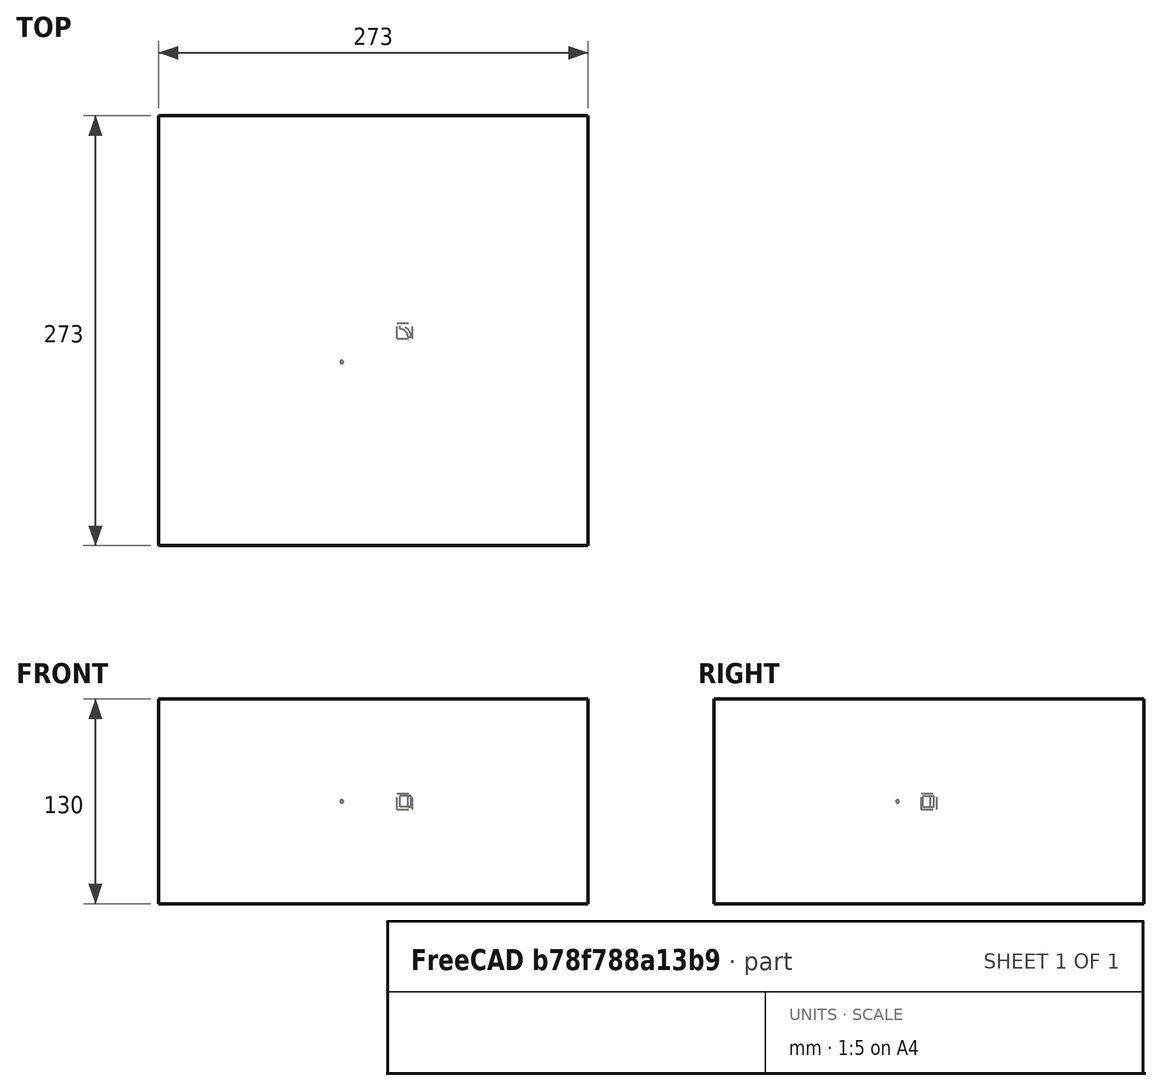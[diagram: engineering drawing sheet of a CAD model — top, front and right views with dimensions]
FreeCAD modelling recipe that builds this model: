
FCSTD DOCUMENT  (FreeCAD 1.0R39109 (Git))
Label: polarArray-of-Part-array-xformed
License: All rights reserved
LicenseURL: http://en.wikipedia.org/wiki/All_rights_reserved
objects: App::DocumentObjectGroupPython×1251, App::Part×5, Part::FeaturePython×4, Part::Sphere×1
note: 4 computed .brp shape members not serialized (recipe doc carries the construction recipe); baked Part::Feature solids carry a one-line shape summary decoded from their .brp

FEATURE [App::DocumentObjectGroupPython] HALFPI  # scripted group (container) (typed FeaturePython)
  name = HALFPI
  value = pi/2.
FEATURE [App::DocumentObjectGroupPython] PI  # scripted group (container) (typed FeaturePython)
  name = PI
  value = 1.*pi
FEATURE [App::DocumentObjectGroupPython] TWOPI  # scripted group (container) (typed FeaturePython)
  name = TWOPI
  value = 2.*pi
FEATURE [App::DocumentObjectGroupPython] Constants  # scripted group (container) (typed FeaturePython)
  Group = -> [HALFPI,PI,TWOPI]
FEATURE [App::DocumentObjectGroupPython] Variables  # scripted group (container) (typed FeaturePython)
FEATURE [App::DocumentObjectGroupPython] Quantities  # scripted group (container) (typed FeaturePython)
FEATURE [App::DocumentObjectGroupPython] Isotopes  # scripted group (container) (typed FeaturePython)
FEATURE [App::DocumentObjectGroupPython] Elements  # scripted group (container) (typed FeaturePython)
FEATURE [App::DocumentObjectGroupPython] Matrix  # scripted group (container) (typed FeaturePython)
FEATURE [App::DocumentObjectGroupPython] Surfaces  # scripted group (container) (typed FeaturePython)
FEATURE [App::DocumentObjectGroupPython] Opticals  # scripted group (container) (typed FeaturePython)
  Group = -> [Matrix,Surfaces]
FEATURE [App::DocumentObjectGroupPython] G4Isotopes  # scripted group (container) (typed FeaturePython)
FEATURE [App::DocumentObjectGroupPython] H_element  # scripted group (container) (typed FeaturePython)
  Z = 1
  atom_value = 1.008
  formula = H
  name = H_element
FEATURE [App::DocumentObjectGroupPython] He_element  # scripted group (container) (typed FeaturePython)
  Z = 2
  atom_value = 4.0026
  formula = He
  name = He_element
FEATURE [App::DocumentObjectGroupPython] Li_element  # scripted group (container) (typed FeaturePython)
  Z = 3
  atom_value = 6.94
  formula = Li
  name = Li_element
FEATURE [App::DocumentObjectGroupPython] Be_element  # scripted group (container) (typed FeaturePython)
  Z = 4
  atom_value = 9.01218
  formula = Be
  name = Be_element
FEATURE [App::DocumentObjectGroupPython] B_element  # scripted group (container) (typed FeaturePython)
  Z = 5
  atom_value = 10.81
  formula = B
  name = B_element
FEATURE [App::DocumentObjectGroupPython] C_element  # scripted group (container) (typed FeaturePython)
  Z = 6
  atom_value = 12.011
  formula = C
  name = C_element
FEATURE [App::DocumentObjectGroupPython] N_element  # scripted group (container) (typed FeaturePython)
  Z = 7
  atom_value = 14.007
  formula = N
  name = N_element
FEATURE [App::DocumentObjectGroupPython] O_element  # scripted group (container) (typed FeaturePython)
  Z = 8
  atom_value = 15.999
  formula = O
  name = O_element
FEATURE [App::DocumentObjectGroupPython] F_element  # scripted group (container) (typed FeaturePython)
  Z = 9
  atom_value = 18.9984
  formula = F
  name = F_element
FEATURE [App::DocumentObjectGroupPython] Ne_element  # scripted group (container) (typed FeaturePython)
  Z = 10
  atom_value = 20.1797
  formula = Ne
  name = Ne_element
FEATURE [App::DocumentObjectGroupPython] Na_element  # scripted group (container) (typed FeaturePython)
  Z = 11
  atom_value = 22.9898
  formula = Na
  name = Na_element
FEATURE [App::DocumentObjectGroupPython] Mg_element  # scripted group (container) (typed FeaturePython)
  Z = 12
  atom_value = 24.305
  formula = Mg
  name = Mg_element
FEATURE [App::DocumentObjectGroupPython] Al_element  # scripted group (container) (typed FeaturePython)
  Z = 13
  atom_value = 26.9815
  formula = Al
  name = Al_element
FEATURE [App::DocumentObjectGroupPython] Si_element  # scripted group (container) (typed FeaturePython)
  Z = 14
  atom_value = 28.085
  formula = Si
  name = Si_element
FEATURE [App::DocumentObjectGroupPython] P_element  # scripted group (container) (typed FeaturePython)
  Z = 15
  atom_value = 30.9738
  formula = P
  name = P_element
FEATURE [App::DocumentObjectGroupPython] S_element  # scripted group (container) (typed FeaturePython)
  Z = 16
  atom_value = 32.06
  formula = S
  name = S_element
FEATURE [App::DocumentObjectGroupPython] Cl_element  # scripted group (container) (typed FeaturePython)
  Z = 17
  atom_value = 35.45
  formula = Cl
  name = Cl_element
FEATURE [App::DocumentObjectGroupPython] Ar_element  # scripted group (container) (typed FeaturePython)
  Z = 18
  atom_value = 39.95
  formula = Ar
  name = Ar_element
FEATURE [App::DocumentObjectGroupPython] K_element  # scripted group (container) (typed FeaturePython)
  Z = 19
  atom_value = 39.0983
  formula = K
  name = K_element
FEATURE [App::DocumentObjectGroupPython] Ca_element  # scripted group (container) (typed FeaturePython)
  Z = 20
  atom_value = 40.078
  formula = Ca
  name = Ca_element
FEATURE [App::DocumentObjectGroupPython] Sc_element  # scripted group (container) (typed FeaturePython)
  Z = 21
  atom_value = 44.9559
  formula = Sc
  name = Sc_element
FEATURE [App::DocumentObjectGroupPython] Ti_element  # scripted group (container) (typed FeaturePython)
  Z = 22
  atom_value = 47.867
  formula = Ti
  name = Ti_element
FEATURE [App::DocumentObjectGroupPython] V_element  # scripted group (container) (typed FeaturePython)
  Z = 23
  atom_value = 50.9415
  formula = V
  name = V_element
FEATURE [App::DocumentObjectGroupPython] Cr_element  # scripted group (container) (typed FeaturePython)
  Z = 24
  atom_value = 51.9961
  formula = Cr
  name = Cr_element
FEATURE [App::DocumentObjectGroupPython] Mn_element  # scripted group (container) (typed FeaturePython)
  Z = 25
  atom_value = 54.938
  formula = Mn
  name = Mn_element
FEATURE [App::DocumentObjectGroupPython] Fe_element  # scripted group (container) (typed FeaturePython)
  Z = 26
  atom_value = 55.845
  formula = Fe
  name = Fe_element
FEATURE [App::DocumentObjectGroupPython] Co_element  # scripted group (container) (typed FeaturePython)
  Z = 27
  atom_value = 58.9332
  formula = Co
  name = Co_element
FEATURE [App::DocumentObjectGroupPython] Ni_element  # scripted group (container) (typed FeaturePython)
  Z = 28
  atom_value = 58.6934
  formula = Ni
  name = Ni_element
FEATURE [App::DocumentObjectGroupPython] Cu_element  # scripted group (container) (typed FeaturePython)
  Z = 29
  atom_value = 63.546
  formula = Cu
  name = Cu_element
FEATURE [App::DocumentObjectGroupPython] Zn_element  # scripted group (container) (typed FeaturePython)
  Z = 30
  atom_value = 65.38
  formula = Zn
  name = Zn_element
FEATURE [App::DocumentObjectGroupPython] Ga_element  # scripted group (container) (typed FeaturePython)
  Z = 31
  atom_value = 69.723
  formula = Ga
  name = Ga_element
FEATURE [App::DocumentObjectGroupPython] Ge_element  # scripted group (container) (typed FeaturePython)
  Z = 32
  atom_value = 72.63
  formula = Ge
  name = Ge_element
FEATURE [App::DocumentObjectGroupPython] As_element  # scripted group (container) (typed FeaturePython)
  Z = 33
  atom_value = 74.9216
  formula = As
  name = As_element
FEATURE [App::DocumentObjectGroupPython] Se_element  # scripted group (container) (typed FeaturePython)
  Z = 34
  atom_value = 78.971
  formula = Se
  name = Se_element
FEATURE [App::DocumentObjectGroupPython] Br_element  # scripted group (container) (typed FeaturePython)
  Z = 35
  atom_value = 79.904
  formula = Br
  name = Br_element
FEATURE [App::DocumentObjectGroupPython] Kr_element  # scripted group (container) (typed FeaturePython)
  Z = 36
  atom_value = 83.798
  formula = Kr
  name = Kr_element
FEATURE [App::DocumentObjectGroupPython] Rb_element  # scripted group (container) (typed FeaturePython)
  Z = 37
  atom_value = 85.4678
  formula = Rb
  name = Rb_element
FEATURE [App::DocumentObjectGroupPython] Sr_element  # scripted group (container) (typed FeaturePython)
  Z = 38
  atom_value = 87.62
  formula = Sr
  name = Sr_element
FEATURE [App::DocumentObjectGroupPython] Y_element  # scripted group (container) (typed FeaturePython)
  Z = 39
  atom_value = 88.9058
  formula = Y
  name = Y_element
FEATURE [App::DocumentObjectGroupPython] Zr_element  # scripted group (container) (typed FeaturePython)
  Z = 40
  atom_value = 91.224
  formula = Zr
  name = Zr_element
FEATURE [App::DocumentObjectGroupPython] Nb_element  # scripted group (container) (typed FeaturePython)
  Z = 41
  atom_value = 92.9064
  formula = Nb
  name = Nb_element
FEATURE [App::DocumentObjectGroupPython] Mo_element  # scripted group (container) (typed FeaturePython)
  Z = 42
  atom_value = 95.95
  formula = Mo
  name = Mo_element
FEATURE [App::DocumentObjectGroupPython] Tc_element  # scripted group (container) (typed FeaturePython)
  Z = 43
  atom_value = 97
  formula = Tc
  name = Tc_element
FEATURE [App::DocumentObjectGroupPython] Ru_element  # scripted group (container) (typed FeaturePython)
  Z = 44
  atom_value = 101.07
  formula = Ru
  name = Ru_element
FEATURE [App::DocumentObjectGroupPython] Rh_element  # scripted group (container) (typed FeaturePython)
  Z = 45
  atom_value = 102.905
  formula = Rh
  name = Rh_element
FEATURE [App::DocumentObjectGroupPython] Pd_element  # scripted group (container) (typed FeaturePython)
  Z = 46
  atom_value = 106.42
  formula = Pd
  name = Pd_element
FEATURE [App::DocumentObjectGroupPython] Ag_element  # scripted group (container) (typed FeaturePython)
  Z = 47
  atom_value = 107.868
  formula = Ag
  name = Ag_element
FEATURE [App::DocumentObjectGroupPython] Cd_element  # scripted group (container) (typed FeaturePython)
  Z = 48
  atom_value = 112.414
  formula = Cd
  name = Cd_element
FEATURE [App::DocumentObjectGroupPython] In_element  # scripted group (container) (typed FeaturePython)
  Z = 49
  atom_value = 114.818
  formula = In
  name = In_element
FEATURE [App::DocumentObjectGroupPython] Sn_element  # scripted group (container) (typed FeaturePython)
  Z = 50
  atom_value = 118.71
  formula = Sn
  name = Sn_element
FEATURE [App::DocumentObjectGroupPython] Sb_element  # scripted group (container) (typed FeaturePython)
  Z = 51
  atom_value = 121.76
  formula = Sb
  name = Sb_element
FEATURE [App::DocumentObjectGroupPython] Te_element  # scripted group (container) (typed FeaturePython)
  Z = 52
  atom_value = 127.6
  formula = Te
  name = Te_element
FEATURE [App::DocumentObjectGroupPython] I_element  # scripted group (container) (typed FeaturePython)
  Z = 53
  atom_value = 126.904
  formula = I
  name = I_element
FEATURE [App::DocumentObjectGroupPython] Xe_element  # scripted group (container) (typed FeaturePython)
  Z = 54
  atom_value = 131.293
  formula = Xe
  name = Xe_element
FEATURE [App::DocumentObjectGroupPython] Cs_element  # scripted group (container) (typed FeaturePython)
  Z = 55
  atom_value = 132.905
  formula = Cs
  name = Cs_element
FEATURE [App::DocumentObjectGroupPython] Ba_element  # scripted group (container) (typed FeaturePython)
  Z = 56
  atom_value = 137.327
  formula = Ba
  name = Ba_element
FEATURE [App::DocumentObjectGroupPython] La_element  # scripted group (container) (typed FeaturePython)
  Z = 57
  atom_value = 138.905
  formula = La
  name = La_element
FEATURE [App::DocumentObjectGroupPython] Ce_element  # scripted group (container) (typed FeaturePython)
  Z = 58
  atom_value = 140.116
  formula = Ce
  name = Ce_element
FEATURE [App::DocumentObjectGroupPython] Pr_element  # scripted group (container) (typed FeaturePython)
  Z = 59
  atom_value = 140.908
  formula = Pr
  name = Pr_element
FEATURE [App::DocumentObjectGroupPython] Nd_element  # scripted group (container) (typed FeaturePython)
  Z = 60
  atom_value = 144.242
  formula = Nd
  name = Nd_element
FEATURE [App::DocumentObjectGroupPython] Pm_element  # scripted group (container) (typed FeaturePython)
  Z = 61
  atom_value = 145
  formula = Pm
  name = Pm_element
FEATURE [App::DocumentObjectGroupPython] Sm_element  # scripted group (container) (typed FeaturePython)
  Z = 62
  atom_value = 150.36
  formula = Sm
  name = Sm_element
FEATURE [App::DocumentObjectGroupPython] Eu_element  # scripted group (container) (typed FeaturePython)
  Z = 63
  atom_value = 151.964
  formula = Eu
  name = Eu_element
FEATURE [App::DocumentObjectGroupPython] Gd_element  # scripted group (container) (typed FeaturePython)
  Z = 64
  atom_value = 157.25
  formula = Gd
  name = Gd_element
FEATURE [App::DocumentObjectGroupPython] Tb_element  # scripted group (container) (typed FeaturePython)
  Z = 65
  atom_value = 158.925
  formula = Tb
  name = Tb_element
FEATURE [App::DocumentObjectGroupPython] Dy_element  # scripted group (container) (typed FeaturePython)
  Z = 66
  atom_value = 162.5
  formula = Dy
  name = Dy_element
FEATURE [App::DocumentObjectGroupPython] Ho_element  # scripted group (container) (typed FeaturePython)
  Z = 67
  atom_value = 164.93
  formula = Ho
  name = Ho_element
FEATURE [App::DocumentObjectGroupPython] Er_element  # scripted group (container) (typed FeaturePython)
  Z = 68
  atom_value = 167.259
  formula = Er
  name = Er_element
FEATURE [App::DocumentObjectGroupPython] Tm_element  # scripted group (container) (typed FeaturePython)
  Z = 69
  atom_value = 168.934
  formula = Tm
  name = Tm_element
FEATURE [App::DocumentObjectGroupPython] Yb_element  # scripted group (container) (typed FeaturePython)
  Z = 70
  atom_value = 173.045
  formula = Yb
  name = Yb_element
FEATURE [App::DocumentObjectGroupPython] Lu_element  # scripted group (container) (typed FeaturePython)
  Z = 71
  atom_value = 174.967
  formula = Lu
  name = Lu_element
FEATURE [App::DocumentObjectGroupPython] Hf_element  # scripted group (container) (typed FeaturePython)
  Z = 72
  atom_value = 178.49
  formula = Hf
  name = Hf_element
FEATURE [App::DocumentObjectGroupPython] Ta_element  # scripted group (container) (typed FeaturePython)
  Z = 73
  atom_value = 180.948
  formula = Ta
  name = Ta_element
FEATURE [App::DocumentObjectGroupPython] W_element  # scripted group (container) (typed FeaturePython)
  Z = 74
  atom_value = 183.84
  formula = W
  name = W_element
FEATURE [App::DocumentObjectGroupPython] Re_element  # scripted group (container) (typed FeaturePython)
  Z = 75
  atom_value = 186.207
  formula = Re
  name = Re_element
FEATURE [App::DocumentObjectGroupPython] Os_element  # scripted group (container) (typed FeaturePython)
  Z = 76
  atom_value = 190.23
  formula = Os
  name = Os_element
FEATURE [App::DocumentObjectGroupPython] Ir_element  # scripted group (container) (typed FeaturePython)
  Z = 77
  atom_value = 192.217
  formula = Ir
  name = Ir_element
FEATURE [App::DocumentObjectGroupPython] Pt_element  # scripted group (container) (typed FeaturePython)
  Z = 78
  atom_value = 195.084
  formula = Pt
  name = Pt_element
FEATURE [App::DocumentObjectGroupPython] Au_element  # scripted group (container) (typed FeaturePython)
  Z = 79
  atom_value = 196.967
  formula = Au
  name = Au_element
FEATURE [App::DocumentObjectGroupPython] Hg_element  # scripted group (container) (typed FeaturePython)
  Z = 80
  atom_value = 200.592
  formula = Hg
  name = Hg_element
FEATURE [App::DocumentObjectGroupPython] Tl_element  # scripted group (container) (typed FeaturePython)
  Z = 81
  atom_value = 204.38
  formula = Tl
  name = Tl_element
FEATURE [App::DocumentObjectGroupPython] Pb_element  # scripted group (container) (typed FeaturePython)
  Z = 82
  atom_value = 207.2
  formula = Pb
  name = Pb_element
FEATURE [App::DocumentObjectGroupPython] Bi_element  # scripted group (container) (typed FeaturePython)
  Z = 83
  atom_value = 208.98
  formula = Bi
  name = Bi_element
FEATURE [App::DocumentObjectGroupPython] Po_element  # scripted group (container) (typed FeaturePython)
  Z = 84
  atom_value = 209
  formula = Po
  name = Po_element
FEATURE [App::DocumentObjectGroupPython] At_element  # scripted group (container) (typed FeaturePython)
  Z = 85
  atom_value = 210
  formula = At
  name = At_element
FEATURE [App::DocumentObjectGroupPython] Rn_element  # scripted group (container) (typed FeaturePython)
  Z = 86
  atom_value = 222
  formula = Rn
  name = Rn_element
FEATURE [App::DocumentObjectGroupPython] Fr_element  # scripted group (container) (typed FeaturePython)
  Z = 87
  atom_value = 223
  formula = Fr
  name = Fr_element
FEATURE [App::DocumentObjectGroupPython] Ra_element  # scripted group (container) (typed FeaturePython)
  Z = 88
  atom_value = 226
  formula = Ra
  name = Ra_element
FEATURE [App::DocumentObjectGroupPython] Ac_element  # scripted group (container) (typed FeaturePython)
  Z = 89
  atom_value = 227
  formula = Ac
  name = Ac_element
FEATURE [App::DocumentObjectGroupPython] Th_element  # scripted group (container) (typed FeaturePython)
  Z = 90
  atom_value = 232.038
  formula = Th
  name = Th_element
FEATURE [App::DocumentObjectGroupPython] Pa_element  # scripted group (container) (typed FeaturePython)
  Z = 91
  atom_value = 231.036
  formula = Pa
  name = Pa_element
FEATURE [App::DocumentObjectGroupPython] U_element  # scripted group (container) (typed FeaturePython)
  Z = 92
  atom_value = 238.029
  formula = U
  name = U_element
FEATURE [App::DocumentObjectGroupPython] Np_element  # scripted group (container) (typed FeaturePython)
  Z = 93
  atom_value = 237
  formula = Np
  name = Np_element
FEATURE [App::DocumentObjectGroupPython] Pu_element  # scripted group (container) (typed FeaturePython)
  Z = 94
  atom_value = 244
  formula = Pu
  name = Pu_element
FEATURE [App::DocumentObjectGroupPython] Am_element  # scripted group (container) (typed FeaturePython)
  Z = 95
  atom_value = 243
  formula = Am
  name = Am_element
FEATURE [App::DocumentObjectGroupPython] Cm_element  # scripted group (container) (typed FeaturePython)
  Z = 96
  atom_value = 247
  formula = Cm
  name = Cm_element
FEATURE [App::DocumentObjectGroupPython] Bk_element  # scripted group (container) (typed FeaturePython)
  Z = 97
  atom_value = 247
  formula = Bk
  name = Bk_element
FEATURE [App::DocumentObjectGroupPython] Cf_element  # scripted group (container) (typed FeaturePython)
  Z = 98
  atom_value = 251
  formula = Cf
  name = Cf_element
FEATURE [App::DocumentObjectGroupPython] G4Elements  # scripted group (container) (typed FeaturePython)
  Group = -> [H_element,He_element,Li_element,Be_element,B_element,C_element,N_element,O_element,F_element,Ne_element,Na_element,Mg_element,Al_element,Si_element,P_element,S_element,Cl_element,Ar_element,K_element,Ca_element,Sc_element,Ti_element,V_element,Cr_element,Mn_element,Fe_element,Co_element,Ni_element,Cu_element,Zn_element,Ga_element,Ge_element,As_element,Se_element,Br_element,Kr_element,Rb_element,+61 more]
FEATURE [App::DocumentObjectGroupPython] H_element001  label="H_element : 0.101"  # scripted group (container) (typed FeaturePython)
  n = 0.101327
FEATURE [App::DocumentObjectGroupPython] C_element001  label="C_element : 0.775"  # scripted group (container) (typed FeaturePython)
  n = 0.7755
FEATURE [App::DocumentObjectGroupPython] N_element001  label="N_element : 0.035"  # scripted group (container) (typed FeaturePython)
  n = 0.035057
FEATURE [App::DocumentObjectGroupPython] O_element001  label="O_element : 0.052"  # scripted group (container) (typed FeaturePython)
  n = 0.0523159
FEATURE [App::DocumentObjectGroupPython] F_element001  label="F_element : 0.017"  # scripted group (container) (typed FeaturePython)
  n = 0.017422
FEATURE [App::DocumentObjectGroupPython] Ca_element001  label="Ca_element : 0.018"  # scripted group (container) (typed FeaturePython)
  n = 0.018378
FEATURE [App::DocumentObjectGroupPython] G4_A_150_TISSUE  label="G4_A-150_TISSUE"  # scripted group (container) (typed FeaturePython)
  Dunit = g/cm3
  Dvalue = 1.127
  Group = -> [H_element001,C_element001,N_element001,O_element001,F_element001,Ca_element001]
  conduct = 2
  density = 1
  expand = 3
  formula = G4_A-150_TISSUE
  name = G4_A-150_TISSUE
  specific = 4
FEATURE [App::DocumentObjectGroupPython] C_element002  label="C_element : 3"  # scripted group (container) (typed FeaturePython)
  n = 3
  ref = C_element
FEATURE [App::DocumentObjectGroupPython] H_element002  label="H_element : 6"  # scripted group (container) (typed FeaturePython)
  n = 6
  ref = H_element
FEATURE [App::DocumentObjectGroupPython] O_element002  label="O_element : 1"  # scripted group (container) (typed FeaturePython)
  n = 1
  ref = O_element
FEATURE [App::DocumentObjectGroupPython] G4_ACETONE  # scripted group (container) (typed FeaturePython)
  Dunit = g/cm3
  Dvalue = 0.7899
  Group = -> [C_element002,H_element002,O_element002]
  conduct = 2
  density = 1
  expand = 3
  formula = G4_ACETONE
  name = G4_ACETONE
  specific = 4
FEATURE [App::DocumentObjectGroupPython] C_element003  label="C_element : 2"  # scripted group (container) (typed FeaturePython)
  n = 2
  ref = C_element
FEATURE [App::DocumentObjectGroupPython] H_element003  label="H_element : 2"  # scripted group (container) (typed FeaturePython)
  n = 2
  ref = H_element
FEATURE [App::DocumentObjectGroupPython] G4_ACETYLENE  # scripted group (container) (typed FeaturePython)
  Dunit = g/cm3
  Dvalue = 0.0010967
  Group = -> [C_element003,H_element003]
  conduct = 2
  density = 1
  expand = 3
  formula = G4_ACETYLENE
  name = G4_ACETYLENE
  specific = 4
FEATURE [App::DocumentObjectGroupPython] C_element004  label="C_element : 5"  # scripted group (container) (typed FeaturePython)
  n = 5
  ref = C_element
FEATURE [App::DocumentObjectGroupPython] H_element004  label="H_element : 5"  # scripted group (container) (typed FeaturePython)
  n = 5
  ref = H_element
FEATURE [App::DocumentObjectGroupPython] N_element002  label="N_element : 5"  # scripted group (container) (typed FeaturePython)
  n = 5
  ref = N_element
FEATURE [App::DocumentObjectGroupPython] G4_ADENINE  # scripted group (container) (typed FeaturePython)
  Dunit = g/cm3
  Dvalue = 1.6
  Group = -> [C_element004,H_element004,N_element002]
  conduct = 2
  density = 1
  expand = 3
  formula = G4_ADENINE
  name = G4_ADENINE
  specific = 4
FEATURE [App::DocumentObjectGroupPython] H_element005  label="H_element : 0.114"  # scripted group (container) (typed FeaturePython)
  n = 0.114
FEATURE [App::DocumentObjectGroupPython] C_element005  label="C_element : 0.598"  # scripted group (container) (typed FeaturePython)
  n = 0.598
FEATURE [App::DocumentObjectGroupPython] N_element003  label="N_element : 0.007"  # scripted group (container) (typed FeaturePython)
  n = 0.007
FEATURE [App::DocumentObjectGroupPython] O_element003  label="O_element : 0.278"  # scripted group (container) (typed FeaturePython)
  n = 0.278
FEATURE [App::DocumentObjectGroupPython] Na_element001  label="Na_element : 0.001"  # scripted group (container) (typed FeaturePython)
  n = 0.001
FEATURE [App::DocumentObjectGroupPython] S_element001  label="S_element : 0.001"  # scripted group (container) (typed FeaturePython)
  n = 0.001
FEATURE [App::DocumentObjectGroupPython] Cl_element001  label="Cl_element : 0.001"  # scripted group (container) (typed FeaturePython)
  n = 0.001
FEATURE [App::DocumentObjectGroupPython] G4_ADIPOSE_TISSUE_ICRP  # scripted group (container) (typed FeaturePython)
  Dunit = g/cm3
  Dvalue = 0.95
  Group = -> [H_element005,C_element005,N_element003,O_element003,Na_element001,S_element001,Cl_element001]
  conduct = 2
  density = 1
  expand = 3
  formula = G4_ADIPOSE_TISSUE_ICRP
  name = G4_ADIPOSE_TISSUE_ICRP
  specific = 4
FEATURE [App::DocumentObjectGroupPython] C_element006  label="C_element : 0.000"  # scripted group (container) (typed FeaturePython)
  n = 0.000124
FEATURE [App::DocumentObjectGroupPython] N_element004  label="N_element : 0.755"  # scripted group (container) (typed FeaturePython)
  n = 0.755268
FEATURE [App::DocumentObjectGroupPython] O_element004  label="O_element : 0.232"  # scripted group (container) (typed FeaturePython)
  n = 0.231781
FEATURE [App::DocumentObjectGroupPython] Ar_element001  label="Ar_element : 0.013"  # scripted group (container) (typed FeaturePython)
  n = 0.012827
FEATURE [App::DocumentObjectGroupPython] G4_AIR  # scripted group (container) (typed FeaturePython)
  Dunit = g/cm3
  Dvalue = 0.00120479
  Group = -> [C_element006,N_element004,O_element004,Ar_element001]
  conduct = 2
  density = 1
  expand = 3
  formula = G4_AIR
  name = G4_AIR
  specific = 4
FEATURE [App::DocumentObjectGroupPython] C_element007  label="C_element : 006"  # scripted group (container) (typed FeaturePython)
  n = 3
  ref = C_element
FEATURE [App::DocumentObjectGroupPython] H_element006  label="H_element : 7"  # scripted group (container) (typed FeaturePython)
  n = 7
  ref = H_element
FEATURE [App::DocumentObjectGroupPython] N_element005  label="N_element : 1"  # scripted group (container) (typed FeaturePython)
  n = 1
  ref = N_element
FEATURE [App::DocumentObjectGroupPython] O_element005  label="O_element : 2"  # scripted group (container) (typed FeaturePython)
  n = 2
  ref = O_element
FEATURE [App::DocumentObjectGroupPython] G4_ALANINE  # scripted group (container) (typed FeaturePython)
  Dunit = g/cm3
  Dvalue = 1.42
  Group = -> [C_element007,H_element006,N_element005,O_element005]
  conduct = 2
  density = 1
  expand = 3
  formula = G4_ALANINE
  name = G4_ALANINE
  specific = 4
FEATURE [App::DocumentObjectGroupPython] Al_element001  label="Al_element : 2"  # scripted group (container) (typed FeaturePython)
  n = 2
  ref = Al_element
FEATURE [App::DocumentObjectGroupPython] O_element006  label="O_element : 3"  # scripted group (container) (typed FeaturePython)
  n = 3
  ref = O_element
FEATURE [App::DocumentObjectGroupPython] G4_ALUMINUM_OXIDE  # scripted group (container) (typed FeaturePython)
  Dunit = g/cm3
  Dvalue = 3.97
  Group = -> [Al_element001,O_element006]
  conduct = 2
  density = 1
  expand = 3
  formula = G4_ALUMINUM_OXIDE
  name = G4_ALUMINUM_OXIDE
  specific = 4
FEATURE [App::DocumentObjectGroupPython] H_element007  label="H_element : 0.106"  # scripted group (container) (typed FeaturePython)
  n = 0.10593
FEATURE [App::DocumentObjectGroupPython] C_element008  label="C_element : 0.789"  # scripted group (container) (typed FeaturePython)
  n = 0.788974
FEATURE [App::DocumentObjectGroupPython] O_element007  label="O_element : 0.105"  # scripted group (container) (typed FeaturePython)
  n = 0.105096
FEATURE [App::DocumentObjectGroupPython] G4_AMBER  # scripted group (container) (typed FeaturePython)
  Dunit = g/cm3
  Dvalue = 1.1
  Group = -> [H_element007,C_element008,O_element007]
  conduct = 2
  density = 1
  expand = 3
  formula = G4_AMBER
  name = G4_AMBER
  specific = 4
FEATURE [App::DocumentObjectGroupPython] N_element006  label="N_element : 006"  # scripted group (container) (typed FeaturePython)
  n = 1
  ref = N_element
FEATURE [App::DocumentObjectGroupPython] H_element008  label="H_element : 3"  # scripted group (container) (typed FeaturePython)
  n = 3
  ref = H_element
FEATURE [App::DocumentObjectGroupPython] G4_AMMONIA  # scripted group (container) (typed FeaturePython)
  Dunit = g/cm3
  Dvalue = 0.000826019
  Group = -> [N_element006,H_element008]
  conduct = 2
  density = 1
  expand = 3
  formula = G4_AMMONIA
  name = G4_AMMONIA
  specific = 4
FEATURE [App::DocumentObjectGroupPython] C_element009  label="C_element : 6"  # scripted group (container) (typed FeaturePython)
  n = 6
  ref = C_element
FEATURE [App::DocumentObjectGroupPython] H_element009  label="H_element : 008"  # scripted group (container) (typed FeaturePython)
  n = 7
  ref = H_element
FEATURE [App::DocumentObjectGroupPython] N_element007  label="N_element : 007"  # scripted group (container) (typed FeaturePython)
  n = 1
  ref = N_element
FEATURE [App::DocumentObjectGroupPython] G4_ANILINE  # scripted group (container) (typed FeaturePython)
  Dunit = g/cm3
  Dvalue = 1.0235
  Group = -> [C_element009,H_element009,N_element007]
  conduct = 2
  density = 1
  expand = 3
  formula = G4_ANILINE
  name = G4_ANILINE
  specific = 4
FEATURE [App::DocumentObjectGroupPython] C_element010  label="C_element : 14"  # scripted group (container) (typed FeaturePython)
  n = 14
  ref = C_element
FEATURE [App::DocumentObjectGroupPython] H_element010  label="H_element : 10"  # scripted group (container) (typed FeaturePython)
  n = 10
  ref = H_element
FEATURE [App::DocumentObjectGroupPython] G4_ANTHRACENE  # scripted group (container) (typed FeaturePython)
  Dunit = g/cm3
  Dvalue = 1.283
  Group = -> [C_element010,H_element010]
  conduct = 2
  density = 1
  expand = 3
  formula = G4_ANTHRACENE
  name = G4_ANTHRACENE
  specific = 4
FEATURE [App::DocumentObjectGroupPython] H_element011  label="H_element : 0.065"  # scripted group (container) (typed FeaturePython)
  n = 0.0654709
FEATURE [App::DocumentObjectGroupPython] C_element011  label="C_element : 0.537"  # scripted group (container) (typed FeaturePython)
  n = 0.536944
FEATURE [App::DocumentObjectGroupPython] N_element008  label="N_element : 0.021"  # scripted group (container) (typed FeaturePython)
  n = 0.0215
FEATURE [App::DocumentObjectGroupPython] O_element008  label="O_element : 0.032"  # scripted group (container) (typed FeaturePython)
  n = 0.032085
FEATURE [App::DocumentObjectGroupPython] F_element002  label="F_element : 0.167"  # scripted group (container) (typed FeaturePython)
  n = 0.167411
FEATURE [App::DocumentObjectGroupPython] Ca_element002  label="Ca_element : 0.177"  # scripted group (container) (typed FeaturePython)
  n = 0.176589
FEATURE [App::DocumentObjectGroupPython] G4_B_100_BONE  label="G4_B-100_BONE"  # scripted group (container) (typed FeaturePython)
  Dunit = g/cm3
  Dvalue = 1.45
  Group = -> [H_element011,C_element011,N_element008,O_element008,F_element002,Ca_element002]
  conduct = 2
  density = 1
  expand = 3
  formula = G4_B-100_BONE
  name = G4_B-100_BONE
  specific = 4
FEATURE [App::DocumentObjectGroupPython] H_element012  label="H_element : 0.057"  # scripted group (container) (typed FeaturePython)
  n = 0.057441
FEATURE [App::DocumentObjectGroupPython] C_element012  label="C_element : 0.790"  # scripted group (container) (typed FeaturePython)
  n = 0.774591
FEATURE [App::DocumentObjectGroupPython] O_element009  label="O_element : 0.168"  # scripted group (container) (typed FeaturePython)
  n = 0.167968
FEATURE [App::DocumentObjectGroupPython] G4_BAKELITE  # scripted group (container) (typed FeaturePython)
  Dunit = g/cm3
  Dvalue = 1.25
  Group = -> [H_element012,C_element012,O_element009]
  conduct = 2
  density = 1
  expand = 3
  formula = G4_BAKELITE
  name = G4_BAKELITE
  specific = 4
FEATURE [App::DocumentObjectGroupPython] Ba_element001  label="Ba_element : 1"  # scripted group (container) (typed FeaturePython)
  n = 1
  ref = Ba_element
FEATURE [App::DocumentObjectGroupPython] F_element003  label="F_element : 2"  # scripted group (container) (typed FeaturePython)
  n = 2
  ref = F_element
FEATURE [App::DocumentObjectGroupPython] G4_BARIUM_FLUORIDE  # scripted group (container) (typed FeaturePython)
  Dunit = g/cm3
  Dvalue = 4.89
  Group = -> [Ba_element001,F_element003]
  conduct = 2
  density = 1
  expand = 3
  formula = G4_BARIUM_FLUORIDE
  name = G4_BARIUM_FLUORIDE
  specific = 4
FEATURE [App::DocumentObjectGroupPython] Ba_element002  label="Ba_element : 002"  # scripted group (container) (typed FeaturePython)
  n = 1
  ref = Ba_element
FEATURE [App::DocumentObjectGroupPython] S_element002  label="S_element : 1"  # scripted group (container) (typed FeaturePython)
  n = 1
  ref = S_element
FEATURE [App::DocumentObjectGroupPython] O_element010  label="O_element : 4"  # scripted group (container) (typed FeaturePython)
  n = 4
  ref = O_element
FEATURE [App::DocumentObjectGroupPython] G4_BARIUM_SULFATE  # scripted group (container) (typed FeaturePython)
  Dunit = g/cm3
  Dvalue = 4.5
  Group = -> [Ba_element002,S_element002,O_element010]
  conduct = 2
  density = 1
  expand = 3
  formula = G4_BARIUM_SULFATE
  name = G4_BARIUM_SULFATE
  specific = 4
FEATURE [App::DocumentObjectGroupPython] C_element013  label="C_element : 007"  # scripted group (container) (typed FeaturePython)
  n = 6
  ref = C_element
FEATURE [App::DocumentObjectGroupPython] H_element013  label="H_element : 009"  # scripted group (container) (typed FeaturePython)
  n = 6
  ref = H_element
FEATURE [App::DocumentObjectGroupPython] G4_BENZENE  # scripted group (container) (typed FeaturePython)
  Dunit = g/cm3
  Dvalue = 0.87865
  Group = -> [C_element013,H_element013]
  conduct = 2
  density = 1
  expand = 3
  formula = G4_BENZENE
  name = G4_BENZENE
  specific = 4
FEATURE [App::DocumentObjectGroupPython] Be_element001  label="Be_element : 1"  # scripted group (container) (typed FeaturePython)
  n = 1
  ref = Be_element
FEATURE [App::DocumentObjectGroupPython] O_element011  label="O_element : 005"  # scripted group (container) (typed FeaturePython)
  n = 1
  ref = O_element
FEATURE [App::DocumentObjectGroupPython] G4_BERYLLIUM_OXIDE  # scripted group (container) (typed FeaturePython)
  Dunit = g/cm3
  Dvalue = 3.01
  Group = -> [Be_element001,O_element011]
  conduct = 2
  density = 1
  expand = 3
  formula = G4_BERYLLIUM_OXIDE
  name = G4_BERYLLIUM_OXIDE
  specific = 4
FEATURE [App::DocumentObjectGroupPython] Bi_element001  label="Bi_element : 4"  # scripted group (container) (typed FeaturePython)
  n = 4
  ref = Bi_element
FEATURE [App::DocumentObjectGroupPython] Ge_element001  label="Ge_element : 3"  # scripted group (container) (typed FeaturePython)
  n = 3
  ref = Ge_element
FEATURE [App::DocumentObjectGroupPython] O_element012  label="O_element : 12"  # scripted group (container) (typed FeaturePython)
  n = 12
  ref = O_element
FEATURE [App::DocumentObjectGroupPython] G4_BGO  # scripted group (container) (typed FeaturePython)
  Dunit = g/cm3
  Dvalue = 7.13
  Group = -> [Bi_element001,Ge_element001,O_element012]
  conduct = 2
  density = 1
  expand = 3
  formula = G4_BGO
  name = G4_BGO
  specific = 4
FEATURE [App::DocumentObjectGroupPython] H_element014  label="H_element : 0.102"  # scripted group (container) (typed FeaturePython)
  n = 0.102
FEATURE [App::DocumentObjectGroupPython] C_element014  label="C_element : 0.110"  # scripted group (container) (typed FeaturePython)
  n = 0.11
FEATURE [App::DocumentObjectGroupPython] N_element009  label="N_element : 0.033"  # scripted group (container) (typed FeaturePython)
  n = 0.033
FEATURE [App::DocumentObjectGroupPython] O_element013  label="O_element : 0.745"  # scripted group (container) (typed FeaturePython)
  n = 0.745
FEATURE [App::DocumentObjectGroupPython] Na_element002  label="Na_element : 0.002"  # scripted group (container) (typed FeaturePython)
  n = 0.001
FEATURE [App::DocumentObjectGroupPython] P_element001  label="P_element : 0.001"  # scripted group (container) (typed FeaturePython)
  n = 0.001
FEATURE [App::DocumentObjectGroupPython] S_element003  label="S_element : 0.002"  # scripted group (container) (typed FeaturePython)
  n = 0.002
FEATURE [App::DocumentObjectGroupPython] Cl_element002  label="Cl_element : 0.003"  # scripted group (container) (typed FeaturePython)
  n = 0.003
FEATURE [App::DocumentObjectGroupPython] K_element001  label="K_element : 0.002"  # scripted group (container) (typed FeaturePython)
  n = 0.002
FEATURE [App::DocumentObjectGroupPython] Fe_element001  label="Fe_element : 0.001"  # scripted group (container) (typed FeaturePython)
  n = 0.001
FEATURE [App::DocumentObjectGroupPython] G4_BLOOD_ICRP  # scripted group (container) (typed FeaturePython)
  Dunit = g/cm3
  Dvalue = 1.06
  Group = -> [H_element014,C_element014,N_element009,O_element013,Na_element002,P_element001,S_element003,Cl_element002,K_element001,Fe_element001]
  conduct = 2
  density = 1
  expand = 3
  formula = G4_BLOOD_ICRP
  name = G4_BLOOD_ICRP
  specific = 4
FEATURE [App::DocumentObjectGroupPython] H_element015  label="H_element : 0.064"  # scripted group (container) (typed FeaturePython)
  n = 0.064
FEATURE [App::DocumentObjectGroupPython] C_element015  label="C_element : 0.278"  # scripted group (container) (typed FeaturePython)
  n = 0.278
FEATURE [App::DocumentObjectGroupPython] N_element010  label="N_element : 0.027"  # scripted group (container) (typed FeaturePython)
  n = 0.027
FEATURE [App::DocumentObjectGroupPython] O_element014  label="O_element : 0.410"  # scripted group (container) (typed FeaturePython)
  n = 0.41
FEATURE [App::DocumentObjectGroupPython] Mg_element001  label="Mg_element : 0.002"  # scripted group (container) (typed FeaturePython)
  n = 0.002
FEATURE [App::DocumentObjectGroupPython] P_element002  label="P_element : 0.070"  # scripted group (container) (typed FeaturePython)
  n = 0.07
FEATURE [App::DocumentObjectGroupPython] S_element004  label="S_element : 0.003"  # scripted group (container) (typed FeaturePython)
  n = 0.002
FEATURE [App::DocumentObjectGroupPython] Ca_element003  label="Ca_element : 0.147"  # scripted group (container) (typed FeaturePython)
  n = 0.147
FEATURE [App::DocumentObjectGroupPython] G4_BONE_COMPACT_ICRU  # scripted group (container) (typed FeaturePython)
  Dunit = g/cm3
  Dvalue = 1.85
  Group = -> [H_element015,C_element015,N_element010,O_element014,Mg_element001,P_element002,S_element004,Ca_element003]
  conduct = 2
  density = 1
  expand = 3
  formula = G4_BONE_COMPACT_ICRU
  name = G4_BONE_COMPACT_ICRU
  specific = 4
FEATURE [App::DocumentObjectGroupPython] H_element016  label="H_element : 0.034"  # scripted group (container) (typed FeaturePython)
  n = 0.034
FEATURE [App::DocumentObjectGroupPython] C_element016  label="C_element : 0.155"  # scripted group (container) (typed FeaturePython)
  n = 0.155
FEATURE [App::DocumentObjectGroupPython] N_element011  label="N_element : 0.042"  # scripted group (container) (typed FeaturePython)
  n = 0.042
FEATURE [App::DocumentObjectGroupPython] O_element015  label="O_element : 0.435"  # scripted group (container) (typed FeaturePython)
  n = 0.435
FEATURE [App::DocumentObjectGroupPython] Na_element003  label="Na_element : 0.003"  # scripted group (container) (typed FeaturePython)
  n = 0.001
FEATURE [App::DocumentObjectGroupPython] Mg_element002  label="Mg_element : 0.003"  # scripted group (container) (typed FeaturePython)
  n = 0.002
FEATURE [App::DocumentObjectGroupPython] P_element003  label="P_element : 0.103"  # scripted group (container) (typed FeaturePython)
  n = 0.103
FEATURE [App::DocumentObjectGroupPython] S_element005  label="S_element : 0.004"  # scripted group (container) (typed FeaturePython)
  n = 0.003
FEATURE [App::DocumentObjectGroupPython] Ca_element004  label="Ca_element : 0.225"  # scripted group (container) (typed FeaturePython)
  n = 0.225
FEATURE [App::DocumentObjectGroupPython] G4_BONE_CORTICAL_ICRP  # scripted group (container) (typed FeaturePython)
  Dunit = g/cm3
  Dvalue = 1.92
  Group = -> [H_element016,C_element016,N_element011,O_element015,Na_element003,Mg_element002,P_element003,S_element005,Ca_element004]
  conduct = 2
  density = 1
  expand = 3
  formula = G4_BONE_CORTICAL_ICRP
  name = G4_BONE_CORTICAL_ICRP
  specific = 4
FEATURE [App::DocumentObjectGroupPython] B_element001  label="B_element : 4"  # scripted group (container) (typed FeaturePython)
  n = 4
  ref = B_element
FEATURE [App::DocumentObjectGroupPython] C_element017  label="C_element : 1"  # scripted group (container) (typed FeaturePython)
  n = 1
  ref = C_element
FEATURE [App::DocumentObjectGroupPython] G4_BORON_CARBIDE  # scripted group (container) (typed FeaturePython)
  Dunit = g/cm3
  Dvalue = 2.52
  Group = -> [B_element001,C_element017]
  conduct = 2
  density = 1
  expand = 3
  formula = G4_BORON_CARBIDE
  name = G4_BORON_CARBIDE
  specific = 4
FEATURE [App::DocumentObjectGroupPython] B_element002  label="B_element : 2"  # scripted group (container) (typed FeaturePython)
  n = 2
  ref = B_element
FEATURE [App::DocumentObjectGroupPython] O_element016  label="O_element : 006"  # scripted group (container) (typed FeaturePython)
  n = 3
  ref = O_element
FEATURE [App::DocumentObjectGroupPython] G4_BORON_OXIDE  # scripted group (container) (typed FeaturePython)
  Dunit = g/cm3
  Dvalue = 1.812
  Group = -> [B_element002,O_element016]
  conduct = 2
  density = 1
  expand = 3
  formula = G4_BORON_OXIDE
  name = G4_BORON_OXIDE
  specific = 4
FEATURE [App::DocumentObjectGroupPython] H_element017  label="H_element : 0.107"  # scripted group (container) (typed FeaturePython)
  n = 0.107
FEATURE [App::DocumentObjectGroupPython] C_element018  label="C_element : 0.145"  # scripted group (container) (typed FeaturePython)
  n = 0.145
FEATURE [App::DocumentObjectGroupPython] N_element012  label="N_element : 0.022"  # scripted group (container) (typed FeaturePython)
  n = 0.022
FEATURE [App::DocumentObjectGroupPython] O_element017  label="O_element : 0.712"  # scripted group (container) (typed FeaturePython)
  n = 0.712
FEATURE [App::DocumentObjectGroupPython] Na_element004  label="Na_element : 0.004"  # scripted group (container) (typed FeaturePython)
  n = 0.002
FEATURE [App::DocumentObjectGroupPython] P_element004  label="P_element : 0.004"  # scripted group (container) (typed FeaturePython)
  n = 0.004
FEATURE [App::DocumentObjectGroupPython] S_element006  label="S_element : 0.005"  # scripted group (container) (typed FeaturePython)
  n = 0.002
FEATURE [App::DocumentObjectGroupPython] Cl_element003  label="Cl_element : 0.004"  # scripted group (container) (typed FeaturePython)
  n = 0.003
FEATURE [App::DocumentObjectGroupPython] K_element002  label="K_element : 0.003"  # scripted group (container) (typed FeaturePython)
  n = 0.003
FEATURE [App::DocumentObjectGroupPython] G4_BRAIN_ICRP  # scripted group (container) (typed FeaturePython)
  Dunit = g/cm3
  Dvalue = 1.04
  Group = -> [H_element017,C_element018,N_element012,O_element017,Na_element004,P_element004,S_element006,Cl_element003,K_element002]
  conduct = 2
  density = 1
  expand = 3
  formula = G4_BRAIN_ICRP
  name = G4_BRAIN_ICRP
  specific = 4
FEATURE [App::DocumentObjectGroupPython] C_element019  label="C_element : 4"  # scripted group (container) (typed FeaturePython)
  n = 4
  ref = C_element
FEATURE [App::DocumentObjectGroupPython] H_element018  label="H_element : 010"  # scripted group (container) (typed FeaturePython)
  n = 10
  ref = H_element
FEATURE [App::DocumentObjectGroupPython] G4_BUTANE  # scripted group (container) (typed FeaturePython)
  Dunit = g/cm3
  Dvalue = 0.00249343
  Group = -> [C_element019,H_element018]
  conduct = 2
  density = 1
  expand = 3
  formula = G4_BUTANE
  name = G4_BUTANE
  specific = 4
FEATURE [App::DocumentObjectGroupPython] C_element020  label="C_element : 008"  # scripted group (container) (typed FeaturePython)
  n = 4
  ref = C_element
FEATURE [App::DocumentObjectGroupPython] H_element019  label="H_element : 011"  # scripted group (container) (typed FeaturePython)
  n = 10
  ref = H_element
FEATURE [App::DocumentObjectGroupPython] O_element018  label="O_element : 007"  # scripted group (container) (typed FeaturePython)
  n = 1
  ref = O_element
FEATURE [App::DocumentObjectGroupPython] G4_N_BUTYL_ALCOHOL  label="G4_N-BUTYL_ALCOHOL"  # scripted group (container) (typed FeaturePython)
  Dunit = g/cm3
  Dvalue = 0.8098
  Group = -> [C_element020,H_element019,O_element018]
  conduct = 2
  density = 1
  expand = 3
  formula = G4_N-BUTYL_ALCOHOL
  name = G4_N-BUTYL_ALCOHOL
  specific = 4
FEATURE [App::DocumentObjectGroupPython] H_element020  label="H_element : 0.025"  # scripted group (container) (typed FeaturePython)
  n = 0.02468
FEATURE [App::DocumentObjectGroupPython] C_element021  label="C_element : 0.502"  # scripted group (container) (typed FeaturePython)
  n = 0.501611
FEATURE [App::DocumentObjectGroupPython] O_element019  label="O_element : 0.005"  # scripted group (container) (typed FeaturePython)
  n = 0.004527
FEATURE [App::DocumentObjectGroupPython] F_element004  label="F_element : 0.465"  # scripted group (container) (typed FeaturePython)
  n = 0.465209
FEATURE [App::DocumentObjectGroupPython] Si_element001  label="Si_element : 0.004"  # scripted group (container) (typed FeaturePython)
  n = 0.003973
FEATURE [App::DocumentObjectGroupPython] G4_C_552  label="G4_C-552"  # scripted group (container) (typed FeaturePython)
  Dunit = g/cm3
  Dvalue = 1.76
  Group = -> [H_element020,C_element021,O_element019,F_element004,Si_element001]
  conduct = 2
  density = 1
  expand = 3
  formula = G4_C-552
  name = G4_C-552
  specific = 4
FEATURE [App::DocumentObjectGroupPython] Cd_element001  label="Cd_element : 1"  # scripted group (container) (typed FeaturePython)
  n = 1
  ref = Cd_element
FEATURE [App::DocumentObjectGroupPython] Te_element001  label="Te_element : 1"  # scripted group (container) (typed FeaturePython)
  n = 1
  ref = Te_element
FEATURE [App::DocumentObjectGroupPython] G4_CADMIUM_TELLURIDE  # scripted group (container) (typed FeaturePython)
  Dunit = g/cm3
  Dvalue = 6.2
  Group = -> [Cd_element001,Te_element001]
  conduct = 2
  density = 1
  expand = 3
  formula = G4_CADMIUM_TELLURIDE
  name = G4_CADMIUM_TELLURIDE
  specific = 4
FEATURE [App::DocumentObjectGroupPython] Cd_element002  label="Cd_element : 002"  # scripted group (container) (typed FeaturePython)
  n = 1
  ref = Cd_element
FEATURE [App::DocumentObjectGroupPython] W_element001  label="W_element : 1"  # scripted group (container) (typed FeaturePython)
  n = 1
  ref = W_element
FEATURE [App::DocumentObjectGroupPython] O_element020  label="O_element : 008"  # scripted group (container) (typed FeaturePython)
  n = 4
  ref = O_element
FEATURE [App::DocumentObjectGroupPython] G4_CADMIUM_TUNGSTATE  # scripted group (container) (typed FeaturePython)
  Dunit = g/cm3
  Dvalue = 7.9
  Group = -> [Cd_element002,W_element001,O_element020]
  conduct = 2
  density = 1
  expand = 3
  formula = G4_CADMIUM_TUNGSTATE
  name = G4_CADMIUM_TUNGSTATE
  specific = 4
FEATURE [App::DocumentObjectGroupPython] Ca_element005  label="Ca_element : 1"  # scripted group (container) (typed FeaturePython)
  n = 1
  ref = Ca_element
FEATURE [App::DocumentObjectGroupPython] C_element022  label="C_element : 009"  # scripted group (container) (typed FeaturePython)
  n = 1
  ref = C_element
FEATURE [App::DocumentObjectGroupPython] O_element021  label="O_element : 009"  # scripted group (container) (typed FeaturePython)
  n = 3
  ref = O_element
FEATURE [App::DocumentObjectGroupPython] G4_CALCIUM_CARBONATE  # scripted group (container) (typed FeaturePython)
  Dunit = g/cm3
  Dvalue = 2.8
  Group = -> [Ca_element005,C_element022,O_element021]
  conduct = 2
  density = 1
  expand = 3
  formula = G4_CALCIUM_CARBONATE
  name = G4_CALCIUM_CARBONATE
  specific = 4
FEATURE [App::DocumentObjectGroupPython] Ca_element006  label="Ca_element : 002"  # scripted group (container) (typed FeaturePython)
  n = 1
  ref = Ca_element
FEATURE [App::DocumentObjectGroupPython] F_element005  label="F_element : 003"  # scripted group (container) (typed FeaturePython)
  n = 2
  ref = F_element
FEATURE [App::DocumentObjectGroupPython] G4_CALCIUM_FLUORIDE  # scripted group (container) (typed FeaturePython)
  Dunit = g/cm3
  Dvalue = 3.18
  Group = -> [Ca_element006,F_element005]
  conduct = 2
  density = 1
  expand = 3
  formula = G4_CALCIUM_FLUORIDE
  name = G4_CALCIUM_FLUORIDE
  specific = 4
FEATURE [App::DocumentObjectGroupPython] Ca_element007  label="Ca_element : 003"  # scripted group (container) (typed FeaturePython)
  n = 1
  ref = Ca_element
FEATURE [App::DocumentObjectGroupPython] O_element022  label="O_element : 010"  # scripted group (container) (typed FeaturePython)
  n = 1
  ref = O_element
FEATURE [App::DocumentObjectGroupPython] G4_CALCIUM_OXIDE  # scripted group (container) (typed FeaturePython)
  Dunit = g/cm3
  Dvalue = 3.3
  Group = -> [Ca_element007,O_element022]
  conduct = 2
  density = 1
  expand = 3
  formula = G4_CALCIUM_OXIDE
  name = G4_CALCIUM_OXIDE
  specific = 4
FEATURE [App::DocumentObjectGroupPython] Ca_element008  label="Ca_element : 004"  # scripted group (container) (typed FeaturePython)
  n = 1
  ref = Ca_element
FEATURE [App::DocumentObjectGroupPython] S_element007  label="S_element : 002"  # scripted group (container) (typed FeaturePython)
  n = 1
  ref = S_element
FEATURE [App::DocumentObjectGroupPython] O_element023  label="O_element : 011"  # scripted group (container) (typed FeaturePython)
  n = 4
  ref = O_element
FEATURE [App::DocumentObjectGroupPython] G4_CALCIUM_SULFATE  # scripted group (container) (typed FeaturePython)
  Dunit = g/cm3
  Dvalue = 2.96
  Group = -> [Ca_element008,S_element007,O_element023]
  conduct = 2
  density = 1
  expand = 3
  formula = G4_CALCIUM_SULFATE
  name = G4_CALCIUM_SULFATE
  specific = 4
FEATURE [App::DocumentObjectGroupPython] Ca_element009  label="Ca_element : 005"  # scripted group (container) (typed FeaturePython)
  n = 1
  ref = Ca_element
FEATURE [App::DocumentObjectGroupPython] W_element002  label="W_element : 002"  # scripted group (container) (typed FeaturePython)
  n = 1
  ref = W_element
FEATURE [App::DocumentObjectGroupPython] O_element024  label="O_element : 012"  # scripted group (container) (typed FeaturePython)
  n = 4
  ref = O_element
FEATURE [App::DocumentObjectGroupPython] G4_CALCIUM_TUNGSTATE  # scripted group (container) (typed FeaturePython)
  Dunit = g/cm3
  Dvalue = 6.062
  Group = -> [Ca_element009,W_element002,O_element024]
  conduct = 2
  density = 1
  expand = 3
  formula = G4_CALCIUM_TUNGSTATE
  name = G4_CALCIUM_TUNGSTATE
  specific = 4
FEATURE [App::DocumentObjectGroupPython] C_element023  label="C_element : 010"  # scripted group (container) (typed FeaturePython)
  n = 1
  ref = C_element
FEATURE [App::DocumentObjectGroupPython] O_element025  label="O_element : 013"  # scripted group (container) (typed FeaturePython)
  n = 2
  ref = O_element
FEATURE [App::DocumentObjectGroupPython] G4_CARBON_DIOXIDE  # scripted group (container) (typed FeaturePython)
  Dunit = g/cm3
  Dvalue = 0.00184212
  Group = -> [C_element023,O_element025]
  conduct = 2
  density = 1
  expand = 3
  formula = G4_CARBON_DIOXIDE
  name = G4_CARBON_DIOXIDE
  specific = 4
FEATURE [App::DocumentObjectGroupPython] C_element024  label="C_element : 011"  # scripted group (container) (typed FeaturePython)
  n = 1
  ref = C_element
FEATURE [App::DocumentObjectGroupPython] Cl_element004  label="Cl_element : 4"  # scripted group (container) (typed FeaturePython)
  n = 4
  ref = Cl_element
FEATURE [App::DocumentObjectGroupPython] G4_CARBON_TETRACHLORIDE  # scripted group (container) (typed FeaturePython)
  Dunit = g/cm3
  Dvalue = 1.594
  Group = -> [C_element024,Cl_element004]
  conduct = 2
  density = 1
  expand = 3
  formula = G4_CARBON_TETRACHLORIDE
  name = G4_CARBON_TETRACHLORIDE
  specific = 4
FEATURE [App::DocumentObjectGroupPython] C_element025  label="C_element : 012"  # scripted group (container) (typed FeaturePython)
  n = 6
  ref = C_element
FEATURE [App::DocumentObjectGroupPython] H_element021  label="H_element : 012"  # scripted group (container) (typed FeaturePython)
  n = 10
  ref = H_element
FEATURE [App::DocumentObjectGroupPython] O_element026  label="O_element : 5"  # scripted group (container) (typed FeaturePython)
  n = 5
  ref = O_element
FEATURE [App::DocumentObjectGroupPython] G4_CELLULOSE_CELLOPHANE  # scripted group (container) (typed FeaturePython)
  Dunit = g/cm3
  Dvalue = 1.42
  Group = -> [C_element025,H_element021,O_element026]
  conduct = 2
  density = 1
  expand = 3
  formula = G4_CELLULOSE_CELLOPHANE
  name = G4_CELLULOSE_CELLOPHANE
  specific = 4
FEATURE [App::DocumentObjectGroupPython] H_element022  label="H_element : 0.067"  # scripted group (container) (typed FeaturePython)
  n = 0.067125
FEATURE [App::DocumentObjectGroupPython] C_element026  label="C_element : 0.545"  # scripted group (container) (typed FeaturePython)
  n = 0.545403
FEATURE [App::DocumentObjectGroupPython] O_element027  label="O_element : 0.387"  # scripted group (container) (typed FeaturePython)
  n = 0.387472
FEATURE [App::DocumentObjectGroupPython] G4_CELLULOSE_BUTYRATE  # scripted group (container) (typed FeaturePython)
  Dunit = g/cm3
  Dvalue = 1.2
  Group = -> [H_element022,C_element026,O_element027]
  conduct = 2
  density = 1
  expand = 3
  formula = G4_CELLULOSE_BUTYRATE
  name = G4_CELLULOSE_BUTYRATE
  specific = 4
FEATURE [App::DocumentObjectGroupPython] H_element023  label="H_element : 0.029"  # scripted group (container) (typed FeaturePython)
  n = 0.029216
FEATURE [App::DocumentObjectGroupPython] C_element027  label="C_element : 0.271"  # scripted group (container) (typed FeaturePython)
  n = 0.271296
FEATURE [App::DocumentObjectGroupPython] N_element013  label="N_element : 0.121"  # scripted group (container) (typed FeaturePython)
  n = 0.121276
FEATURE [App::DocumentObjectGroupPython] O_element028  label="O_element : 0.578"  # scripted group (container) (typed FeaturePython)
  n = 0.578212
FEATURE [App::DocumentObjectGroupPython] G4_CELLULOSE_NITRATE  # scripted group (container) (typed FeaturePython)
  Dunit = g/cm3
  Dvalue = 1.49
  Group = -> [H_element023,C_element027,N_element013,O_element028]
  conduct = 2
  density = 1
  expand = 3
  formula = G4_CELLULOSE_NITRATE
  name = G4_CELLULOSE_NITRATE
  specific = 4
FEATURE [App::DocumentObjectGroupPython] H_element024  label="H_element : 0.108"  # scripted group (container) (typed FeaturePython)
  n = 0.107596
FEATURE [App::DocumentObjectGroupPython] N_element014  label="N_element : 0.001"  # scripted group (container) (typed FeaturePython)
  n = 0.0008
FEATURE [App::DocumentObjectGroupPython] O_element029  label="O_element : 0.875"  # scripted group (container) (typed FeaturePython)
  n = 0.874976
FEATURE [App::DocumentObjectGroupPython] S_element008  label="S_element : 0.015"  # scripted group (container) (typed FeaturePython)
  n = 0.014627
FEATURE [App::DocumentObjectGroupPython] Ce_element001  label="Ce_element : 0.002"  # scripted group (container) (typed FeaturePython)
  n = 0.002001
FEATURE [App::DocumentObjectGroupPython] G4_CERIC_SULFATE  # scripted group (container) (typed FeaturePython)
  Dunit = g/cm3
  Dvalue = 1.03
  Group = -> [H_element024,N_element014,O_element029,S_element008,Ce_element001]
  conduct = 2
  density = 1
  expand = 3
  formula = G4_CERIC_SULFATE
  name = G4_CERIC_SULFATE
  specific = 4
FEATURE [App::DocumentObjectGroupPython] Cs_element001  label="Cs_element : 1"  # scripted group (container) (typed FeaturePython)
  n = 1
  ref = Cs_element
FEATURE [App::DocumentObjectGroupPython] F_element006  label="F_element : 1"  # scripted group (container) (typed FeaturePython)
  n = 1
  ref = F_element
FEATURE [App::DocumentObjectGroupPython] G4_CESIUM_FLUORIDE  # scripted group (container) (typed FeaturePython)
  Dunit = g/cm3
  Dvalue = 4.115
  Group = -> [Cs_element001,F_element006]
  conduct = 2
  density = 1
  expand = 3
  formula = G4_CESIUM_FLUORIDE
  name = G4_CESIUM_FLUORIDE
  specific = 4
FEATURE [App::DocumentObjectGroupPython] Cs_element002  label="Cs_element : 002"  # scripted group (container) (typed FeaturePython)
  n = 1
  ref = Cs_element
FEATURE [App::DocumentObjectGroupPython] I_element001  label="I_element : 1"  # scripted group (container) (typed FeaturePython)
  n = 1
  ref = I_element
FEATURE [App::DocumentObjectGroupPython] G4_CESIUM_IODIDE  # scripted group (container) (typed FeaturePython)
  Dunit = g/cm3
  Dvalue = 4.51
  Group = -> [Cs_element002,I_element001]
  conduct = 2
  density = 1
  expand = 3
  formula = G4_CESIUM_IODIDE
  name = G4_CESIUM_IODIDE
  specific = 4
FEATURE [App::DocumentObjectGroupPython] C_element028  label="C_element : 013"  # scripted group (container) (typed FeaturePython)
  n = 6
  ref = C_element
FEATURE [App::DocumentObjectGroupPython] H_element025  label="H_element : 013"  # scripted group (container) (typed FeaturePython)
  n = 5
  ref = H_element
FEATURE [App::DocumentObjectGroupPython] Cl_element005  label="Cl_element : 1"  # scripted group (container) (typed FeaturePython)
  n = 1
  ref = Cl_element
FEATURE [App::DocumentObjectGroupPython] G4_CHLOROBENZENE  # scripted group (container) (typed FeaturePython)
  Dunit = g/cm3
  Dvalue = 1.1058
  Group = -> [C_element028,H_element025,Cl_element005]
  conduct = 2
  density = 1
  expand = 3
  formula = G4_CHLOROBENZENE
  name = G4_CHLOROBENZENE
  specific = 4
FEATURE [App::DocumentObjectGroupPython] C_element029  label="C_element : 014"  # scripted group (container) (typed FeaturePython)
  n = 1
  ref = C_element
FEATURE [App::DocumentObjectGroupPython] H_element026  label="H_element : 1"  # scripted group (container) (typed FeaturePython)
  n = 1
  ref = H_element
FEATURE [App::DocumentObjectGroupPython] Cl_element006  label="Cl_element : 3"  # scripted group (container) (typed FeaturePython)
  n = 3
  ref = Cl_element
FEATURE [App::DocumentObjectGroupPython] G4_CHLOROFORM  # scripted group (container) (typed FeaturePython)
  Dunit = g/cm3
  Dvalue = 1.4832
  Group = -> [C_element029,H_element026,Cl_element006]
  conduct = 2
  density = 1
  expand = 3
  formula = G4_CHLOROFORM
  name = G4_CHLOROFORM
  specific = 4
FEATURE [App::DocumentObjectGroupPython] H_element027  label="H_element : 0.010"  # scripted group (container) (typed FeaturePython)
  n = 0.01
FEATURE [App::DocumentObjectGroupPython] C_element030  label="C_element : 0.001"  # scripted group (container) (typed FeaturePython)
  n = 0.001
FEATURE [App::DocumentObjectGroupPython] O_element030  label="O_element : 0.529"  # scripted group (container) (typed FeaturePython)
  n = 0.529107
FEATURE [App::DocumentObjectGroupPython] Na_element005  label="Na_element : 0.016"  # scripted group (container) (typed FeaturePython)
  n = 0.016
FEATURE [App::DocumentObjectGroupPython] Mg_element003  label="Mg_element : 0.004"  # scripted group (container) (typed FeaturePython)
  n = 0.002
FEATURE [App::DocumentObjectGroupPython] Al_element002  label="Al_element : 0.034"  # scripted group (container) (typed FeaturePython)
  n = 0.033872
FEATURE [App::DocumentObjectGroupPython] Si_element002  label="Si_element : 0.337"  # scripted group (container) (typed FeaturePython)
  n = 0.337021
FEATURE [App::DocumentObjectGroupPython] K_element003  label="K_element : 0.013"  # scripted group (container) (typed FeaturePython)
  n = 0.013
FEATURE [App::DocumentObjectGroupPython] Ca_element010  label="Ca_element : 0.044"  # scripted group (container) (typed FeaturePython)
  n = 0.044
FEATURE [App::DocumentObjectGroupPython] Fe_element002  label="Fe_element : 0.014"  # scripted group (container) (typed FeaturePython)
  n = 0.014
FEATURE [App::DocumentObjectGroupPython] G4_CONCRETE  # scripted group (container) (typed FeaturePython)
  Dunit = g/cm3
  Dvalue = 2.3
  Group = -> [H_element027,C_element030,O_element030,Na_element005,Mg_element003,Al_element002,Si_element002,K_element003,Ca_element010,Fe_element002]
  conduct = 2
  density = 1
  expand = 3
  formula = G4_CONCRETE
  name = G4_CONCRETE
  specific = 4
FEATURE [App::DocumentObjectGroupPython] C_element031  label="C_element : 015"  # scripted group (container) (typed FeaturePython)
  n = 6
  ref = C_element
FEATURE [App::DocumentObjectGroupPython] H_element028  label="H_element : 12"  # scripted group (container) (typed FeaturePython)
  n = 12
  ref = H_element
FEATURE [App::DocumentObjectGroupPython] G4_CYCLOHEXANE  # scripted group (container) (typed FeaturePython)
  Dunit = g/cm3
  Dvalue = 0.779
  Group = -> [C_element031,H_element028]
  conduct = 2
  density = 1
  expand = 3
  formula = G4_CYCLOHEXANE
  name = G4_CYCLOHEXANE
  specific = 4
FEATURE [App::DocumentObjectGroupPython] C_element032  label="C_element : 016"  # scripted group (container) (typed FeaturePython)
  n = 6
  ref = C_element
FEATURE [App::DocumentObjectGroupPython] H_element029  label="H_element : 4"  # scripted group (container) (typed FeaturePython)
  n = 4
  ref = H_element
FEATURE [App::DocumentObjectGroupPython] Cl_element007  label="Cl_element : 2"  # scripted group (container) (typed FeaturePython)
  n = 2
  ref = Cl_element
FEATURE [App::DocumentObjectGroupPython] G4_1_2_DICHLOROBENZENE  label="G4_1.2-DICHLOROBENZENE"  # scripted group (container) (typed FeaturePython)
  Dunit = g/cm3
  Dvalue = 1.3048
  Group = -> [C_element032,H_element029,Cl_element007]
  conduct = 2
  density = 1
  expand = 3
  formula = G4_1.2-DICHLOROBENZENE
  name = G4_1.2-DICHLOROBENZENE
  specific = 4
FEATURE [App::DocumentObjectGroupPython] C_element033  label="C_element : 017"  # scripted group (container) (typed FeaturePython)
  n = 4
  ref = C_element
FEATURE [App::DocumentObjectGroupPython] H_element030  label="H_element : 8"  # scripted group (container) (typed FeaturePython)
  n = 8
  ref = H_element
FEATURE [App::DocumentObjectGroupPython] O_element031  label="O_element : 014"  # scripted group (container) (typed FeaturePython)
  n = 1
  ref = O_element
FEATURE [App::DocumentObjectGroupPython] Cl_element008  label="Cl_element : 005"  # scripted group (container) (typed FeaturePython)
  n = 2
  ref = Cl_element
FEATURE [App::DocumentObjectGroupPython] G4_DICHLORODIETHYL_ETHER  # scripted group (container) (typed FeaturePython)
  Dunit = g/cm3
  Dvalue = 1.2199
  Group = -> [C_element033,H_element030,O_element031,Cl_element008]
  conduct = 2
  density = 1
  expand = 3
  formula = G4_DICHLORODIETHYL_ETHER
  name = G4_DICHLORODIETHYL_ETHER
  specific = 4
FEATURE [App::DocumentObjectGroupPython] C_element034  label="C_element : 018"  # scripted group (container) (typed FeaturePython)
  n = 2
  ref = C_element
FEATURE [App::DocumentObjectGroupPython] H_element031  label="H_element : 014"  # scripted group (container) (typed FeaturePython)
  n = 4
  ref = H_element
FEATURE [App::DocumentObjectGroupPython] Cl_element009  label="Cl_element : 006"  # scripted group (container) (typed FeaturePython)
  n = 2
  ref = Cl_element
FEATURE [App::DocumentObjectGroupPython] G4_1_2_DICHLOROETHANE  label="G4_1.2-DICHLOROETHANE"  # scripted group (container) (typed FeaturePython)
  Dunit = g/cm3
  Dvalue = 1.2351
  Group = -> [C_element034,H_element031,Cl_element009]
  conduct = 2
  density = 1
  expand = 3
  formula = G4_1.2-DICHLOROETHANE
  name = G4_1.2-DICHLOROETHANE
  specific = 4
FEATURE [App::DocumentObjectGroupPython] C_element035  label="C_element : 019"  # scripted group (container) (typed FeaturePython)
  n = 4
  ref = C_element
FEATURE [App::DocumentObjectGroupPython] H_element032  label="H_element : 015"  # scripted group (container) (typed FeaturePython)
  n = 10
  ref = H_element
FEATURE [App::DocumentObjectGroupPython] O_element032  label="O_element : 015"  # scripted group (container) (typed FeaturePython)
  n = 1
  ref = O_element
FEATURE [App::DocumentObjectGroupPython] G4_DIETHYL_ETHER  # scripted group (container) (typed FeaturePython)
  Dunit = g/cm3
  Dvalue = 0.71378
  Group = -> [C_element035,H_element032,O_element032]
  conduct = 2
  density = 1
  expand = 3
  formula = G4_DIETHYL_ETHER
  name = G4_DIETHYL_ETHER
  specific = 4
FEATURE [App::DocumentObjectGroupPython] C_element036  label="C_element : 020"  # scripted group (container) (typed FeaturePython)
  n = 3
  ref = C_element
FEATURE [App::DocumentObjectGroupPython] H_element033  label="H_element : 016"  # scripted group (container) (typed FeaturePython)
  n = 7
  ref = H_element
FEATURE [App::DocumentObjectGroupPython] N_element015  label="N_element : 008"  # scripted group (container) (typed FeaturePython)
  n = 1
  ref = N_element
FEATURE [App::DocumentObjectGroupPython] O_element033  label="O_element : 016"  # scripted group (container) (typed FeaturePython)
  n = 1
  ref = O_element
FEATURE [App::DocumentObjectGroupPython] G4_N_N_DIMETHYL_FORMAMIDE  label="G4_N.N-DIMETHYL_FORMAMIDE"  # scripted group (container) (typed FeaturePython)
  Dunit = g/cm3
  Dvalue = 0.9487
  Group = -> [C_element036,H_element033,N_element015,O_element033]
  conduct = 2
  density = 1
  expand = 3
  formula = G4_N.N-DIMETHYL_FORMAMIDE
  name = G4_N.N-DIMETHYL_FORMAMIDE
  specific = 4
FEATURE [App::DocumentObjectGroupPython] C_element037  label="C_element : 021"  # scripted group (container) (typed FeaturePython)
  n = 2
  ref = C_element
FEATURE [App::DocumentObjectGroupPython] H_element034  label="H_element : 017"  # scripted group (container) (typed FeaturePython)
  n = 6
  ref = H_element
FEATURE [App::DocumentObjectGroupPython] O_element034  label="O_element : 017"  # scripted group (container) (typed FeaturePython)
  n = 1
  ref = O_element
FEATURE [App::DocumentObjectGroupPython] S_element009  label="S_element : 003"  # scripted group (container) (typed FeaturePython)
  n = 1
  ref = S_element
FEATURE [App::DocumentObjectGroupPython] G4_DIMETHYL_SULFOXIDE  # scripted group (container) (typed FeaturePython)
  Dunit = g/cm3
  Dvalue = 1.1014
  Group = -> [C_element037,H_element034,O_element034,S_element009]
  conduct = 2
  density = 1
  expand = 3
  formula = G4_DIMETHYL_SULFOXIDE
  name = G4_DIMETHYL_SULFOXIDE
  specific = 4
FEATURE [App::DocumentObjectGroupPython] C_element038  label="C_element : 022"  # scripted group (container) (typed FeaturePython)
  n = 2
  ref = C_element
FEATURE [App::DocumentObjectGroupPython] H_element035  label="H_element : 018"  # scripted group (container) (typed FeaturePython)
  n = 6
  ref = H_element
FEATURE [App::DocumentObjectGroupPython] G4_ETHANE  # scripted group (container) (typed FeaturePython)
  Dunit = g/cm3
  Dvalue = 0.00125324
  Group = -> [C_element038,H_element035]
  conduct = 2
  density = 1
  expand = 3
  formula = G4_ETHANE
  name = G4_ETHANE
  specific = 4
FEATURE [App::DocumentObjectGroupPython] C_element039  label="C_element : 023"  # scripted group (container) (typed FeaturePython)
  n = 2
  ref = C_element
FEATURE [App::DocumentObjectGroupPython] H_element036  label="H_element : 019"  # scripted group (container) (typed FeaturePython)
  n = 6
  ref = H_element
FEATURE [App::DocumentObjectGroupPython] O_element035  label="O_element : 018"  # scripted group (container) (typed FeaturePython)
  n = 1
  ref = O_element
FEATURE [App::DocumentObjectGroupPython] G4_ETHYL_ALCOHOL  # scripted group (container) (typed FeaturePython)
  Dunit = g/cm3
  Dvalue = 0.7893
  Group = -> [C_element039,H_element036,O_element035]
  conduct = 2
  density = 1
  expand = 3
  formula = G4_ETHYL_ALCOHOL
  name = G4_ETHYL_ALCOHOL
  specific = 4
FEATURE [App::DocumentObjectGroupPython] H_element037  label="H_element : 0.090"  # scripted group (container) (typed FeaturePython)
  n = 0.090027
FEATURE [App::DocumentObjectGroupPython] C_element040  label="C_element : 0.585"  # scripted group (container) (typed FeaturePython)
  n = 0.585182
FEATURE [App::DocumentObjectGroupPython] O_element036  label="O_element : 0.325"  # scripted group (container) (typed FeaturePython)
  n = 0.324791
FEATURE [App::DocumentObjectGroupPython] G4_ETHYL_CELLULOSE  # scripted group (container) (typed FeaturePython)
  Dunit = g/cm3
  Dvalue = 1.13
  Group = -> [H_element037,C_element040,O_element036]
  conduct = 2
  density = 1
  expand = 3
  formula = G4_ETHYL_CELLULOSE
  name = G4_ETHYL_CELLULOSE
  specific = 4
FEATURE [App::DocumentObjectGroupPython] C_element041  label="C_element : 024"  # scripted group (container) (typed FeaturePython)
  n = 2
  ref = C_element
FEATURE [App::DocumentObjectGroupPython] H_element038  label="H_element : 020"  # scripted group (container) (typed FeaturePython)
  n = 4
  ref = H_element
FEATURE [App::DocumentObjectGroupPython] G4_ETHYLENE  # scripted group (container) (typed FeaturePython)
  Dunit = g/cm3
  Dvalue = 0.00117497
  Group = -> [C_element041,H_element038]
  conduct = 2
  density = 1
  expand = 3
  formula = G4_ETHYLENE
  name = G4_ETHYLENE
  specific = 4
FEATURE [App::DocumentObjectGroupPython] H_element039  label="H_element : 0.096"  # scripted group (container) (typed FeaturePython)
  n = 0.096
FEATURE [App::DocumentObjectGroupPython] C_element042  label="C_element : 0.195"  # scripted group (container) (typed FeaturePython)
  n = 0.195
FEATURE [App::DocumentObjectGroupPython] N_element016  label="N_element : 0.057"  # scripted group (container) (typed FeaturePython)
  n = 0.057
FEATURE [App::DocumentObjectGroupPython] O_element037  label="O_element : 0.646"  # scripted group (container) (typed FeaturePython)
  n = 0.646
FEATURE [App::DocumentObjectGroupPython] Na_element006  label="Na_element : 0.017"  # scripted group (container) (typed FeaturePython)
  n = 0.001
FEATURE [App::DocumentObjectGroupPython] P_element005  label="P_element : 0.104"  # scripted group (container) (typed FeaturePython)
  n = 0.001
FEATURE [App::DocumentObjectGroupPython] S_element010  label="S_element : 0.016"  # scripted group (container) (typed FeaturePython)
  n = 0.003
FEATURE [App::DocumentObjectGroupPython] Cl_element010  label="Cl_element : 0.005"  # scripted group (container) (typed FeaturePython)
  n = 0.001
FEATURE [App::DocumentObjectGroupPython] G4_EYE_LENS_ICRP  # scripted group (container) (typed FeaturePython)
  Dunit = g/cm3
  Dvalue = 1.07
  Group = -> [H_element039,C_element042,N_element016,O_element037,Na_element006,P_element005,S_element010,Cl_element010]
  conduct = 2
  density = 1
  expand = 3
  formula = G4_EYE_LENS_ICRP
  name = G4_EYE_LENS_ICRP
  specific = 4
FEATURE [App::DocumentObjectGroupPython] Fe_element003  label="Fe_element : 2"  # scripted group (container) (typed FeaturePython)
  n = 2
  ref = Fe_element
FEATURE [App::DocumentObjectGroupPython] O_element038  label="O_element : 019"  # scripted group (container) (typed FeaturePython)
  n = 3
  ref = O_element
FEATURE [App::DocumentObjectGroupPython] G4_FERRIC_OXIDE  # scripted group (container) (typed FeaturePython)
  Dunit = g/cm3
  Dvalue = 5.2
  Group = -> [Fe_element003,O_element038]
  conduct = 2
  density = 1
  expand = 3
  formula = G4_FERRIC_OXIDE
  name = G4_FERRIC_OXIDE
  specific = 4
FEATURE [App::DocumentObjectGroupPython] Fe_element004  label="Fe_element : 1"  # scripted group (container) (typed FeaturePython)
  n = 1
  ref = Fe_element
FEATURE [App::DocumentObjectGroupPython] B_element003  label="B_element : 1"  # scripted group (container) (typed FeaturePython)
  n = 1
  ref = B_element
FEATURE [App::DocumentObjectGroupPython] G4_FERROBORIDE  # scripted group (container) (typed FeaturePython)
  Dunit = g/cm3
  Dvalue = 7.15
  Group = -> [Fe_element004,B_element003]
  conduct = 2
  density = 1
  expand = 3
  formula = G4_FERROBORIDE
  name = G4_FERROBORIDE
  specific = 4
FEATURE [App::DocumentObjectGroupPython] Fe_element005  label="Fe_element : 003"  # scripted group (container) (typed FeaturePython)
  n = 1
  ref = Fe_element
FEATURE [App::DocumentObjectGroupPython] O_element039  label="O_element : 020"  # scripted group (container) (typed FeaturePython)
  n = 1
  ref = O_element
FEATURE [App::DocumentObjectGroupPython] G4_FERROUS_OXIDE  # scripted group (container) (typed FeaturePython)
  Dunit = g/cm3
  Dvalue = 5.7
  Group = -> [Fe_element005,O_element039]
  conduct = 2
  density = 1
  expand = 3
  formula = G4_FERROUS_OXIDE
  name = G4_FERROUS_OXIDE
  specific = 4
FEATURE [App::DocumentObjectGroupPython] H_element040  label="H_element : 0.115"  # scripted group (container) (typed FeaturePython)
  n = 0.108259
FEATURE [App::DocumentObjectGroupPython] N_element017  label="N_element : 0.000"  # scripted group (container) (typed FeaturePython)
  n = 2.7e-05
FEATURE [App::DocumentObjectGroupPython] O_element040  label="O_element : 0.879"  # scripted group (container) (typed FeaturePython)
  n = 0.878636
FEATURE [App::DocumentObjectGroupPython] Na_element007  label="Na_element : 0.000"  # scripted group (container) (typed FeaturePython)
  n = 2.2e-05
FEATURE [App::DocumentObjectGroupPython] S_element011  label="S_element : 0.013"  # scripted group (container) (typed FeaturePython)
  n = 0.012968
FEATURE [App::DocumentObjectGroupPython] Cl_element011  label="Cl_element : 0.000"  # scripted group (container) (typed FeaturePython)
  n = 3.4e-05
FEATURE [App::DocumentObjectGroupPython] Fe_element006  label="Fe_element : 0.000"  # scripted group (container) (typed FeaturePython)
  n = 5.4e-05
FEATURE [App::DocumentObjectGroupPython] G4_FERROUS_SULFATE  # scripted group (container) (typed FeaturePython)
  Dunit = g/cm3
  Dvalue = 1.024
  Group = -> [H_element040,N_element017,O_element040,Na_element007,S_element011,Cl_element011,Fe_element006]
  conduct = 2
  density = 1
  expand = 3
  formula = G4_FERROUS_SULFATE
  name = G4_FERROUS_SULFATE
  specific = 4
FEATURE [App::DocumentObjectGroupPython] C_element043  label="C_element : 0.099"  # scripted group (container) (typed FeaturePython)
  n = 0.099335
FEATURE [App::DocumentObjectGroupPython] F_element007  label="F_element : 0.314"  # scripted group (container) (typed FeaturePython)
  n = 0.314247
FEATURE [App::DocumentObjectGroupPython] Cl_element012  label="Cl_element : 0.586"  # scripted group (container) (typed FeaturePython)
  n = 0.586418
FEATURE [App::DocumentObjectGroupPython] G4_FREON_12  label="G4_FREON-12"  # scripted group (container) (typed FeaturePython)
  Dunit = g/cm3
  Dvalue = 1.12
  Group = -> [C_element043,F_element007,Cl_element012]
  conduct = 2
  density = 1
  expand = 3
  formula = G4_FREON-12
  name = G4_FREON-12
  specific = 4
FEATURE [App::DocumentObjectGroupPython] C_element044  label="C_element : 0.057"  # scripted group (container) (typed FeaturePython)
  n = 0.057245
FEATURE [App::DocumentObjectGroupPython] F_element008  label="F_element : 0.181"  # scripted group (container) (typed FeaturePython)
  n = 0.181096
FEATURE [App::DocumentObjectGroupPython] Br_element001  label="Br_element : 0.762"  # scripted group (container) (typed FeaturePython)
  n = 0.761659
FEATURE [App::DocumentObjectGroupPython] G4_FREON_12B2  label="G4_FREON-12B2"  # scripted group (container) (typed FeaturePython)
  Dunit = g/cm3
  Dvalue = 1.8
  Group = -> [C_element044,F_element008,Br_element001]
  conduct = 2
  density = 1
  expand = 3
  formula = G4_FREON-12B2
  name = G4_FREON-12B2
  specific = 4
FEATURE [App::DocumentObjectGroupPython] C_element045  label="C_element : 0.115"  # scripted group (container) (typed FeaturePython)
  n = 0.114983
FEATURE [App::DocumentObjectGroupPython] F_element009  label="F_element : 0.546"  # scripted group (container) (typed FeaturePython)
  n = 0.545621
FEATURE [App::DocumentObjectGroupPython] Cl_element013  label="Cl_element : 0.339"  # scripted group (container) (typed FeaturePython)
  n = 0.339396
FEATURE [App::DocumentObjectGroupPython] G4_FREON_13  label="G4_FREON-13"  # scripted group (container) (typed FeaturePython)
  Dunit = g/cm3
  Dvalue = 0.95
  Group = -> [C_element045,F_element009,Cl_element013]
  conduct = 2
  density = 1
  expand = 3
  formula = G4_FREON-13
  name = G4_FREON-13
  specific = 4
FEATURE [App::DocumentObjectGroupPython] C_element046  label="C_element : 025"  # scripted group (container) (typed FeaturePython)
  n = 1
  ref = C_element
FEATURE [App::DocumentObjectGroupPython] F_element010  label="F_element : 3"  # scripted group (container) (typed FeaturePython)
  n = 3
  ref = F_element
FEATURE [App::DocumentObjectGroupPython] Br_element002  label="Br_element : 1"  # scripted group (container) (typed FeaturePython)
  n = 1
  ref = Br_element
FEATURE [App::DocumentObjectGroupPython] G4_FREON_13B1  label="G4_FREON-13B1"  # scripted group (container) (typed FeaturePython)
  Dunit = g/cm3
  Dvalue = 1.5
  Group = -> [C_element046,F_element010,Br_element002]
  conduct = 2
  density = 1
  expand = 3
  formula = G4_FREON-13B1
  name = G4_FREON-13B1
  specific = 4
FEATURE [App::DocumentObjectGroupPython] C_element047  label="C_element : 0.061"  # scripted group (container) (typed FeaturePython)
  n = 0.061309
FEATURE [App::DocumentObjectGroupPython] F_element011  label="F_element : 0.291"  # scripted group (container) (typed FeaturePython)
  n = 0.290924
FEATURE [App::DocumentObjectGroupPython] I_element002  label="I_element : 0.648"  # scripted group (container) (typed FeaturePython)
  n = 0.647767
FEATURE [App::DocumentObjectGroupPython] G4_FREON_13I1  label="G4_FREON-13I1"  # scripted group (container) (typed FeaturePython)
  Dunit = g/cm3
  Dvalue = 1.8
  Group = -> [C_element047,F_element011,I_element002]
  conduct = 2
  density = 1
  expand = 3
  formula = G4_FREON-13I1
  name = G4_FREON-13I1
  specific = 4
FEATURE [App::DocumentObjectGroupPython] Gd_element001  label="Gd_element : 2"  # scripted group (container) (typed FeaturePython)
  n = 2
  ref = Gd_element
FEATURE [App::DocumentObjectGroupPython] O_element041  label="O_element : 021"  # scripted group (container) (typed FeaturePython)
  n = 2
  ref = O_element
FEATURE [App::DocumentObjectGroupPython] S_element012  label="S_element : 004"  # scripted group (container) (typed FeaturePython)
  n = 1
  ref = S_element
FEATURE [App::DocumentObjectGroupPython] G4_GADOLINIUM_OXYSULFIDE  # scripted group (container) (typed FeaturePython)
  Dunit = g/cm3
  Dvalue = 7.44
  Group = -> [Gd_element001,O_element041,S_element012]
  conduct = 2
  density = 1
  expand = 3
  formula = G4_GADOLINIUM_OXYSULFIDE
  name = G4_GADOLINIUM_OXYSULFIDE
  specific = 4
FEATURE [App::DocumentObjectGroupPython] Ga_element001  label="Ga_element : 1"  # scripted group (container) (typed FeaturePython)
  n = 1
  ref = Ga_element
FEATURE [App::DocumentObjectGroupPython] As_element001  label="As_element : 1"  # scripted group (container) (typed FeaturePython)
  n = 1
  ref = As_element
FEATURE [App::DocumentObjectGroupPython] G4_GALLIUM_ARSENIDE  # scripted group (container) (typed FeaturePython)
  Dunit = g/cm3
  Dvalue = 5.31
  Group = -> [Ga_element001,As_element001]
  conduct = 2
  density = 1
  expand = 3
  formula = G4_GALLIUM_ARSENIDE
  name = G4_GALLIUM_ARSENIDE
  specific = 4
FEATURE [App::DocumentObjectGroupPython] H_element041  label="H_element : 0.081"  # scripted group (container) (typed FeaturePython)
  n = 0.08118
FEATURE [App::DocumentObjectGroupPython] C_element048  label="C_element : 0.416"  # scripted group (container) (typed FeaturePython)
  n = 0.41606
FEATURE [App::DocumentObjectGroupPython] N_element018  label="N_element : 0.111"  # scripted group (container) (typed FeaturePython)
  n = 0.11124
FEATURE [App::DocumentObjectGroupPython] O_element042  label="O_element : 0.381"  # scripted group (container) (typed FeaturePython)
  n = 0.38064
FEATURE [App::DocumentObjectGroupPython] S_element013  label="S_element : 0.011"  # scripted group (container) (typed FeaturePython)
  n = 0.01088
FEATURE [App::DocumentObjectGroupPython] G4_GEL_PHOTO_EMULSION  # scripted group (container) (typed FeaturePython)
  Dunit = g/cm3
  Dvalue = 1.2914
  Group = -> [H_element041,C_element048,N_element018,O_element042,S_element013]
  conduct = 2
  density = 1
  expand = 3
  formula = G4_GEL_PHOTO_EMULSION
  name = G4_GEL_PHOTO_EMULSION
  specific = 4
FEATURE [App::DocumentObjectGroupPython] B_element004  label="B_element : 0.040"  # scripted group (container) (typed FeaturePython)
  n = 0.0400639
FEATURE [App::DocumentObjectGroupPython] O_element043  label="O_element : 0.540"  # scripted group (container) (typed FeaturePython)
  n = 0.539561
FEATURE [App::DocumentObjectGroupPython] Na_element008  label="Na_element : 0.028"  # scripted group (container) (typed FeaturePython)
  n = 0.0281909
FEATURE [App::DocumentObjectGroupPython] Al_element003  label="Al_element : 0.012"  # scripted group (container) (typed FeaturePython)
  n = 0.011644
FEATURE [App::DocumentObjectGroupPython] Si_element003  label="Si_element : 0.377"  # scripted group (container) (typed FeaturePython)
  n = 0.377219
FEATURE [App::DocumentObjectGroupPython] K_element004  label="K_element : 0.014"  # scripted group (container) (typed FeaturePython)
  n = 0.00332099
FEATURE [App::DocumentObjectGroupPython] G4_Pyrex_Glass  # scripted group (container) (typed FeaturePython)
  Dunit = g/cm3
  Dvalue = 2.23
  Group = -> [B_element004,O_element043,Na_element008,Al_element003,Si_element003,K_element004]
  conduct = 2
  density = 1
  expand = 3
  formula = G4_Pyrex_Glass
  name = G4_Pyrex_Glass
  specific = 4
FEATURE [App::DocumentObjectGroupPython] O_element044  label="O_element : 0.156"  # scripted group (container) (typed FeaturePython)
  n = 0.156453
FEATURE [App::DocumentObjectGroupPython] Si_element004  label="Si_element : 0.081"  # scripted group (container) (typed FeaturePython)
  n = 0.080866
FEATURE [App::DocumentObjectGroupPython] Ti_element001  label="Ti_element : 0.008"  # scripted group (container) (typed FeaturePython)
  n = 0.008092
FEATURE [App::DocumentObjectGroupPython] As_element002  label="As_element : 0.003"  # scripted group (container) (typed FeaturePython)
  n = 0.002651
FEATURE [App::DocumentObjectGroupPython] Pb_element001  label="Pb_element : 0.752"  # scripted group (container) (typed FeaturePython)
  n = 0.751938
FEATURE [App::DocumentObjectGroupPython] G4_GLASS_LEAD  # scripted group (container) (typed FeaturePython)
  Dunit = g/cm3
  Dvalue = 6.22
  Group = -> [O_element044,Si_element004,Ti_element001,As_element002,Pb_element001]
  conduct = 2
  density = 1
  expand = 3
  formula = G4_GLASS_LEAD
  name = G4_GLASS_LEAD
  specific = 4
FEATURE [App::DocumentObjectGroupPython] O_element045  label="O_element : 0.460"  # scripted group (container) (typed FeaturePython)
  n = 0.4598
FEATURE [App::DocumentObjectGroupPython] Na_element009  label="Na_element : 0.096"  # scripted group (container) (typed FeaturePython)
  n = 0.0964411
FEATURE [App::DocumentObjectGroupPython] Si_element005  label="Si_element : 0.378"  # scripted group (container) (typed FeaturePython)
  n = 0.336553
FEATURE [App::DocumentObjectGroupPython] Ca_element011  label="Ca_element : 0.107"  # scripted group (container) (typed FeaturePython)
  n = 0.107205
FEATURE [App::DocumentObjectGroupPython] G4_GLASS_PLATE  # scripted group (container) (typed FeaturePython)
  Dunit = g/cm3
  Dvalue = 2.4
  Group = -> [O_element045,Na_element009,Si_element005,Ca_element011]
  conduct = 2
  density = 1
  expand = 3
  formula = G4_GLASS_PLATE
  name = G4_GLASS_PLATE
  specific = 4
FEATURE [App::DocumentObjectGroupPython] C_element049  label="C_element : 026"  # scripted group (container) (typed FeaturePython)
  n = 5
  ref = C_element
FEATURE [App::DocumentObjectGroupPython] H_element042  label="H_element : 021"  # scripted group (container) (typed FeaturePython)
  n = 10
  ref = H_element
FEATURE [App::DocumentObjectGroupPython] N_element019  label="N_element : 2"  # scripted group (container) (typed FeaturePython)
  n = 2
  ref = N_element
FEATURE [App::DocumentObjectGroupPython] O_element046  label="O_element : 022"  # scripted group (container) (typed FeaturePython)
  n = 3
  ref = O_element
FEATURE [App::DocumentObjectGroupPython] G4_GLUTAMINE  # scripted group (container) (typed FeaturePython)
  Dunit = g/cm3
  Dvalue = 1.46
  Group = -> [C_element049,H_element042,N_element019,O_element046]
  conduct = 2
  density = 1
  expand = 3
  formula = G4_GLUTAMINE
  name = G4_GLUTAMINE
  specific = 4
FEATURE [App::DocumentObjectGroupPython] C_element050  label="C_element : 027"  # scripted group (container) (typed FeaturePython)
  n = 3
  ref = C_element
FEATURE [App::DocumentObjectGroupPython] H_element043  label="H_element : 022"  # scripted group (container) (typed FeaturePython)
  n = 8
  ref = H_element
FEATURE [App::DocumentObjectGroupPython] O_element047  label="O_element : 023"  # scripted group (container) (typed FeaturePython)
  n = 3
  ref = O_element
FEATURE [App::DocumentObjectGroupPython] G4_GLYCEROL  # scripted group (container) (typed FeaturePython)
  Dunit = g/cm3
  Dvalue = 1.2613
  Group = -> [C_element050,H_element043,O_element047]
  conduct = 2
  density = 1
  expand = 3
  formula = G4_GLYCEROL
  name = G4_GLYCEROL
  specific = 4
FEATURE [App::DocumentObjectGroupPython] C_element051  label="C_element : 028"  # scripted group (container) (typed FeaturePython)
  n = 5
  ref = C_element
FEATURE [App::DocumentObjectGroupPython] H_element044  label="H_element : 023"  # scripted group (container) (typed FeaturePython)
  n = 5
  ref = H_element
FEATURE [App::DocumentObjectGroupPython] N_element020  label="N_element : 009"  # scripted group (container) (typed FeaturePython)
  n = 5
  ref = N_element
FEATURE [App::DocumentObjectGroupPython] O_element048  label="O_element : 024"  # scripted group (container) (typed FeaturePython)
  n = 1
  ref = O_element
FEATURE [App::DocumentObjectGroupPython] G4_GUANINE  # scripted group (container) (typed FeaturePython)
  Dunit = g/cm3
  Dvalue = 2.2
  Group = -> [C_element051,H_element044,N_element020,O_element048]
  conduct = 2
  density = 1
  expand = 3
  formula = G4_GUANINE
  name = G4_GUANINE
  specific = 4
FEATURE [App::DocumentObjectGroupPython] Ca_element012  label="Ca_element : 006"  # scripted group (container) (typed FeaturePython)
  n = 1
  ref = Ca_element
FEATURE [App::DocumentObjectGroupPython] S_element014  label="S_element : 005"  # scripted group (container) (typed FeaturePython)
  n = 1
  ref = S_element
FEATURE [App::DocumentObjectGroupPython] O_element049  label="O_element : 6"  # scripted group (container) (typed FeaturePython)
  n = 6
  ref = O_element
FEATURE [App::DocumentObjectGroupPython] H_element045  label="H_element : 024"  # scripted group (container) (typed FeaturePython)
  n = 4
  ref = H_element
FEATURE [App::DocumentObjectGroupPython] G4_GYPSUM  # scripted group (container) (typed FeaturePython)
  Dunit = g/cm3
  Dvalue = 2.32
  Group = -> [Ca_element012,S_element014,O_element049,H_element045]
  conduct = 2
  density = 1
  expand = 3
  formula = G4_GYPSUM
  name = G4_GYPSUM
  specific = 4
FEATURE [App::DocumentObjectGroupPython] C_element052  label="C_element : 7"  # scripted group (container) (typed FeaturePython)
  n = 7
  ref = C_element
FEATURE [App::DocumentObjectGroupPython] H_element046  label="H_element : 16"  # scripted group (container) (typed FeaturePython)
  n = 16
  ref = H_element
FEATURE [App::DocumentObjectGroupPython] G4_N_HEPTANE  label="G4_N-HEPTANE"  # scripted group (container) (typed FeaturePython)
  Dunit = g/cm3
  Dvalue = 0.68376
  Group = -> [C_element052,H_element046]
  conduct = 2
  density = 1
  expand = 3
  formula = G4_N-HEPTANE
  name = G4_N-HEPTANE
  specific = 4
FEATURE [App::DocumentObjectGroupPython] C_element053  label="C_element : 029"  # scripted group (container) (typed FeaturePython)
  n = 6
  ref = C_element
FEATURE [App::DocumentObjectGroupPython] H_element047  label="H_element : 14"  # scripted group (container) (typed FeaturePython)
  n = 14
  ref = H_element
FEATURE [App::DocumentObjectGroupPython] G4_N_HEXANE  label="G4_N-HEXANE"  # scripted group (container) (typed FeaturePython)
  Dunit = g/cm3
  Dvalue = 0.6603
  Group = -> [C_element053,H_element047]
  conduct = 2
  density = 1
  expand = 3
  formula = G4_N-HEXANE
  name = G4_N-HEXANE
  specific = 4
FEATURE [App::DocumentObjectGroupPython] C_element054  label="C_element : 22"  # scripted group (container) (typed FeaturePython)
  n = 22
  ref = C_element
FEATURE [App::DocumentObjectGroupPython] H_element048  label="H_element : 025"  # scripted group (container) (typed FeaturePython)
  n = 10
  ref = H_element
FEATURE [App::DocumentObjectGroupPython] N_element021  label="N_element : 010"  # scripted group (container) (typed FeaturePython)
  n = 2
  ref = N_element
FEATURE [App::DocumentObjectGroupPython] O_element050  label="O_element : 025"  # scripted group (container) (typed FeaturePython)
  n = 5
  ref = O_element
FEATURE [App::DocumentObjectGroupPython] G4_KAPTON  # scripted group (container) (typed FeaturePython)
  Dunit = g/cm3
  Dvalue = 1.42
  Group = -> [C_element054,H_element048,N_element021,O_element050]
  conduct = 2
  density = 1
  expand = 3
  formula = G4_KAPTON
  name = G4_KAPTON
  specific = 4
FEATURE [App::DocumentObjectGroupPython] La_element001  label="La_element : 1"  # scripted group (container) (typed FeaturePython)
  n = 1
  ref = La_element
FEATURE [App::DocumentObjectGroupPython] Br_element003  label="Br_element : 002"  # scripted group (container) (typed FeaturePython)
  n = 1
  ref = Br_element
FEATURE [App::DocumentObjectGroupPython] O_element051  label="O_element : 026"  # scripted group (container) (typed FeaturePython)
  n = 1
  ref = O_element
FEATURE [App::DocumentObjectGroupPython] G4_LANTHANUM_OXYBROMIDE  # scripted group (container) (typed FeaturePython)
  Dunit = g/cm3
  Dvalue = 6.28
  Group = -> [La_element001,Br_element003,O_element051]
  conduct = 2
  density = 1
  expand = 3
  formula = G4_LANTHANUM_OXYBROMIDE
  name = G4_LANTHANUM_OXYBROMIDE
  specific = 4
FEATURE [App::DocumentObjectGroupPython] La_element002  label="La_element : 2"  # scripted group (container) (typed FeaturePython)
  n = 2
  ref = La_element
FEATURE [App::DocumentObjectGroupPython] O_element052  label="O_element : 027"  # scripted group (container) (typed FeaturePython)
  n = 2
  ref = O_element
FEATURE [App::DocumentObjectGroupPython] S_element015  label="S_element : 006"  # scripted group (container) (typed FeaturePython)
  n = 1
  ref = S_element
FEATURE [App::DocumentObjectGroupPython] G4_LANTHANUM_OXYSULFIDE  # scripted group (container) (typed FeaturePython)
  Dunit = g/cm3
  Dvalue = 5.86
  Group = -> [La_element002,O_element052,S_element015]
  conduct = 2
  density = 1
  expand = 3
  formula = G4_LANTHANUM_OXYSULFIDE
  name = G4_LANTHANUM_OXYSULFIDE
  specific = 4
FEATURE [App::DocumentObjectGroupPython] O_element053  label="O_element : 0.072"  # scripted group (container) (typed FeaturePython)
  n = 0.071682
FEATURE [App::DocumentObjectGroupPython] Pb_element002  label="Pb_element : 0.928"  # scripted group (container) (typed FeaturePython)
  n = 0.928318
FEATURE [App::DocumentObjectGroupPython] G4_LEAD_OXIDE  # scripted group (container) (typed FeaturePython)
  Dunit = g/cm3
  Dvalue = 9.53
  Group = -> [O_element053,Pb_element002]
  conduct = 2
  density = 1
  expand = 3
  formula = G4_LEAD_OXIDE
  name = G4_LEAD_OXIDE
  specific = 4
FEATURE [App::DocumentObjectGroupPython] Li_element001  label="Li_element : 1"  # scripted group (container) (typed FeaturePython)
  n = 1
  ref = Li_element
FEATURE [App::DocumentObjectGroupPython] N_element022  label="N_element : 011"  # scripted group (container) (typed FeaturePython)
  n = 1
  ref = N_element
FEATURE [App::DocumentObjectGroupPython] H_element049  label="H_element : 026"  # scripted group (container) (typed FeaturePython)
  n = 2
  ref = H_element
FEATURE [App::DocumentObjectGroupPython] G4_LITHIUM_AMIDE  # scripted group (container) (typed FeaturePython)
  Dunit = g/cm3
  Dvalue = 1.178
  Group = -> [Li_element001,N_element022,H_element049]
  conduct = 2
  density = 1
  expand = 3
  formula = G4_LITHIUM_AMIDE
  name = G4_LITHIUM_AMIDE
  specific = 4
FEATURE [App::DocumentObjectGroupPython] Li_element002  label="Li_element : 2"  # scripted group (container) (typed FeaturePython)
  n = 2
  ref = Li_element
FEATURE [App::DocumentObjectGroupPython] C_element055  label="C_element : 030"  # scripted group (container) (typed FeaturePython)
  n = 1
  ref = C_element
FEATURE [App::DocumentObjectGroupPython] O_element054  label="O_element : 028"  # scripted group (container) (typed FeaturePython)
  n = 3
  ref = O_element
FEATURE [App::DocumentObjectGroupPython] G4_LITHIUM_CARBONATE  # scripted group (container) (typed FeaturePython)
  Dunit = g/cm3
  Dvalue = 2.11
  Group = -> [Li_element002,C_element055,O_element054]
  conduct = 2
  density = 1
  expand = 3
  formula = G4_LITHIUM_CARBONATE
  name = G4_LITHIUM_CARBONATE
  specific = 4
FEATURE [App::DocumentObjectGroupPython] Li_element003  label="Li_element : 003"  # scripted group (container) (typed FeaturePython)
  n = 1
  ref = Li_element
FEATURE [App::DocumentObjectGroupPython] F_element012  label="F_element : 004"  # scripted group (container) (typed FeaturePython)
  n = 1
  ref = F_element
FEATURE [App::DocumentObjectGroupPython] G4_LITHIUM_FLUORIDE  # scripted group (container) (typed FeaturePython)
  Dunit = g/cm3
  Dvalue = 2.635
  Group = -> [Li_element003,F_element012]
  conduct = 2
  density = 1
  expand = 3
  formula = G4_LITHIUM_FLUORIDE
  name = G4_LITHIUM_FLUORIDE
  specific = 4
FEATURE [App::DocumentObjectGroupPython] Li_element004  label="Li_element : 004"  # scripted group (container) (typed FeaturePython)
  n = 1
  ref = Li_element
FEATURE [App::DocumentObjectGroupPython] H_element050  label="H_element : 027"  # scripted group (container) (typed FeaturePython)
  n = 1
  ref = H_element
FEATURE [App::DocumentObjectGroupPython] G4_LITHIUM_HYDRIDE  # scripted group (container) (typed FeaturePython)
  Dunit = g/cm3
  Dvalue = 0.82
  Group = -> [Li_element004,H_element050]
  conduct = 2
  density = 1
  expand = 3
  formula = G4_LITHIUM_HYDRIDE
  name = G4_LITHIUM_HYDRIDE
  specific = 4
FEATURE [App::DocumentObjectGroupPython] Li_element005  label="Li_element : 005"  # scripted group (container) (typed FeaturePython)
  n = 1
  ref = Li_element
FEATURE [App::DocumentObjectGroupPython] I_element003  label="I_element : 002"  # scripted group (container) (typed FeaturePython)
  n = 1
  ref = I_element
FEATURE [App::DocumentObjectGroupPython] G4_LITHIUM_IODIDE  # scripted group (container) (typed FeaturePython)
  Dunit = g/cm3
  Dvalue = 3.494
  Group = -> [Li_element005,I_element003]
  conduct = 2
  density = 1
  expand = 3
  formula = G4_LITHIUM_IODIDE
  name = G4_LITHIUM_IODIDE
  specific = 4
FEATURE [App::DocumentObjectGroupPython] Li_element006  label="Li_element : 006"  # scripted group (container) (typed FeaturePython)
  n = 2
  ref = Li_element
FEATURE [App::DocumentObjectGroupPython] O_element055  label="O_element : 029"  # scripted group (container) (typed FeaturePython)
  n = 1
  ref = O_element
FEATURE [App::DocumentObjectGroupPython] G4_LITHIUM_OXIDE  # scripted group (container) (typed FeaturePython)
  Dunit = g/cm3
  Dvalue = 2.013
  Group = -> [Li_element006,O_element055]
  conduct = 2
  density = 1
  expand = 3
  formula = G4_LITHIUM_OXIDE
  name = G4_LITHIUM_OXIDE
  specific = 4
FEATURE [App::DocumentObjectGroupPython] Li_element007  label="Li_element : 007"  # scripted group (container) (typed FeaturePython)
  n = 2
  ref = Li_element
FEATURE [App::DocumentObjectGroupPython] B_element005  label="B_element : 005"  # scripted group (container) (typed FeaturePython)
  n = 4
  ref = B_element
FEATURE [App::DocumentObjectGroupPython] O_element056  label="O_element : 7"  # scripted group (container) (typed FeaturePython)
  n = 7
  ref = O_element
FEATURE [App::DocumentObjectGroupPython] G4_LITHIUM_TETRABORATE  # scripted group (container) (typed FeaturePython)
  Dunit = g/cm3
  Dvalue = 2.44
  Group = -> [Li_element007,B_element005,O_element056]
  conduct = 2
  density = 1
  expand = 3
  formula = G4_LITHIUM_TETRABORATE
  name = G4_LITHIUM_TETRABORATE
  specific = 4
FEATURE [App::DocumentObjectGroupPython] H_element051  label="H_element : 0.105"  # scripted group (container) (typed FeaturePython)
  n = 0.105
FEATURE [App::DocumentObjectGroupPython] C_element056  label="C_element : 0.083"  # scripted group (container) (typed FeaturePython)
  n = 0.083
FEATURE [App::DocumentObjectGroupPython] N_element023  label="N_element : 0.023"  # scripted group (container) (typed FeaturePython)
  n = 0.023
FEATURE [App::DocumentObjectGroupPython] O_element057  label="O_element : 0.779"  # scripted group (container) (typed FeaturePython)
  n = 0.779
FEATURE [App::DocumentObjectGroupPython] Na_element010  label="Na_element : 0.097"  # scripted group (container) (typed FeaturePython)
  n = 0.002
FEATURE [App::DocumentObjectGroupPython] P_element006  label="P_element : 0.105"  # scripted group (container) (typed FeaturePython)
  n = 0.001
FEATURE [App::DocumentObjectGroupPython] S_element016  label="S_element : 0.017"  # scripted group (container) (typed FeaturePython)
  n = 0.002
FEATURE [App::DocumentObjectGroupPython] Cl_element014  label="Cl_element : 0.587"  # scripted group (container) (typed FeaturePython)
  n = 0.003
FEATURE [App::DocumentObjectGroupPython] K_element005  label="K_element : 0.015"  # scripted group (container) (typed FeaturePython)
  n = 0.002
FEATURE [App::DocumentObjectGroupPython] G4_LUNG_ICRP  # scripted group (container) (typed FeaturePython)
  Dunit = g/cm3
  Dvalue = 1.04
  Group = -> [H_element051,C_element056,N_element023,O_element057,Na_element010,P_element006,S_element016,Cl_element014,K_element005]
  conduct = 2
  density = 1
  expand = 3
  formula = G4_LUNG_ICRP
  name = G4_LUNG_ICRP
  specific = 4
FEATURE [App::DocumentObjectGroupPython] H_element052  label="H_element : 0.116"  # scripted group (container) (typed FeaturePython)
  n = 0.114318
FEATURE [App::DocumentObjectGroupPython] C_element057  label="C_element : 0.656"  # scripted group (container) (typed FeaturePython)
  n = 0.655824
FEATURE [App::DocumentObjectGroupPython] O_element058  label="O_element : 0.092"  # scripted group (container) (typed FeaturePython)
  n = 0.0921831
FEATURE [App::DocumentObjectGroupPython] Mg_element004  label="Mg_element : 0.135"  # scripted group (container) (typed FeaturePython)
  n = 0.134792
FEATURE [App::DocumentObjectGroupPython] Ca_element013  label="Ca_element : 0.003"  # scripted group (container) (typed FeaturePython)
  n = 0.002883
FEATURE [App::DocumentObjectGroupPython] G4_M3_WAX  # scripted group (container) (typed FeaturePython)
  Dunit = g/cm3
  Dvalue = 1.05
  Group = -> [H_element052,C_element057,O_element058,Mg_element004,Ca_element013]
  conduct = 2
  density = 1
  expand = 3
  formula = G4_M3_WAX
  name = G4_M3_WAX
  specific = 4
FEATURE [App::DocumentObjectGroupPython] Mg_element005  label="Mg_element : 1"  # scripted group (container) (typed FeaturePython)
  n = 1
  ref = Mg_element
FEATURE [App::DocumentObjectGroupPython] C_element058  label="C_element : 031"  # scripted group (container) (typed FeaturePython)
  n = 1
  ref = C_element
FEATURE [App::DocumentObjectGroupPython] O_element059  label="O_element : 030"  # scripted group (container) (typed FeaturePython)
  n = 3
  ref = O_element
FEATURE [App::DocumentObjectGroupPython] G4_MAGNESIUM_CARBONATE  # scripted group (container) (typed FeaturePython)
  Dunit = g/cm3
  Dvalue = 2.958
  Group = -> [Mg_element005,C_element058,O_element059]
  conduct = 2
  density = 1
  expand = 3
  formula = G4_MAGNESIUM_CARBONATE
  name = G4_MAGNESIUM_CARBONATE
  specific = 4
FEATURE [App::DocumentObjectGroupPython] Mg_element006  label="Mg_element : 002"  # scripted group (container) (typed FeaturePython)
  n = 1
  ref = Mg_element
FEATURE [App::DocumentObjectGroupPython] F_element013  label="F_element : 005"  # scripted group (container) (typed FeaturePython)
  n = 2
  ref = F_element
FEATURE [App::DocumentObjectGroupPython] G4_MAGNESIUM_FLUORIDE  # scripted group (container) (typed FeaturePython)
  Dunit = g/cm3
  Dvalue = 3
  Group = -> [Mg_element006,F_element013]
  conduct = 2
  density = 1
  expand = 3
  formula = G4_MAGNESIUM_FLUORIDE
  name = G4_MAGNESIUM_FLUORIDE
  specific = 4
FEATURE [App::DocumentObjectGroupPython] Mg_element007  label="Mg_element : 003"  # scripted group (container) (typed FeaturePython)
  n = 1
  ref = Mg_element
FEATURE [App::DocumentObjectGroupPython] O_element060  label="O_element : 031"  # scripted group (container) (typed FeaturePython)
  n = 1
  ref = O_element
FEATURE [App::DocumentObjectGroupPython] G4_MAGNESIUM_OXIDE  # scripted group (container) (typed FeaturePython)
  Dunit = g/cm3
  Dvalue = 3.58
  Group = -> [Mg_element007,O_element060]
  conduct = 2
  density = 1
  expand = 3
  formula = G4_MAGNESIUM_OXIDE
  name = G4_MAGNESIUM_OXIDE
  specific = 4
FEATURE [App::DocumentObjectGroupPython] Mg_element008  label="Mg_element : 004"  # scripted group (container) (typed FeaturePython)
  n = 1
  ref = Mg_element
FEATURE [App::DocumentObjectGroupPython] B_element006  label="B_element : 006"  # scripted group (container) (typed FeaturePython)
  n = 4
  ref = B_element
FEATURE [App::DocumentObjectGroupPython] O_element061  label="O_element : 032"  # scripted group (container) (typed FeaturePython)
  n = 7
  ref = O_element
FEATURE [App::DocumentObjectGroupPython] G4_MAGNESIUM_TETRABORATE  # scripted group (container) (typed FeaturePython)
  Dunit = g/cm3
  Dvalue = 2.53
  Group = -> [Mg_element008,B_element006,O_element061]
  conduct = 2
  density = 1
  expand = 3
  formula = G4_MAGNESIUM_TETRABORATE
  name = G4_MAGNESIUM_TETRABORATE
  specific = 4
FEATURE [App::DocumentObjectGroupPython] Hg_element001  label="Hg_element : 1"  # scripted group (container) (typed FeaturePython)
  n = 1
  ref = Hg_element
FEATURE [App::DocumentObjectGroupPython] I_element004  label="I_element : 2"  # scripted group (container) (typed FeaturePython)
  n = 2
  ref = I_element
FEATURE [App::DocumentObjectGroupPython] G4_MERCURIC_IODIDE  # scripted group (container) (typed FeaturePython)
  Dunit = g/cm3
  Dvalue = 6.36
  Group = -> [Hg_element001,I_element004]
  conduct = 2
  density = 1
  expand = 3
  formula = G4_MERCURIC_IODIDE
  name = G4_MERCURIC_IODIDE
  specific = 4
FEATURE [App::DocumentObjectGroupPython] C_element059  label="C_element : 032"  # scripted group (container) (typed FeaturePython)
  n = 1
  ref = C_element
FEATURE [App::DocumentObjectGroupPython] H_element053  label="H_element : 028"  # scripted group (container) (typed FeaturePython)
  n = 4
  ref = H_element
FEATURE [App::DocumentObjectGroupPython] G4_METHANE  # scripted group (container) (typed FeaturePython)
  Dunit = g/cm3
  Dvalue = 0.000667151
  Group = -> [C_element059,H_element053]
  conduct = 2
  density = 1
  expand = 3
  formula = G4_METHANE
  name = G4_METHANE
  specific = 4
FEATURE [App::DocumentObjectGroupPython] C_element060  label="C_element : 033"  # scripted group (container) (typed FeaturePython)
  n = 1
  ref = C_element
FEATURE [App::DocumentObjectGroupPython] H_element054  label="H_element : 029"  # scripted group (container) (typed FeaturePython)
  n = 4
  ref = H_element
FEATURE [App::DocumentObjectGroupPython] O_element062  label="O_element : 033"  # scripted group (container) (typed FeaturePython)
  n = 1
  ref = O_element
FEATURE [App::DocumentObjectGroupPython] G4_METHANOL  # scripted group (container) (typed FeaturePython)
  Dunit = g/cm3
  Dvalue = 0.7914
  Group = -> [C_element060,H_element054,O_element062]
  conduct = 2
  density = 1
  expand = 3
  formula = G4_METHANOL
  name = G4_METHANOL
  specific = 4
FEATURE [App::DocumentObjectGroupPython] H_element055  label="H_element : 0.134"  # scripted group (container) (typed FeaturePython)
  n = 0.13404
FEATURE [App::DocumentObjectGroupPython] C_element061  label="C_element : 0.778"  # scripted group (container) (typed FeaturePython)
  n = 0.77796
FEATURE [App::DocumentObjectGroupPython] O_element063  label="O_element : 0.035"  # scripted group (container) (typed FeaturePython)
  n = 0.03502
FEATURE [App::DocumentObjectGroupPython] Mg_element009  label="Mg_element : 0.039"  # scripted group (container) (typed FeaturePython)
  n = 0.038594
FEATURE [App::DocumentObjectGroupPython] Ti_element002  label="Ti_element : 0.014"  # scripted group (container) (typed FeaturePython)
  n = 0.014386
FEATURE [App::DocumentObjectGroupPython] G4_MIX_D_WAX  # scripted group (container) (typed FeaturePython)
  Dunit = g/cm3
  Dvalue = 0.99
  Group = -> [H_element055,C_element061,O_element063,Mg_element009,Ti_element002]
  conduct = 2
  density = 1
  expand = 3
  formula = G4_MIX_D_WAX
  name = G4_MIX_D_WAX
  specific = 4
FEATURE [App::DocumentObjectGroupPython] H_element056  label="H_element : 0.135"  # scripted group (container) (typed FeaturePython)
  n = 0.081192
FEATURE [App::DocumentObjectGroupPython] C_element062  label="C_element : 0.583"  # scripted group (container) (typed FeaturePython)
  n = 0.583442
FEATURE [App::DocumentObjectGroupPython] N_element024  label="N_element : 0.018"  # scripted group (container) (typed FeaturePython)
  n = 0.017798
FEATURE [App::DocumentObjectGroupPython] O_element064  label="O_element : 0.186"  # scripted group (container) (typed FeaturePython)
  n = 0.186381
FEATURE [App::DocumentObjectGroupPython] Mg_element010  label="Mg_element : 0.130"  # scripted group (container) (typed FeaturePython)
  n = 0.130287
FEATURE [App::DocumentObjectGroupPython] Cl_element015  label="Cl_element : 0.588"  # scripted group (container) (typed FeaturePython)
  n = 0.0009
FEATURE [App::DocumentObjectGroupPython] G4_MS20_TISSUE  # scripted group (container) (typed FeaturePython)
  Dunit = g/cm3
  Dvalue = 1
  Group = -> [H_element056,C_element062,N_element024,O_element064,Mg_element010,Cl_element015]
  conduct = 2
  density = 1
  expand = 3
  formula = G4_MS20_TISSUE
  name = G4_MS20_TISSUE
  specific = 4
FEATURE [App::DocumentObjectGroupPython] H_element057  label="H_element : 0.136"  # scripted group (container) (typed FeaturePython)
  n = 0.102
FEATURE [App::DocumentObjectGroupPython] C_element063  label="C_element : 0.143"  # scripted group (container) (typed FeaturePython)
  n = 0.143
FEATURE [App::DocumentObjectGroupPython] N_element025  label="N_element : 0.034"  # scripted group (container) (typed FeaturePython)
  n = 0.034
FEATURE [App::DocumentObjectGroupPython] O_element065  label="O_element : 0.710"  # scripted group (container) (typed FeaturePython)
  n = 0.71
FEATURE [App::DocumentObjectGroupPython] Na_element011  label="Na_element : 0.098"  # scripted group (container) (typed FeaturePython)
  n = 0.001
FEATURE [App::DocumentObjectGroupPython] P_element007  label="P_element : 0.002"  # scripted group (container) (typed FeaturePython)
  n = 0.002
FEATURE [App::DocumentObjectGroupPython] S_element017  label="S_element : 0.018"  # scripted group (container) (typed FeaturePython)
  n = 0.003
FEATURE [App::DocumentObjectGroupPython] Cl_element016  label="Cl_element : 0.589"  # scripted group (container) (typed FeaturePython)
  n = 0.001
FEATURE [App::DocumentObjectGroupPython] K_element006  label="K_element : 0.004"  # scripted group (container) (typed FeaturePython)
  n = 0.004
FEATURE [App::DocumentObjectGroupPython] G4_MUSCLE_SKELETAL_ICRP  # scripted group (container) (typed FeaturePython)
  Dunit = g/cm3
  Dvalue = 1.05
  Group = -> [H_element057,C_element063,N_element025,O_element065,Na_element011,P_element007,S_element017,Cl_element016,K_element006]
  conduct = 2
  density = 1
  expand = 3
  formula = G4_MUSCLE_SKELETAL_ICRP
  name = G4_MUSCLE_SKELETAL_ICRP
  specific = 4
FEATURE [App::DocumentObjectGroupPython] H_element058  label="H_element : 0.137"  # scripted group (container) (typed FeaturePython)
  n = 0.102102
FEATURE [App::DocumentObjectGroupPython] C_element064  label="C_element : 0.123"  # scripted group (container) (typed FeaturePython)
  n = 0.123123
FEATURE [App::DocumentObjectGroupPython] N_element026  label="N_element : 0.756"  # scripted group (container) (typed FeaturePython)
  n = 0.035035
FEATURE [App::DocumentObjectGroupPython] O_element066  label="O_element : 0.730"  # scripted group (container) (typed FeaturePython)
  n = 0.72973
FEATURE [App::DocumentObjectGroupPython] Na_element012  label="Na_element : 0.099"  # scripted group (container) (typed FeaturePython)
  n = 0.001001
FEATURE [App::DocumentObjectGroupPython] P_element008  label="P_element : 0.106"  # scripted group (container) (typed FeaturePython)
  n = 0.002002
FEATURE [App::DocumentObjectGroupPython] S_element018  label="S_element : 0.019"  # scripted group (container) (typed FeaturePython)
  n = 0.004004
FEATURE [App::DocumentObjectGroupPython] K_element007  label="K_element : 0.016"  # scripted group (container) (typed FeaturePython)
  n = 0.003003
FEATURE [App::DocumentObjectGroupPython] G4_MUSCLE_STRIATED_ICRU  # scripted group (container) (typed FeaturePython)
  Dunit = g/cm3
  Dvalue = 1.04
  Group = -> [H_element058,C_element064,N_element026,O_element066,Na_element012,P_element008,S_element018,K_element007]
  conduct = 2
  density = 1
  expand = 3
  formula = G4_MUSCLE_STRIATED_ICRU
  name = G4_MUSCLE_STRIATED_ICRU
  specific = 4
FEATURE [App::DocumentObjectGroupPython] H_element059  label="H_element : 0.098"  # scripted group (container) (typed FeaturePython)
  n = 0.0982341
FEATURE [App::DocumentObjectGroupPython] C_element065  label="C_element : 0.156"  # scripted group (container) (typed FeaturePython)
  n = 0.156214
FEATURE [App::DocumentObjectGroupPython] N_element027  label="N_element : 0.757"  # scripted group (container) (typed FeaturePython)
  n = 0.035451
FEATURE [App::DocumentObjectGroupPython] O_element067  label="O_element : 0.880"  # scripted group (container) (typed FeaturePython)
  n = 0.710101
FEATURE [App::DocumentObjectGroupPython] G4_MUSCLE_WITH_SUCROSE  # scripted group (container) (typed FeaturePython)
  Dunit = g/cm3
  Dvalue = 1.11
  Group = -> [H_element059,C_element065,N_element027,O_element067]
  conduct = 2
  density = 1
  expand = 3
  formula = G4_MUSCLE_WITH_SUCROSE
  name = G4_MUSCLE_WITH_SUCROSE
  specific = 4
FEATURE [App::DocumentObjectGroupPython] H_element060  label="H_element : 0.138"  # scripted group (container) (typed FeaturePython)
  n = 0.101969
FEATURE [App::DocumentObjectGroupPython] C_element066  label="C_element : 0.120"  # scripted group (container) (typed FeaturePython)
  n = 0.120058
FEATURE [App::DocumentObjectGroupPython] N_element028  label="N_element : 0.758"  # scripted group (container) (typed FeaturePython)
  n = 0.035451
FEATURE [App::DocumentObjectGroupPython] O_element068  label="O_element : 0.743"  # scripted group (container) (typed FeaturePython)
  n = 0.742522
FEATURE [App::DocumentObjectGroupPython] G4_MUSCLE_WITHOUT_SUCROSE  # scripted group (container) (typed FeaturePython)
  Dunit = g/cm3
  Dvalue = 1.07
  Group = -> [H_element060,C_element066,N_element028,O_element068]
  conduct = 2
  density = 1
  expand = 3
  formula = G4_MUSCLE_WITHOUT_SUCROSE
  name = G4_MUSCLE_WITHOUT_SUCROSE
  specific = 4
FEATURE [App::DocumentObjectGroupPython] C_element067  label="C_element : 10"  # scripted group (container) (typed FeaturePython)
  n = 10
  ref = C_element
FEATURE [App::DocumentObjectGroupPython] H_element061  label="H_element : 030"  # scripted group (container) (typed FeaturePython)
  n = 8
  ref = H_element
FEATURE [App::DocumentObjectGroupPython] G4_NAPHTHALENE  # scripted group (container) (typed FeaturePython)
  Dunit = g/cm3
  Dvalue = 1.145
  Group = -> [C_element067,H_element061]
  conduct = 2
  density = 1
  expand = 3
  formula = G4_NAPHTHALENE
  name = G4_NAPHTHALENE
  specific = 4
FEATURE [App::DocumentObjectGroupPython] C_element068  label="C_element : 034"  # scripted group (container) (typed FeaturePython)
  n = 6
  ref = C_element
FEATURE [App::DocumentObjectGroupPython] H_element062  label="H_element : 031"  # scripted group (container) (typed FeaturePython)
  n = 5
  ref = H_element
FEATURE [App::DocumentObjectGroupPython] N_element029  label="N_element : 012"  # scripted group (container) (typed FeaturePython)
  n = 1
  ref = N_element
FEATURE [App::DocumentObjectGroupPython] O_element069  label="O_element : 034"  # scripted group (container) (typed FeaturePython)
  n = 2
  ref = O_element
FEATURE [App::DocumentObjectGroupPython] G4_NITROBENZENE  # scripted group (container) (typed FeaturePython)
  Dunit = g/cm3
  Dvalue = 1.19867
  Group = -> [C_element068,H_element062,N_element029,O_element069]
  conduct = 2
  density = 1
  expand = 3
  formula = G4_NITROBENZENE
  name = G4_NITROBENZENE
  specific = 4
FEATURE [App::DocumentObjectGroupPython] N_element030  label="N_element : 013"  # scripted group (container) (typed FeaturePython)
  n = 2
  ref = N_element
FEATURE [App::DocumentObjectGroupPython] O_element070  label="O_element : 035"  # scripted group (container) (typed FeaturePython)
  n = 1
  ref = O_element
FEATURE [App::DocumentObjectGroupPython] G4_NITROUS_OXIDE  # scripted group (container) (typed FeaturePython)
  Dunit = g/cm3
  Dvalue = 0.00183094
  Group = -> [N_element030,O_element070]
  conduct = 2
  density = 1
  expand = 3
  formula = G4_NITROUS_OXIDE
  name = G4_NITROUS_OXIDE
  specific = 4
FEATURE [App::DocumentObjectGroupPython] H_element063  label="H_element : 0.104"  # scripted group (container) (typed FeaturePython)
  n = 0.103509
FEATURE [App::DocumentObjectGroupPython] C_element069  label="C_element : 0.648"  # scripted group (container) (typed FeaturePython)
  n = 0.648416
FEATURE [App::DocumentObjectGroupPython] N_element031  label="N_element : 0.100"  # scripted group (container) (typed FeaturePython)
  n = 0.0995361
FEATURE [App::DocumentObjectGroupPython] O_element071  label="O_element : 0.149"  # scripted group (container) (typed FeaturePython)
  n = 0.148539
FEATURE [App::DocumentObjectGroupPython] G4_NYLON_8062  label="G4_NYLON-8062"  # scripted group (container) (typed FeaturePython)
  Dunit = g/cm3
  Dvalue = 1.08
  Group = -> [H_element063,C_element069,N_element031,O_element071]
  conduct = 2
  density = 1
  expand = 3
  formula = G4_NYLON-8062
  name = G4_NYLON-8062
  specific = 4
FEATURE [App::DocumentObjectGroupPython] C_element070  label="C_element : 035"  # scripted group (container) (typed FeaturePython)
  n = 6
  ref = C_element
FEATURE [App::DocumentObjectGroupPython] H_element064  label="H_element : 11"  # scripted group (container) (typed FeaturePython)
  n = 11
  ref = H_element
FEATURE [App::DocumentObjectGroupPython] N_element032  label="N_element : 014"  # scripted group (container) (typed FeaturePython)
  n = 1
  ref = N_element
FEATURE [App::DocumentObjectGroupPython] O_element072  label="O_element : 036"  # scripted group (container) (typed FeaturePython)
  n = 1
  ref = O_element
FEATURE [App::DocumentObjectGroupPython] G4_NYLON_6_6  label="G4_NYLON-6-6"  # scripted group (container) (typed FeaturePython)
  Dunit = g/cm3
  Dvalue = 1.14
  Group = -> [C_element070,H_element064,N_element032,O_element072]
  conduct = 2
  density = 1
  expand = 3
  formula = G4_NYLON-6-6
  name = G4_NYLON-6-6
  specific = 4
FEATURE [App::DocumentObjectGroupPython] H_element065  label="H_element : 0.139"  # scripted group (container) (typed FeaturePython)
  n = 0.107062
FEATURE [App::DocumentObjectGroupPython] C_element071  label="C_element : 0.680"  # scripted group (container) (typed FeaturePython)
  n = 0.680449
FEATURE [App::DocumentObjectGroupPython] N_element033  label="N_element : 0.099"  # scripted group (container) (typed FeaturePython)
  n = 0.099189
FEATURE [App::DocumentObjectGroupPython] O_element073  label="O_element : 0.113"  # scripted group (container) (typed FeaturePython)
  n = 0.1133
FEATURE [App::DocumentObjectGroupPython] G4_NYLON_6_10  label="G4_NYLON-6-10"  # scripted group (container) (typed FeaturePython)
  Dunit = g/cm3
  Dvalue = 1.14
  Group = -> [H_element065,C_element071,N_element033,O_element073]
  conduct = 2
  density = 1
  expand = 3
  formula = G4_NYLON-6-10
  name = G4_NYLON-6-10
  specific = 4
FEATURE [App::DocumentObjectGroupPython] H_element066  label="H_element : 0.140"  # scripted group (container) (typed FeaturePython)
  n = 0.115476
FEATURE [App::DocumentObjectGroupPython] C_element072  label="C_element : 0.721"  # scripted group (container) (typed FeaturePython)
  n = 0.720818
FEATURE [App::DocumentObjectGroupPython] N_element034  label="N_element : 0.076"  # scripted group (container) (typed FeaturePython)
  n = 0.0764169
FEATURE [App::DocumentObjectGroupPython] O_element074  label="O_element : 0.087"  # scripted group (container) (typed FeaturePython)
  n = 0.0872889
FEATURE [App::DocumentObjectGroupPython] G4_NYLON_11_RILSAN  label="G4_NYLON-11_RILSAN"  # scripted group (container) (typed FeaturePython)
  Dunit = g/cm3
  Dvalue = 1.425
  Group = -> [H_element066,C_element072,N_element034,O_element074]
  conduct = 2
  density = 1
  expand = 3
  formula = G4_NYLON-11_RILSAN
  name = G4_NYLON-11_RILSAN
  specific = 4
FEATURE [App::DocumentObjectGroupPython] C_element073  label="C_element : 8"  # scripted group (container) (typed FeaturePython)
  n = 8
  ref = C_element
FEATURE [App::DocumentObjectGroupPython] H_element067  label="H_element : 18"  # scripted group (container) (typed FeaturePython)
  n = 18
  ref = H_element
FEATURE [App::DocumentObjectGroupPython] G4_OCTANE  # scripted group (container) (typed FeaturePython)
  Dunit = g/cm3
  Dvalue = 0.7026
  Group = -> [C_element073,H_element067]
  conduct = 2
  density = 1
  expand = 3
  formula = G4_OCTANE
  name = G4_OCTANE
  specific = 4
FEATURE [App::DocumentObjectGroupPython] C_element074  label="C_element : 25"  # scripted group (container) (typed FeaturePython)
  n = 25
  ref = C_element
FEATURE [App::DocumentObjectGroupPython] H_element068  label="H_element : 52"  # scripted group (container) (typed FeaturePython)
  n = 52
  ref = H_element
FEATURE [App::DocumentObjectGroupPython] G4_PARAFFIN  # scripted group (container) (typed FeaturePython)
  Dunit = g/cm3
  Dvalue = 0.93
  Group = -> [C_element074,H_element068]
  conduct = 2
  density = 1
  expand = 3
  formula = G4_PARAFFIN
  name = G4_PARAFFIN
  specific = 4
FEATURE [App::DocumentObjectGroupPython] C_element075  label="C_element : 036"  # scripted group (container) (typed FeaturePython)
  n = 5
  ref = C_element
FEATURE [App::DocumentObjectGroupPython] H_element069  label="H_element : 032"  # scripted group (container) (typed FeaturePython)
  n = 12
  ref = H_element
FEATURE [App::DocumentObjectGroupPython] G4_N_PENTANE  label="G4_N-PENTANE"  # scripted group (container) (typed FeaturePython)
  Dunit = g/cm3
  Dvalue = 0.6262
  Group = -> [C_element075,H_element069]
  conduct = 2
  density = 1
  expand = 3
  formula = G4_N-PENTANE
  name = G4_N-PENTANE
  specific = 4
FEATURE [App::DocumentObjectGroupPython] H_element070  label="H_element : 0.014"  # scripted group (container) (typed FeaturePython)
  n = 0.0141
FEATURE [App::DocumentObjectGroupPython] C_element076  label="C_element : 0.072"  # scripted group (container) (typed FeaturePython)
  n = 0.072261
FEATURE [App::DocumentObjectGroupPython] N_element035  label="N_element : 0.019"  # scripted group (container) (typed FeaturePython)
  n = 0.01932
FEATURE [App::DocumentObjectGroupPython] O_element075  label="O_element : 0.066"  # scripted group (container) (typed FeaturePython)
  n = 0.066101
FEATURE [App::DocumentObjectGroupPython] S_element019  label="S_element : 0.020"  # scripted group (container) (typed FeaturePython)
  n = 0.00189
FEATURE [App::DocumentObjectGroupPython] Br_element004  label="Br_element : 0.349"  # scripted group (container) (typed FeaturePython)
  n = 0.349103
FEATURE [App::DocumentObjectGroupPython] Ag_element001  label="Ag_element : 0.474"  # scripted group (container) (typed FeaturePython)
  n = 0.474105
FEATURE [App::DocumentObjectGroupPython] I_element005  label="I_element : 0.003"  # scripted group (container) (typed FeaturePython)
  n = 0.00312
FEATURE [App::DocumentObjectGroupPython] G4_PHOTO_EMULSION  # scripted group (container) (typed FeaturePython)
  Dunit = g/cm3
  Dvalue = 3.815
  Group = -> [H_element070,C_element076,N_element035,O_element075,S_element019,Br_element004,Ag_element001,I_element005]
  conduct = 2
  density = 1
  expand = 3
  formula = G4_PHOTO_EMULSION
  name = G4_PHOTO_EMULSION
  specific = 4
FEATURE [App::DocumentObjectGroupPython] C_element077  label="C_element : 9"  # scripted group (container) (typed FeaturePython)
  n = 9
  ref = C_element
FEATURE [App::DocumentObjectGroupPython] H_element071  label="H_element : 033"  # scripted group (container) (typed FeaturePython)
  n = 10
  ref = H_element
FEATURE [App::DocumentObjectGroupPython] G4_PLASTIC_SC_VINYLTOLUENE  # scripted group (container) (typed FeaturePython)
  Dunit = g/cm3
  Dvalue = 1.032
  Group = -> [C_element077,H_element071]
  conduct = 2
  density = 1
  expand = 3
  formula = G4_PLASTIC_SC_VINYLTOLUENE
  name = G4_PLASTIC_SC_VINYLTOLUENE
  specific = 4
FEATURE [App::DocumentObjectGroupPython] Pu_element001  label="Pu_element : 1"  # scripted group (container) (typed FeaturePython)
  n = 1
  ref = Pu_element
FEATURE [App::DocumentObjectGroupPython] O_element076  label="O_element : 037"  # scripted group (container) (typed FeaturePython)
  n = 2
  ref = O_element
FEATURE [App::DocumentObjectGroupPython] G4_PLUTONIUM_DIOXIDE  # scripted group (container) (typed FeaturePython)
  Dunit = g/cm3
  Dvalue = 11.46
  Group = -> [Pu_element001,O_element076]
  conduct = 2
  density = 1
  expand = 3
  formula = G4_PLUTONIUM_DIOXIDE
  name = G4_PLUTONIUM_DIOXIDE
  specific = 4
FEATURE [App::DocumentObjectGroupPython] C_element078  label="C_element : 037"  # scripted group (container) (typed FeaturePython)
  n = 3
  ref = C_element
FEATURE [App::DocumentObjectGroupPython] H_element072  label="H_element : 034"  # scripted group (container) (typed FeaturePython)
  n = 3
  ref = H_element
FEATURE [App::DocumentObjectGroupPython] N_element036  label="N_element : 015"  # scripted group (container) (typed FeaturePython)
  n = 1
  ref = N_element
FEATURE [App::DocumentObjectGroupPython] G4_POLYACRYLONITRILE  # scripted group (container) (typed FeaturePython)
  Dunit = g/cm3
  Dvalue = 1.17
  Group = -> [C_element078,H_element072,N_element036]
  conduct = 2
  density = 1
  expand = 3
  formula = G4_POLYACRYLONITRILE
  name = G4_POLYACRYLONITRILE
  specific = 4
FEATURE [App::DocumentObjectGroupPython] C_element079  label="C_element : 16"  # scripted group (container) (typed FeaturePython)
  n = 16
  ref = C_element
FEATURE [App::DocumentObjectGroupPython] H_element073  label="H_element : 035"  # scripted group (container) (typed FeaturePython)
  n = 14
  ref = H_element
FEATURE [App::DocumentObjectGroupPython] O_element077  label="O_element : 038"  # scripted group (container) (typed FeaturePython)
  n = 3
  ref = O_element
FEATURE [App::DocumentObjectGroupPython] G4_POLYCARBONATE  # scripted group (container) (typed FeaturePython)
  Dunit = g/cm3
  Dvalue = 1.2
  Group = -> [C_element079,H_element073,O_element077]
  conduct = 2
  density = 1
  expand = 3
  formula = G4_POLYCARBONATE
  name = G4_POLYCARBONATE
  specific = 4
FEATURE [App::DocumentObjectGroupPython] C_element080  label="C_element : 038"  # scripted group (container) (typed FeaturePython)
  n = 8
  ref = C_element
FEATURE [App::DocumentObjectGroupPython] H_element074  label="H_element : 036"  # scripted group (container) (typed FeaturePython)
  n = 7
  ref = H_element
FEATURE [App::DocumentObjectGroupPython] Cl_element017  label="Cl_element : 007"  # scripted group (container) (typed FeaturePython)
  n = 1
  ref = Cl_element
FEATURE [App::DocumentObjectGroupPython] G4_POLYCHLOROSTYRENE  # scripted group (container) (typed FeaturePython)
  Dunit = g/cm3
  Dvalue = 1.3
  Group = -> [C_element080,H_element074,Cl_element017]
  conduct = 2
  density = 1
  expand = 3
  formula = G4_POLYCHLOROSTYRENE
  name = G4_POLYCHLOROSTYRENE
  specific = 4
FEATURE [App::DocumentObjectGroupPython] C_element081  label="C_element : 039"  # scripted group (container) (typed FeaturePython)
  n = 1
  ref = C_element
FEATURE [App::DocumentObjectGroupPython] H_element075  label="H_element : 037"  # scripted group (container) (typed FeaturePython)
  n = 2
  ref = H_element
FEATURE [App::DocumentObjectGroupPython] G4_POLYETHYLENE  # scripted group (container) (typed FeaturePython)
  Dunit = g/cm3
  Dvalue = 0.94
  Group = -> [C_element081,H_element075]
  conduct = 2
  density = 1
  expand = 3
  formula = G4_POLYETHYLENE
  name = G4_POLYETHYLENE
  specific = 4
FEATURE [App::DocumentObjectGroupPython] C_element082  label="C_element : 040"  # scripted group (container) (typed FeaturePython)
  n = 10
  ref = C_element
FEATURE [App::DocumentObjectGroupPython] H_element076  label="H_element : 038"  # scripted group (container) (typed FeaturePython)
  n = 8
  ref = H_element
FEATURE [App::DocumentObjectGroupPython] O_element078  label="O_element : 039"  # scripted group (container) (typed FeaturePython)
  n = 4
  ref = O_element
FEATURE [App::DocumentObjectGroupPython] G4_MYLAR  # scripted group (container) (typed FeaturePython)
  Dunit = g/cm3
  Dvalue = 1.4
  Group = -> [C_element082,H_element076,O_element078]
  conduct = 2
  density = 1
  expand = 3
  formula = G4_MYLAR
  name = G4_MYLAR
  specific = 4
FEATURE [App::DocumentObjectGroupPython] C_element083  label="C_element : 041"  # scripted group (container) (typed FeaturePython)
  n = 5
  ref = C_element
FEATURE [App::DocumentObjectGroupPython] H_element077  label="H_element : 039"  # scripted group (container) (typed FeaturePython)
  n = 8
  ref = H_element
FEATURE [App::DocumentObjectGroupPython] O_element079  label="O_element : 040"  # scripted group (container) (typed FeaturePython)
  n = 2
  ref = O_element
FEATURE [App::DocumentObjectGroupPython] G4_PLEXIGLASS  # scripted group (container) (typed FeaturePython)
  Dunit = g/cm3
  Dvalue = 1.19
  Group = -> [C_element083,H_element077,O_element079]
  conduct = 2
  density = 1
  expand = 3
  formula = G4_PLEXIGLASS
  name = G4_PLEXIGLASS
  specific = 4
FEATURE [App::DocumentObjectGroupPython] C_element084  label="C_element : 042"  # scripted group (container) (typed FeaturePython)
  n = 1
  ref = C_element
FEATURE [App::DocumentObjectGroupPython] H_element078  label="H_element : 040"  # scripted group (container) (typed FeaturePython)
  n = 2
  ref = H_element
FEATURE [App::DocumentObjectGroupPython] O_element080  label="O_element : 041"  # scripted group (container) (typed FeaturePython)
  n = 1
  ref = O_element
FEATURE [App::DocumentObjectGroupPython] G4_POLYOXYMETHYLENE  # scripted group (container) (typed FeaturePython)
  Dunit = g/cm3
  Dvalue = 1.425
  Group = -> [C_element084,H_element078,O_element080]
  conduct = 2
  density = 1
  expand = 3
  formula = G4_POLYOXYMETHYLENE
  name = G4_POLYOXYMETHYLENE
  specific = 4
FEATURE [App::DocumentObjectGroupPython] C_element085  label="C_element : 043"  # scripted group (container) (typed FeaturePython)
  n = 2
  ref = C_element
FEATURE [App::DocumentObjectGroupPython] H_element079  label="H_element : 041"  # scripted group (container) (typed FeaturePython)
  n = 4
  ref = H_element
FEATURE [App::DocumentObjectGroupPython] G4_POLYPROPYLENE  # scripted group (container) (typed FeaturePython)
  Dunit = g/cm3
  Dvalue = 0.9
  Group = -> [C_element085,H_element079]
  conduct = 2
  density = 1
  expand = 3
  formula = G4_POLYPROPYLENE
  name = G4_POLYPROPYLENE
  specific = 4
FEATURE [App::DocumentObjectGroupPython] C_element086  label="C_element : 044"  # scripted group (container) (typed FeaturePython)
  n = 8
  ref = C_element
FEATURE [App::DocumentObjectGroupPython] H_element080  label="H_element : 042"  # scripted group (container) (typed FeaturePython)
  n = 8
  ref = H_element
FEATURE [App::DocumentObjectGroupPython] G4_POLYSTYRENE  # scripted group (container) (typed FeaturePython)
  Dunit = g/cm3
  Dvalue = 1.06
  Group = -> [C_element086,H_element080]
  conduct = 2
  density = 1
  expand = 3
  formula = G4_POLYSTYRENE
  name = G4_POLYSTYRENE
  specific = 4
FEATURE [App::DocumentObjectGroupPython] C_element087  label="C_element : 045"  # scripted group (container) (typed FeaturePython)
  n = 2
  ref = C_element
FEATURE [App::DocumentObjectGroupPython] F_element014  label="F_element : 4"  # scripted group (container) (typed FeaturePython)
  n = 4
  ref = F_element
FEATURE [App::DocumentObjectGroupPython] G4_TEFLON  # scripted group (container) (typed FeaturePython)
  Dunit = g/cm3
  Dvalue = 2.2
  Group = -> [C_element087,F_element014]
  conduct = 2
  density = 1
  expand = 3
  formula = G4_TEFLON
  name = G4_TEFLON
  specific = 4
FEATURE [App::DocumentObjectGroupPython] C_element088  label="C_element : 046"  # scripted group (container) (typed FeaturePython)
  n = 2
  ref = C_element
FEATURE [App::DocumentObjectGroupPython] F_element015  label="F_element : 006"  # scripted group (container) (typed FeaturePython)
  n = 3
  ref = F_element
FEATURE [App::DocumentObjectGroupPython] Cl_element018  label="Cl_element : 008"  # scripted group (container) (typed FeaturePython)
  n = 1
  ref = Cl_element
FEATURE [App::DocumentObjectGroupPython] G4_POLYTRIFLUOROCHLOROETHYLENE  # scripted group (container) (typed FeaturePython)
  Dunit = g/cm3
  Dvalue = 2.1
  Group = -> [C_element088,F_element015,Cl_element018]
  conduct = 2
  density = 1
  expand = 3
  formula = G4_POLYTRIFLUOROCHLOROETHYLENE
  name = G4_POLYTRIFLUOROCHLOROETHYLENE
  specific = 4
FEATURE [App::DocumentObjectGroupPython] C_element089  label="C_element : 047"  # scripted group (container) (typed FeaturePython)
  n = 4
  ref = C_element
FEATURE [App::DocumentObjectGroupPython] H_element081  label="H_element : 043"  # scripted group (container) (typed FeaturePython)
  n = 6
  ref = H_element
FEATURE [App::DocumentObjectGroupPython] O_element081  label="O_element : 042"  # scripted group (container) (typed FeaturePython)
  n = 2
  ref = O_element
FEATURE [App::DocumentObjectGroupPython] G4_POLYVINYL_ACETATE  # scripted group (container) (typed FeaturePython)
  Dunit = g/cm3
  Dvalue = 1.19
  Group = -> [C_element089,H_element081,O_element081]
  conduct = 2
  density = 1
  expand = 3
  formula = G4_POLYVINYL_ACETATE
  name = G4_POLYVINYL_ACETATE
  specific = 4
FEATURE [App::DocumentObjectGroupPython] C_element090  label="C_element : 048"  # scripted group (container) (typed FeaturePython)
  n = 2
  ref = C_element
FEATURE [App::DocumentObjectGroupPython] H_element082  label="H_element : 044"  # scripted group (container) (typed FeaturePython)
  n = 4
  ref = H_element
FEATURE [App::DocumentObjectGroupPython] O_element082  label="O_element : 043"  # scripted group (container) (typed FeaturePython)
  n = 1
  ref = O_element
FEATURE [App::DocumentObjectGroupPython] G4_POLYVINYL_ALCOHOL  # scripted group (container) (typed FeaturePython)
  Dunit = g/cm3
  Dvalue = 1.3
  Group = -> [C_element090,H_element082,O_element082]
  conduct = 2
  density = 1
  expand = 3
  formula = G4_POLYVINYL_ALCOHOL
  name = G4_POLYVINYL_ALCOHOL
  specific = 4
FEATURE [App::DocumentObjectGroupPython] C_element091  label="C_element : 049"  # scripted group (container) (typed FeaturePython)
  n = 8
  ref = C_element
FEATURE [App::DocumentObjectGroupPython] H_element083  label="H_element : 045"  # scripted group (container) (typed FeaturePython)
  n = 14
  ref = H_element
FEATURE [App::DocumentObjectGroupPython] O_element083  label="O_element : 044"  # scripted group (container) (typed FeaturePython)
  n = 2
  ref = O_element
FEATURE [App::DocumentObjectGroupPython] G4_POLYVINYL_BUTYRAL  # scripted group (container) (typed FeaturePython)
  Dunit = g/cm3
  Dvalue = 1.12
  Group = -> [C_element091,H_element083,O_element083]
  conduct = 2
  density = 1
  expand = 3
  formula = G4_POLYVINYL_BUTYRAL
  name = G4_POLYVINYL_BUTYRAL
  specific = 4
FEATURE [App::DocumentObjectGroupPython] C_element092  label="C_element : 050"  # scripted group (container) (typed FeaturePython)
  n = 2
  ref = C_element
FEATURE [App::DocumentObjectGroupPython] H_element084  label="H_element : 046"  # scripted group (container) (typed FeaturePython)
  n = 3
  ref = H_element
FEATURE [App::DocumentObjectGroupPython] Cl_element019  label="Cl_element : 009"  # scripted group (container) (typed FeaturePython)
  n = 1
  ref = Cl_element
FEATURE [App::DocumentObjectGroupPython] G4_POLYVINYL_CHLORIDE  # scripted group (container) (typed FeaturePython)
  Dunit = g/cm3
  Dvalue = 1.3
  Group = -> [C_element092,H_element084,Cl_element019]
  conduct = 2
  density = 1
  expand = 3
  formula = G4_POLYVINYL_CHLORIDE
  name = G4_POLYVINYL_CHLORIDE
  specific = 4
FEATURE [App::DocumentObjectGroupPython] C_element093  label="C_element : 051"  # scripted group (container) (typed FeaturePython)
  n = 2
  ref = C_element
FEATURE [App::DocumentObjectGroupPython] H_element085  label="H_element : 047"  # scripted group (container) (typed FeaturePython)
  n = 2
  ref = H_element
FEATURE [App::DocumentObjectGroupPython] Cl_element020  label="Cl_element : 010"  # scripted group (container) (typed FeaturePython)
  n = 2
  ref = Cl_element
FEATURE [App::DocumentObjectGroupPython] G4_POLYVINYLIDENE_CHLORIDE  # scripted group (container) (typed FeaturePython)
  Dunit = g/cm3
  Dvalue = 1.7
  Group = -> [C_element093,H_element085,Cl_element020]
  conduct = 2
  density = 1
  expand = 3
  formula = G4_POLYVINYLIDENE_CHLORIDE
  name = G4_POLYVINYLIDENE_CHLORIDE
  specific = 4
FEATURE [App::DocumentObjectGroupPython] C_element094  label="C_element : 052"  # scripted group (container) (typed FeaturePython)
  n = 2
  ref = C_element
FEATURE [App::DocumentObjectGroupPython] H_element086  label="H_element : 048"  # scripted group (container) (typed FeaturePython)
  n = 2
  ref = H_element
FEATURE [App::DocumentObjectGroupPython] F_element016  label="F_element : 007"  # scripted group (container) (typed FeaturePython)
  n = 2
  ref = F_element
FEATURE [App::DocumentObjectGroupPython] G4_POLYVINYLIDENE_FLUORIDE  # scripted group (container) (typed FeaturePython)
  Dunit = g/cm3
  Dvalue = 1.76
  Group = -> [C_element094,H_element086,F_element016]
  conduct = 2
  density = 1
  expand = 3
  formula = G4_POLYVINYLIDENE_FLUORIDE
  name = G4_POLYVINYLIDENE_FLUORIDE
  specific = 4
FEATURE [App::DocumentObjectGroupPython] C_element095  label="C_element : 053"  # scripted group (container) (typed FeaturePython)
  n = 6
  ref = C_element
FEATURE [App::DocumentObjectGroupPython] H_element087  label="H_element : 9"  # scripted group (container) (typed FeaturePython)
  n = 9
  ref = H_element
FEATURE [App::DocumentObjectGroupPython] N_element037  label="N_element : 016"  # scripted group (container) (typed FeaturePython)
  n = 1
  ref = N_element
FEATURE [App::DocumentObjectGroupPython] O_element084  label="O_element : 045"  # scripted group (container) (typed FeaturePython)
  n = 1
  ref = O_element
FEATURE [App::DocumentObjectGroupPython] G4_POLYVINYL_PYRROLIDONE  # scripted group (container) (typed FeaturePython)
  Dunit = g/cm3
  Dvalue = 1.25
  Group = -> [C_element095,H_element087,N_element037,O_element084]
  conduct = 2
  density = 1
  expand = 3
  formula = G4_POLYVINYL_PYRROLIDONE
  name = G4_POLYVINYL_PYRROLIDONE
  specific = 4
FEATURE [App::DocumentObjectGroupPython] K_element008  label="K_element : 1"  # scripted group (container) (typed FeaturePython)
  n = 1
  ref = K_element
FEATURE [App::DocumentObjectGroupPython] I_element006  label="I_element : 003"  # scripted group (container) (typed FeaturePython)
  n = 1
  ref = I_element
FEATURE [App::DocumentObjectGroupPython] G4_POTASSIUM_IODIDE  # scripted group (container) (typed FeaturePython)
  Dunit = g/cm3
  Dvalue = 3.13
  Group = -> [K_element008,I_element006]
  conduct = 2
  density = 1
  expand = 3
  formula = G4_POTASSIUM_IODIDE
  name = G4_POTASSIUM_IODIDE
  specific = 4
FEATURE [App::DocumentObjectGroupPython] K_element009  label="K_element : 2"  # scripted group (container) (typed FeaturePython)
  n = 2
  ref = K_element
FEATURE [App::DocumentObjectGroupPython] O_element085  label="O_element : 046"  # scripted group (container) (typed FeaturePython)
  n = 1
  ref = O_element
FEATURE [App::DocumentObjectGroupPython] G4_POTASSIUM_OXIDE  # scripted group (container) (typed FeaturePython)
  Dunit = g/cm3
  Dvalue = 2.32
  Group = -> [K_element009,O_element085]
  conduct = 2
  density = 1
  expand = 3
  formula = G4_POTASSIUM_OXIDE
  name = G4_POTASSIUM_OXIDE
  specific = 4
FEATURE [App::DocumentObjectGroupPython] C_element096  label="C_element : 054"  # scripted group (container) (typed FeaturePython)
  n = 3
  ref = C_element
FEATURE [App::DocumentObjectGroupPython] H_element088  label="H_element : 049"  # scripted group (container) (typed FeaturePython)
  n = 8
  ref = H_element
FEATURE [App::DocumentObjectGroupPython] G4_PROPANE  # scripted group (container) (typed FeaturePython)
  Dunit = g/cm3
  Dvalue = 0.00187939
  Group = -> [C_element096,H_element088]
  conduct = 2
  density = 1
  expand = 3
  formula = G4_PROPANE
  name = G4_PROPANE
  specific = 4
FEATURE [App::DocumentObjectGroupPython] C_element097  label="C_element : 055"  # scripted group (container) (typed FeaturePython)
  n = 3
  ref = C_element
FEATURE [App::DocumentObjectGroupPython] H_element089  label="H_element : 050"  # scripted group (container) (typed FeaturePython)
  n = 8
  ref = H_element
FEATURE [App::DocumentObjectGroupPython] G4_lPROPANE  # scripted group (container) (typed FeaturePython)
  Dunit = g/cm3
  Dvalue = 0.43
  Group = -> [C_element097,H_element089]
  conduct = 2
  density = 1
  expand = 3
  formula = G4_lPROPANE
  name = G4_lPROPANE
  specific = 4
FEATURE [App::DocumentObjectGroupPython] C_element098  label="C_element : 056"  # scripted group (container) (typed FeaturePython)
  n = 3
  ref = C_element
FEATURE [App::DocumentObjectGroupPython] H_element090  label="H_element : 051"  # scripted group (container) (typed FeaturePython)
  n = 8
  ref = H_element
FEATURE [App::DocumentObjectGroupPython] O_element086  label="O_element : 047"  # scripted group (container) (typed FeaturePython)
  n = 1
  ref = O_element
FEATURE [App::DocumentObjectGroupPython] G4_N_PROPYL_ALCOHOL  label="G4_N-PROPYL_ALCOHOL"  # scripted group (container) (typed FeaturePython)
  Dunit = g/cm3
  Dvalue = 0.8035
  Group = -> [C_element098,H_element090,O_element086]
  conduct = 2
  density = 1
  expand = 3
  formula = G4_N-PROPYL_ALCOHOL
  name = G4_N-PROPYL_ALCOHOL
  specific = 4
FEATURE [App::DocumentObjectGroupPython] C_element099  label="C_element : 057"  # scripted group (container) (typed FeaturePython)
  n = 5
  ref = C_element
FEATURE [App::DocumentObjectGroupPython] H_element091  label="H_element : 052"  # scripted group (container) (typed FeaturePython)
  n = 5
  ref = H_element
FEATURE [App::DocumentObjectGroupPython] N_element038  label="N_element : 017"  # scripted group (container) (typed FeaturePython)
  n = 1
  ref = N_element
FEATURE [App::DocumentObjectGroupPython] G4_PYRIDINE  # scripted group (container) (typed FeaturePython)
  Dunit = g/cm3
  Dvalue = 0.9819
  Group = -> [C_element099,H_element091,N_element038]
  conduct = 2
  density = 1
  expand = 3
  formula = G4_PYRIDINE
  name = G4_PYRIDINE
  specific = 4
FEATURE [App::DocumentObjectGroupPython] H_element092  label="H_element : 0.144"  # scripted group (container) (typed FeaturePython)
  n = 0.143711
FEATURE [App::DocumentObjectGroupPython] C_element100  label="C_element : 0.856"  # scripted group (container) (typed FeaturePython)
  n = 0.856289
FEATURE [App::DocumentObjectGroupPython] G4_RUBBER_BUTYL  # scripted group (container) (typed FeaturePython)
  Dunit = g/cm3
  Dvalue = 0.92
  Group = -> [H_element092,C_element100]
  conduct = 2
  density = 1
  expand = 3
  formula = G4_RUBBER_BUTYL
  name = G4_RUBBER_BUTYL
  specific = 4
FEATURE [App::DocumentObjectGroupPython] H_element093  label="H_element : 0.118"  # scripted group (container) (typed FeaturePython)
  n = 0.118371
FEATURE [App::DocumentObjectGroupPython] C_element101  label="C_element : 0.882"  # scripted group (container) (typed FeaturePython)
  n = 0.881629
FEATURE [App::DocumentObjectGroupPython] G4_RUBBER_NATURAL  # scripted group (container) (typed FeaturePython)
  Dunit = g/cm3
  Dvalue = 0.92
  Group = -> [H_element093,C_element101]
  conduct = 2
  density = 1
  expand = 3
  formula = G4_RUBBER_NATURAL
  name = G4_RUBBER_NATURAL
  specific = 4
FEATURE [App::DocumentObjectGroupPython] H_element094  label="H_element : 0.145"  # scripted group (container) (typed FeaturePython)
  n = 0.05692
FEATURE [App::DocumentObjectGroupPython] C_element102  label="C_element : 0.543"  # scripted group (container) (typed FeaturePython)
  n = 0.542646
FEATURE [App::DocumentObjectGroupPython] Cl_element021  label="Cl_element : 0.400"  # scripted group (container) (typed FeaturePython)
  n = 0.400434
FEATURE [App::DocumentObjectGroupPython] G4_RUBBER_NEOPRENE  # scripted group (container) (typed FeaturePython)
  Dunit = g/cm3
  Dvalue = 1.23
  Group = -> [H_element094,C_element102,Cl_element021]
  conduct = 2
  density = 1
  expand = 3
  formula = G4_RUBBER_NEOPRENE
  name = G4_RUBBER_NEOPRENE
  specific = 4
FEATURE [App::DocumentObjectGroupPython] Si_element006  label="Si_element : 1"  # scripted group (container) (typed FeaturePython)
  n = 1
  ref = Si_element
FEATURE [App::DocumentObjectGroupPython] O_element087  label="O_element : 048"  # scripted group (container) (typed FeaturePython)
  n = 2
  ref = O_element
FEATURE [App::DocumentObjectGroupPython] G4_SILICON_DIOXIDE  # scripted group (container) (typed FeaturePython)
  Dunit = g/cm3
  Dvalue = 2.32
  Group = -> [Si_element006,O_element087]
  conduct = 2
  density = 1
  expand = 3
  formula = G4_SILICON_DIOXIDE
  name = G4_SILICON_DIOXIDE
  specific = 4
FEATURE [App::DocumentObjectGroupPython] Ag_element002  label="Ag_element : 1"  # scripted group (container) (typed FeaturePython)
  n = 1
  ref = Ag_element
FEATURE [App::DocumentObjectGroupPython] Br_element005  label="Br_element : 003"  # scripted group (container) (typed FeaturePython)
  n = 1
  ref = Br_element
FEATURE [App::DocumentObjectGroupPython] G4_SILVER_BROMIDE  # scripted group (container) (typed FeaturePython)
  Dunit = g/cm3
  Dvalue = 6.473
  Group = -> [Ag_element002,Br_element005]
  conduct = 2
  density = 1
  expand = 3
  formula = G4_SILVER_BROMIDE
  name = G4_SILVER_BROMIDE
  specific = 4
FEATURE [App::DocumentObjectGroupPython] Ag_element003  label="Ag_element : 002"  # scripted group (container) (typed FeaturePython)
  n = 1
  ref = Ag_element
FEATURE [App::DocumentObjectGroupPython] Cl_element022  label="Cl_element : 011"  # scripted group (container) (typed FeaturePython)
  n = 1
  ref = Cl_element
FEATURE [App::DocumentObjectGroupPython] G4_SILVER_CHLORIDE  # scripted group (container) (typed FeaturePython)
  Dunit = g/cm3
  Dvalue = 5.56
  Group = -> [Ag_element003,Cl_element022]
  conduct = 2
  density = 1
  expand = 3
  formula = G4_SILVER_CHLORIDE
  name = G4_SILVER_CHLORIDE
  specific = 4
FEATURE [App::DocumentObjectGroupPython] Br_element006  label="Br_element : 0.423"  # scripted group (container) (typed FeaturePython)
  n = 0.422895
FEATURE [App::DocumentObjectGroupPython] Ag_element004  label="Ag_element : 0.574"  # scripted group (container) (typed FeaturePython)
  n = 0.573748
FEATURE [App::DocumentObjectGroupPython] I_element007  label="I_element : 0.649"  # scripted group (container) (typed FeaturePython)
  n = 0.003357
FEATURE [App::DocumentObjectGroupPython] G4_SILVER_HALIDES  # scripted group (container) (typed FeaturePython)
  Dunit = g/cm3
  Dvalue = 6.47
  Group = -> [Br_element006,Ag_element004,I_element007]
  conduct = 2
  density = 1
  expand = 3
  formula = G4_SILVER_HALIDES
  name = G4_SILVER_HALIDES
  specific = 4
FEATURE [App::DocumentObjectGroupPython] Ag_element005  label="Ag_element : 003"  # scripted group (container) (typed FeaturePython)
  n = 1
  ref = Ag_element
FEATURE [App::DocumentObjectGroupPython] I_element008  label="I_element : 004"  # scripted group (container) (typed FeaturePython)
  n = 1
  ref = I_element
FEATURE [App::DocumentObjectGroupPython] G4_SILVER_IODIDE  # scripted group (container) (typed FeaturePython)
  Dunit = g/cm3
  Dvalue = 6.01
  Group = -> [Ag_element005,I_element008]
  conduct = 2
  density = 1
  expand = 3
  formula = G4_SILVER_IODIDE
  name = G4_SILVER_IODIDE
  specific = 4
FEATURE [App::DocumentObjectGroupPython] H_element095  label="H_element : 0.100"  # scripted group (container) (typed FeaturePython)
  n = 0.1
FEATURE [App::DocumentObjectGroupPython] C_element103  label="C_element : 0.204"  # scripted group (container) (typed FeaturePython)
  n = 0.204
FEATURE [App::DocumentObjectGroupPython] N_element039  label="N_element : 0.759"  # scripted group (container) (typed FeaturePython)
  n = 0.042
FEATURE [App::DocumentObjectGroupPython] O_element088  label="O_element : 0.645"  # scripted group (container) (typed FeaturePython)
  n = 0.645
FEATURE [App::DocumentObjectGroupPython] Na_element013  label="Na_element : 0.100"  # scripted group (container) (typed FeaturePython)
  n = 0.002
FEATURE [App::DocumentObjectGroupPython] P_element009  label="P_element : 0.107"  # scripted group (container) (typed FeaturePython)
  n = 0.001
FEATURE [App::DocumentObjectGroupPython] S_element020  label="S_element : 0.021"  # scripted group (container) (typed FeaturePython)
  n = 0.002
FEATURE [App::DocumentObjectGroupPython] Cl_element023  label="Cl_element : 0.590"  # scripted group (container) (typed FeaturePython)
  n = 0.003
FEATURE [App::DocumentObjectGroupPython] K_element010  label="K_element : 0.001"  # scripted group (container) (typed FeaturePython)
  n = 0.001
FEATURE [App::DocumentObjectGroupPython] G4_SKIN_ICRP  # scripted group (container) (typed FeaturePython)
  Dunit = g/cm3
  Dvalue = 1.09
  Group = -> [H_element095,C_element103,N_element039,O_element088,Na_element013,P_element009,S_element020,Cl_element023,K_element010]
  conduct = 2
  density = 1
  expand = 3
  formula = G4_SKIN_ICRP
  name = G4_SKIN_ICRP
  specific = 4
FEATURE [App::DocumentObjectGroupPython] Na_element014  label="Na_element : 2"  # scripted group (container) (typed FeaturePython)
  n = 2
  ref = Na_element
FEATURE [App::DocumentObjectGroupPython] C_element104  label="C_element : 058"  # scripted group (container) (typed FeaturePython)
  n = 1
  ref = C_element
FEATURE [App::DocumentObjectGroupPython] O_element089  label="O_element : 049"  # scripted group (container) (typed FeaturePython)
  n = 3
  ref = O_element
FEATURE [App::DocumentObjectGroupPython] G4_SODIUM_CARBONATE  # scripted group (container) (typed FeaturePython)
  Dunit = g/cm3
  Dvalue = 2.532
  Group = -> [Na_element014,C_element104,O_element089]
  conduct = 2
  density = 1
  expand = 3
  formula = G4_SODIUM_CARBONATE
  name = G4_SODIUM_CARBONATE
  specific = 4
FEATURE [App::DocumentObjectGroupPython] Na_element015  label="Na_element : 1"  # scripted group (container) (typed FeaturePython)
  n = 1
  ref = Na_element
FEATURE [App::DocumentObjectGroupPython] I_element009  label="I_element : 005"  # scripted group (container) (typed FeaturePython)
  n = 1
  ref = I_element
FEATURE [App::DocumentObjectGroupPython] G4_SODIUM_IODIDE  # scripted group (container) (typed FeaturePython)
  Dunit = g/cm3
  Dvalue = 3.667
  Group = -> [Na_element015,I_element009]
  conduct = 2
  density = 1
  expand = 3
  formula = G4_SODIUM_IODIDE
  name = G4_SODIUM_IODIDE
  specific = 4
FEATURE [App::DocumentObjectGroupPython] Na_element016  label="Na_element : 003"  # scripted group (container) (typed FeaturePython)
  n = 2
  ref = Na_element
FEATURE [App::DocumentObjectGroupPython] O_element090  label="O_element : 050"  # scripted group (container) (typed FeaturePython)
  n = 1
  ref = O_element
FEATURE [App::DocumentObjectGroupPython] G4_SODIUM_MONOXIDE  # scripted group (container) (typed FeaturePython)
  Dunit = g/cm3
  Dvalue = 2.27
  Group = -> [Na_element016,O_element090]
  conduct = 2
  density = 1
  expand = 3
  formula = G4_SODIUM_MONOXIDE
  name = G4_SODIUM_MONOXIDE
  specific = 4
FEATURE [App::DocumentObjectGroupPython] Na_element017  label="Na_element : 004"  # scripted group (container) (typed FeaturePython)
  n = 1
  ref = Na_element
FEATURE [App::DocumentObjectGroupPython] N_element040  label="N_element : 018"  # scripted group (container) (typed FeaturePython)
  n = 1
  ref = N_element
FEATURE [App::DocumentObjectGroupPython] O_element091  label="O_element : 051"  # scripted group (container) (typed FeaturePython)
  n = 3
  ref = O_element
FEATURE [App::DocumentObjectGroupPython] G4_SODIUM_NITRATE  # scripted group (container) (typed FeaturePython)
  Dunit = g/cm3
  Dvalue = 2.261
  Group = -> [Na_element017,N_element040,O_element091]
  conduct = 2
  density = 1
  expand = 3
  formula = G4_SODIUM_NITRATE
  name = G4_SODIUM_NITRATE
  specific = 4
FEATURE [App::DocumentObjectGroupPython] C_element105  label="C_element : 059"  # scripted group (container) (typed FeaturePython)
  n = 14
  ref = C_element
FEATURE [App::DocumentObjectGroupPython] H_element096  label="H_element : 053"  # scripted group (container) (typed FeaturePython)
  n = 12
  ref = H_element
FEATURE [App::DocumentObjectGroupPython] G4_STILBENE  # scripted group (container) (typed FeaturePython)
  Dunit = g/cm3
  Dvalue = 0.9707
  Group = -> [C_element105,H_element096]
  conduct = 2
  density = 1
  expand = 3
  formula = G4_STILBENE
  name = G4_STILBENE
  specific = 4
FEATURE [App::DocumentObjectGroupPython] C_element106  label="C_element : 12"  # scripted group (container) (typed FeaturePython)
  n = 12
  ref = C_element
FEATURE [App::DocumentObjectGroupPython] H_element097  label="H_element : 22"  # scripted group (container) (typed FeaturePython)
  n = 22
  ref = H_element
FEATURE [App::DocumentObjectGroupPython] O_element092  label="O_element : 11"  # scripted group (container) (typed FeaturePython)
  n = 11
  ref = O_element
FEATURE [App::DocumentObjectGroupPython] G4_SUCROSE  # scripted group (container) (typed FeaturePython)
  Dunit = g/cm3
  Dvalue = 1.5805
  Group = -> [C_element106,H_element097,O_element092]
  conduct = 2
  density = 1
  expand = 3
  formula = G4_SUCROSE
  name = G4_SUCROSE
  specific = 4
FEATURE [App::DocumentObjectGroupPython] C_element107  label="C_element : 18"  # scripted group (container) (typed FeaturePython)
  n = 18
  ref = C_element
FEATURE [App::DocumentObjectGroupPython] H_element098  label="H_element : 054"  # scripted group (container) (typed FeaturePython)
  n = 14
  ref = H_element
FEATURE [App::DocumentObjectGroupPython] G4_TERPHENYL  # scripted group (container) (typed FeaturePython)
  Dunit = g/cm3
  Dvalue = 1.24
  Group = -> [C_element107,H_element098]
  conduct = 2
  density = 1
  expand = 3
  formula = G4_TERPHENYL
  name = G4_TERPHENYL
  specific = 4
FEATURE [App::DocumentObjectGroupPython] H_element099  label="H_element : 0.146"  # scripted group (container) (typed FeaturePython)
  n = 0.106
FEATURE [App::DocumentObjectGroupPython] C_element108  label="C_element : 0.883"  # scripted group (container) (typed FeaturePython)
  n = 0.099
FEATURE [App::DocumentObjectGroupPython] N_element041  label="N_element : 0.020"  # scripted group (container) (typed FeaturePython)
  n = 0.02
FEATURE [App::DocumentObjectGroupPython] O_element093  label="O_element : 0.766"  # scripted group (container) (typed FeaturePython)
  n = 0.766
FEATURE [App::DocumentObjectGroupPython] Na_element018  label="Na_element : 0.101"  # scripted group (container) (typed FeaturePython)
  n = 0.002
FEATURE [App::DocumentObjectGroupPython] P_element010  label="P_element : 0.108"  # scripted group (container) (typed FeaturePython)
  n = 0.001
FEATURE [App::DocumentObjectGroupPython] S_element021  label="S_element : 0.022"  # scripted group (container) (typed FeaturePython)
  n = 0.002
FEATURE [App::DocumentObjectGroupPython] Cl_element024  label="Cl_element : 0.002"  # scripted group (container) (typed FeaturePython)
  n = 0.002
FEATURE [App::DocumentObjectGroupPython] K_element011  label="K_element : 0.017"  # scripted group (container) (typed FeaturePython)
  n = 0.002
FEATURE [App::DocumentObjectGroupPython] G4_TESTIS_ICRP  # scripted group (container) (typed FeaturePython)
  Dunit = g/cm3
  Dvalue = 1.04
  Group = -> [H_element099,C_element108,N_element041,O_element093,Na_element018,P_element010,S_element021,Cl_element024,K_element011]
  conduct = 2
  density = 1
  expand = 3
  formula = G4_TESTIS_ICRP
  name = G4_TESTIS_ICRP
  specific = 4
FEATURE [App::DocumentObjectGroupPython] C_element109  label="C_element : 060"  # scripted group (container) (typed FeaturePython)
  n = 2
  ref = C_element
FEATURE [App::DocumentObjectGroupPython] Cl_element025  label="Cl_element : 012"  # scripted group (container) (typed FeaturePython)
  n = 4
  ref = Cl_element
FEATURE [App::DocumentObjectGroupPython] G4_TETRACHLOROETHYLENE  # scripted group (container) (typed FeaturePython)
  Dunit = g/cm3
  Dvalue = 1.625
  Group = -> [C_element109,Cl_element025]
  conduct = 2
  density = 1
  expand = 3
  formula = G4_TETRACHLOROETHYLENE
  name = G4_TETRACHLOROETHYLENE
  specific = 4
FEATURE [App::DocumentObjectGroupPython] Tl_element001  label="Tl_element : 1"  # scripted group (container) (typed FeaturePython)
  n = 1
  ref = Tl_element
FEATURE [App::DocumentObjectGroupPython] Cl_element026  label="Cl_element : 013"  # scripted group (container) (typed FeaturePython)
  n = 1
  ref = Cl_element
FEATURE [App::DocumentObjectGroupPython] G4_THALLIUM_CHLORIDE  # scripted group (container) (typed FeaturePython)
  Dunit = g/cm3
  Dvalue = 7.004
  Group = -> [Tl_element001,Cl_element026]
  conduct = 2
  density = 1
  expand = 3
  formula = G4_THALLIUM_CHLORIDE
  name = G4_THALLIUM_CHLORIDE
  specific = 4
FEATURE [App::DocumentObjectGroupPython] H_element100  label="H_element : 0.147"  # scripted group (container) (typed FeaturePython)
  n = 0.105
FEATURE [App::DocumentObjectGroupPython] C_element110  label="C_element : 0.256"  # scripted group (container) (typed FeaturePython)
  n = 0.256
FEATURE [App::DocumentObjectGroupPython] N_element042  label="N_element : 0.760"  # scripted group (container) (typed FeaturePython)
  n = 0.027
FEATURE [App::DocumentObjectGroupPython] O_element094  label="O_element : 0.602"  # scripted group (container) (typed FeaturePython)
  n = 0.602
FEATURE [App::DocumentObjectGroupPython] Na_element019  label="Na_element : 0.102"  # scripted group (container) (typed FeaturePython)
  n = 0.001
FEATURE [App::DocumentObjectGroupPython] P_element011  label="P_element : 0.109"  # scripted group (container) (typed FeaturePython)
  n = 0.002
FEATURE [App::DocumentObjectGroupPython] S_element022  label="S_element : 0.023"  # scripted group (container) (typed FeaturePython)
  n = 0.003
FEATURE [App::DocumentObjectGroupPython] Cl_element027  label="Cl_element : 0.591"  # scripted group (container) (typed FeaturePython)
  n = 0.002
FEATURE [App::DocumentObjectGroupPython] K_element012  label="K_element : 0.018"  # scripted group (container) (typed FeaturePython)
  n = 0.002
FEATURE [App::DocumentObjectGroupPython] G4_TISSUE_SOFT_ICRP  # scripted group (container) (typed FeaturePython)
  Dunit = g/cm3
  Dvalue = 1.03
  Group = -> [H_element100,C_element110,N_element042,O_element094,Na_element019,P_element011,S_element022,Cl_element027,K_element012]
  conduct = 2
  density = 1
  expand = 3
  formula = G4_TISSUE_SOFT_ICRP
  name = G4_TISSUE_SOFT_ICRP
  specific = 4
FEATURE [App::DocumentObjectGroupPython] H_element101  label="H_element : 0.148"  # scripted group (container) (typed FeaturePython)
  n = 0.101
FEATURE [App::DocumentObjectGroupPython] C_element111  label="C_element : 0.111"  # scripted group (container) (typed FeaturePython)
  n = 0.111
FEATURE [App::DocumentObjectGroupPython] N_element043  label="N_element : 0.026"  # scripted group (container) (typed FeaturePython)
  n = 0.026
FEATURE [App::DocumentObjectGroupPython] O_element095  label="O_element : 0.762"  # scripted group (container) (typed FeaturePython)
  n = 0.762
FEATURE [App::DocumentObjectGroupPython] G4_TISSUE_SOFT_ICRU_4  label="G4_TISSUE_SOFT_ICRU-4"  # scripted group (container) (typed FeaturePython)
  Dunit = g/cm3
  Dvalue = 1
  Group = -> [H_element101,C_element111,N_element043,O_element095]
  conduct = 2
  density = 1
  expand = 3
  formula = G4_TISSUE_SOFT_ICRU-4
  name = G4_TISSUE_SOFT_ICRU-4
  specific = 4
FEATURE [App::DocumentObjectGroupPython] H_element102  label="H_element : 0.149"  # scripted group (container) (typed FeaturePython)
  n = 0.101869
FEATURE [App::DocumentObjectGroupPython] C_element112  label="C_element : 0.456"  # scripted group (container) (typed FeaturePython)
  n = 0.456179
FEATURE [App::DocumentObjectGroupPython] N_element044  label="N_element : 0.761"  # scripted group (container) (typed FeaturePython)
  n = 0.035172
FEATURE [App::DocumentObjectGroupPython] O_element096  label="O_element : 0.407"  # scripted group (container) (typed FeaturePython)
  n = 0.40678
FEATURE [App::DocumentObjectGroupPython] G4_TISSUE_METHANE  label="G4_TISSUE-METHANE"  # scripted group (container) (typed FeaturePython)
  Dunit = g/cm3
  Dvalue = 0.00106409
  Group = -> [H_element102,C_element112,N_element044,O_element096]
  conduct = 2
  density = 1
  expand = 3
  formula = G4_TISSUE-METHANE
  name = G4_TISSUE-METHANE
  specific = 4
FEATURE [App::DocumentObjectGroupPython] H_element103  label="H_element : 0.103"  # scripted group (container) (typed FeaturePython)
  n = 0.102672
FEATURE [App::DocumentObjectGroupPython] C_element113  label="C_element : 0.569"  # scripted group (container) (typed FeaturePython)
  n = 0.56894
FEATURE [App::DocumentObjectGroupPython] N_element045  label="N_element : 0.762"  # scripted group (container) (typed FeaturePython)
  n = 0.035022
FEATURE [App::DocumentObjectGroupPython] O_element097  label="O_element : 0.293"  # scripted group (container) (typed FeaturePython)
  n = 0.293366
FEATURE [App::DocumentObjectGroupPython] G4_TISSUE_PROPANE  label="G4_TISSUE-PROPANE"  # scripted group (container) (typed FeaturePython)
  Dunit = g/cm3
  Dvalue = 0.00182628
  Group = -> [H_element103,C_element113,N_element045,O_element097]
  conduct = 2
  density = 1
  expand = 3
  formula = G4_TISSUE-PROPANE
  name = G4_TISSUE-PROPANE
  specific = 4
FEATURE [App::DocumentObjectGroupPython] Ti_element003  label="Ti_element : 1"  # scripted group (container) (typed FeaturePython)
  n = 1
  ref = Ti_element
FEATURE [App::DocumentObjectGroupPython] O_element098  label="O_element : 052"  # scripted group (container) (typed FeaturePython)
  n = 2
  ref = O_element
FEATURE [App::DocumentObjectGroupPython] G4_TITANIUM_DIOXIDE  # scripted group (container) (typed FeaturePython)
  Dunit = g/cm3
  Dvalue = 4.26
  Group = -> [Ti_element003,O_element098]
  conduct = 2
  density = 1
  expand = 3
  formula = G4_TITANIUM_DIOXIDE
  name = G4_TITANIUM_DIOXIDE
  specific = 4
FEATURE [App::DocumentObjectGroupPython] C_element114  label="C_element : 061"  # scripted group (container) (typed FeaturePython)
  n = 7
  ref = C_element
FEATURE [App::DocumentObjectGroupPython] H_element104  label="H_element : 055"  # scripted group (container) (typed FeaturePython)
  n = 8
  ref = H_element
FEATURE [App::DocumentObjectGroupPython] G4_TOLUENE  # scripted group (container) (typed FeaturePython)
  Dunit = g/cm3
  Dvalue = 0.8669
  Group = -> [C_element114,H_element104]
  conduct = 2
  density = 1
  expand = 3
  formula = G4_TOLUENE
  name = G4_TOLUENE
  specific = 4
FEATURE [App::DocumentObjectGroupPython] C_element115  label="C_element : 062"  # scripted group (container) (typed FeaturePython)
  n = 2
  ref = C_element
FEATURE [App::DocumentObjectGroupPython] H_element105  label="H_element : 056"  # scripted group (container) (typed FeaturePython)
  n = 1
  ref = H_element
FEATURE [App::DocumentObjectGroupPython] Cl_element028  label="Cl_element : 014"  # scripted group (container) (typed FeaturePython)
  n = 3
  ref = Cl_element
FEATURE [App::DocumentObjectGroupPython] G4_TRICHLOROETHYLENE  # scripted group (container) (typed FeaturePython)
  Dunit = g/cm3
  Dvalue = 1.46
  Group = -> [C_element115,H_element105,Cl_element028]
  conduct = 2
  density = 1
  expand = 3
  formula = G4_TRICHLOROETHYLENE
  name = G4_TRICHLOROETHYLENE
  specific = 4
FEATURE [App::DocumentObjectGroupPython] C_element116  label="C_element : 063"  # scripted group (container) (typed FeaturePython)
  n = 6
  ref = C_element
FEATURE [App::DocumentObjectGroupPython] H_element106  label="H_element : 15"  # scripted group (container) (typed FeaturePython)
  n = 15
  ref = H_element
FEATURE [App::DocumentObjectGroupPython] O_element099  label="O_element : 053"  # scripted group (container) (typed FeaturePython)
  n = 4
  ref = O_element
FEATURE [App::DocumentObjectGroupPython] P_element012  label="P_element : 1"  # scripted group (container) (typed FeaturePython)
  n = 1
  ref = P_element
FEATURE [App::DocumentObjectGroupPython] G4_TRIETHYL_PHOSPHATE  # scripted group (container) (typed FeaturePython)
  Dunit = g/cm3
  Dvalue = 1.07
  Group = -> [C_element116,H_element106,O_element099,P_element012]
  conduct = 2
  density = 1
  expand = 3
  formula = G4_TRIETHYL_PHOSPHATE
  name = G4_TRIETHYL_PHOSPHATE
  specific = 4
FEATURE [App::DocumentObjectGroupPython] W_element003  label="W_element : 003"  # scripted group (container) (typed FeaturePython)
  n = 1
  ref = W_element
FEATURE [App::DocumentObjectGroupPython] F_element017  label="F_element : 6"  # scripted group (container) (typed FeaturePython)
  n = 6
  ref = F_element
FEATURE [App::DocumentObjectGroupPython] G4_TUNGSTEN_HEXAFLUORIDE  # scripted group (container) (typed FeaturePython)
  Dunit = g/cm3
  Dvalue = 2.4
  Group = -> [W_element003,F_element017]
  conduct = 2
  density = 1
  expand = 3
  formula = G4_TUNGSTEN_HEXAFLUORIDE
  name = G4_TUNGSTEN_HEXAFLUORIDE
  specific = 4
FEATURE [App::DocumentObjectGroupPython] U_element001  label="U_element : 1"  # scripted group (container) (typed FeaturePython)
  n = 1
  ref = U_element
FEATURE [App::DocumentObjectGroupPython] C_element117  label="C_element : 064"  # scripted group (container) (typed FeaturePython)
  n = 2
  ref = C_element
FEATURE [App::DocumentObjectGroupPython] G4_URANIUM_DICARBIDE  # scripted group (container) (typed FeaturePython)
  Dunit = g/cm3
  Dvalue = 11.28
  Group = -> [U_element001,C_element117]
  conduct = 2
  density = 1
  expand = 3
  formula = G4_URANIUM_DICARBIDE
  name = G4_URANIUM_DICARBIDE
  specific = 4
FEATURE [App::DocumentObjectGroupPython] U_element002  label="U_element : 002"  # scripted group (container) (typed FeaturePython)
  n = 1
  ref = U_element
FEATURE [App::DocumentObjectGroupPython] C_element118  label="C_element : 065"  # scripted group (container) (typed FeaturePython)
  n = 1
  ref = C_element
FEATURE [App::DocumentObjectGroupPython] G4_URANIUM_MONOCARBIDE  # scripted group (container) (typed FeaturePython)
  Dunit = g/cm3
  Dvalue = 13.63
  Group = -> [U_element002,C_element118]
  conduct = 2
  density = 1
  expand = 3
  formula = G4_URANIUM_MONOCARBIDE
  name = G4_URANIUM_MONOCARBIDE
  specific = 4
FEATURE [App::DocumentObjectGroupPython] U_element003  label="U_element : 003"  # scripted group (container) (typed FeaturePython)
  n = 1
  ref = U_element
FEATURE [App::DocumentObjectGroupPython] O_element100  label="O_element : 054"  # scripted group (container) (typed FeaturePython)
  n = 2
  ref = O_element
FEATURE [App::DocumentObjectGroupPython] G4_URANIUM_OXIDE  # scripted group (container) (typed FeaturePython)
  Dunit = g/cm3
  Dvalue = 10.96
  Group = -> [U_element003,O_element100]
  conduct = 2
  density = 1
  expand = 3
  formula = G4_URANIUM_OXIDE
  name = G4_URANIUM_OXIDE
  specific = 4
FEATURE [App::DocumentObjectGroupPython] C_element119  label="C_element : 066"  # scripted group (container) (typed FeaturePython)
  n = 1
  ref = C_element
FEATURE [App::DocumentObjectGroupPython] H_element107  label="H_element : 057"  # scripted group (container) (typed FeaturePython)
  n = 4
  ref = H_element
FEATURE [App::DocumentObjectGroupPython] N_element046  label="N_element : 019"  # scripted group (container) (typed FeaturePython)
  n = 2
  ref = N_element
FEATURE [App::DocumentObjectGroupPython] O_element101  label="O_element : 055"  # scripted group (container) (typed FeaturePython)
  n = 1
  ref = O_element
FEATURE [App::DocumentObjectGroupPython] G4_UREA  # scripted group (container) (typed FeaturePython)
  Dunit = g/cm3
  Dvalue = 1.323
  Group = -> [C_element119,H_element107,N_element046,O_element101]
  conduct = 2
  density = 1
  expand = 3
  formula = G4_UREA
  name = G4_UREA
  specific = 4
FEATURE [App::DocumentObjectGroupPython] C_element120  label="C_element : 067"  # scripted group (container) (typed FeaturePython)
  n = 5
  ref = C_element
FEATURE [App::DocumentObjectGroupPython] H_element108  label="H_element : 058"  # scripted group (container) (typed FeaturePython)
  n = 11
  ref = H_element
FEATURE [App::DocumentObjectGroupPython] N_element047  label="N_element : 020"  # scripted group (container) (typed FeaturePython)
  n = 1
  ref = N_element
FEATURE [App::DocumentObjectGroupPython] O_element102  label="O_element : 056"  # scripted group (container) (typed FeaturePython)
  n = 2
  ref = O_element
FEATURE [App::DocumentObjectGroupPython] G4_VALINE  # scripted group (container) (typed FeaturePython)
  Dunit = g/cm3
  Dvalue = 1.23
  Group = -> [C_element120,H_element108,N_element047,O_element102]
  conduct = 2
  density = 1
  expand = 3
  formula = G4_VALINE
  name = G4_VALINE
  specific = 4
FEATURE [App::DocumentObjectGroupPython] H_element109  label="H_element : 0.009"  # scripted group (container) (typed FeaturePython)
  n = 0.009417
FEATURE [App::DocumentObjectGroupPython] C_element121  label="C_element : 0.281"  # scripted group (container) (typed FeaturePython)
  n = 0.280555
FEATURE [App::DocumentObjectGroupPython] F_element018  label="F_element : 0.710"  # scripted group (container) (typed FeaturePython)
  n = 0.710028
FEATURE [App::DocumentObjectGroupPython] G4_VITON  # scripted group (container) (typed FeaturePython)
  Dunit = g/cm3
  Dvalue = 1.8
  Group = -> [H_element109,C_element121,F_element018]
  conduct = 2
  density = 1
  expand = 3
  formula = G4_VITON
  name = G4_VITON
  specific = 4
FEATURE [App::DocumentObjectGroupPython] H_element110  label="H_element : 059"  # scripted group (container) (typed FeaturePython)
  n = 2
  ref = H_element
FEATURE [App::DocumentObjectGroupPython] O_element103  label="O_element : 057"  # scripted group (container) (typed FeaturePython)
  n = 1
  ref = O_element
FEATURE [App::DocumentObjectGroupPython] G4_WATER  # scripted group (container) (typed FeaturePython)
  Dunit = g/cm3
  Dvalue = 1
  Group = -> [H_element110,O_element103]
  conduct = 2
  density = 1
  expand = 3
  formula = G4_WATER
  name = G4_WATER
  specific = 4
FEATURE [App::DocumentObjectGroupPython] H_element111  label="H_element : 060"  # scripted group (container) (typed FeaturePython)
  n = 2
  ref = H_element
FEATURE [App::DocumentObjectGroupPython] O_element104  label="O_element : 058"  # scripted group (container) (typed FeaturePython)
  n = 1
  ref = O_element
FEATURE [App::DocumentObjectGroupPython] G4_WATER_VAPOR  # scripted group (container) (typed FeaturePython)
  Dunit = g/cm3
  Dvalue = 0.000756182
  Group = -> [H_element111,O_element104]
  conduct = 2
  density = 1
  expand = 3
  formula = G4_WATER_VAPOR
  name = G4_WATER_VAPOR
  specific = 4
FEATURE [App::DocumentObjectGroupPython] C_element122  label="C_element : 068"  # scripted group (container) (typed FeaturePython)
  n = 8
  ref = C_element
FEATURE [App::DocumentObjectGroupPython] H_element112  label="H_element : 061"  # scripted group (container) (typed FeaturePython)
  n = 10
  ref = H_element
FEATURE [App::DocumentObjectGroupPython] G4_XYLENE  # scripted group (container) (typed FeaturePython)
  Dunit = g/cm3
  Dvalue = 0.87
  Group = -> [C_element122,H_element112]
  conduct = 2
  density = 1
  expand = 3
  formula = G4_XYLENE
  name = G4_XYLENE
  specific = 4
FEATURE [App::DocumentObjectGroupPython] C_element123  label="C_element : 069"  # scripted group (container) (typed FeaturePython)
  n = 1
  ref = C_element
FEATURE [App::DocumentObjectGroupPython] G4_GRAPHITE  # scripted group (container) (typed FeaturePython)
  Dunit = g/cm3
  Dvalue = 2.21
  Group = -> [C_element123]
  conduct = 2
  density = 1
  expand = 3
  formula = G4_GRAPHITE
  name = G4_GRAPHITE
  specific = 4
FEATURE [App::DocumentObjectGroupPython] NIST  # scripted group (container) (typed FeaturePython)
  Group = -> [G4_A_150_TISSUE,G4_ACETONE,G4_ACETYLENE,G4_ADENINE,G4_ADIPOSE_TISSUE_ICRP,G4_AIR,G4_ALANINE,G4_ALUMINUM_OXIDE,G4_AMBER,G4_AMMONIA,G4_ANILINE,G4_ANTHRACENE,G4_B_100_BONE,G4_BAKELITE,G4_BARIUM_FLUORIDE,G4_BARIUM_SULFATE,G4_BENZENE,G4_BERYLLIUM_OXIDE,G4_BGO,G4_BLOOD_ICRP,G4_BONE_COMPACT_ICRU,G4_BONE_CORTICAL_ICRP,G4_BORON_CARBIDE,G4_BORON_OXIDE,G4_BRAIN_ICRP,G4_BUTANE,G4_N_BUTYL_ALCOHOL,G4_C_552,+152 more]
FEATURE [App::DocumentObjectGroupPython] H_element113  label="H_element : 062"  # scripted group (container) (typed FeaturePython)
  n = 1
  ref = H_element
FEATURE [App::DocumentObjectGroupPython] G4_H  # scripted group (container) (typed FeaturePython)
  Dunit = g/cm3
  Dvalue = 8.3748e-05
  Group = -> [H_element113]
  conduct = 2
  density = 1
  expand = 3
  formula = H
  name = G4_H
  specific = 4
FEATURE [App::DocumentObjectGroupPython] He_element001  label="He_element : 1"  # scripted group (container) (typed FeaturePython)
  n = 1
  ref = He_element
FEATURE [App::DocumentObjectGroupPython] G4_He  # scripted group (container) (typed FeaturePython)
  Dunit = g/cm3
  Dvalue = 0.000166322
  Group = -> [He_element001]
  conduct = 2
  density = 1
  expand = 3
  formula = He
  name = G4_He
  specific = 4
FEATURE [App::DocumentObjectGroupPython] Li_element008  label="Li_element : 008"  # scripted group (container) (typed FeaturePython)
  n = 1
  ref = Li_element
FEATURE [App::DocumentObjectGroupPython] G4_Li  # scripted group (container) (typed FeaturePython)
  Dunit = g/cm3
  Dvalue = 0.534
  Group = -> [Li_element008]
  conduct = 2
  density = 1
  expand = 3
  formula = Li
  name = G4_Li
  specific = 4
FEATURE [App::DocumentObjectGroupPython] Be_element002  label="Be_element : 002"  # scripted group (container) (typed FeaturePython)
  n = 1
  ref = Be_element
FEATURE [App::DocumentObjectGroupPython] G4_Be  # scripted group (container) (typed FeaturePython)
  Dunit = g/cm3
  Dvalue = 1.848
  Group = -> [Be_element002]
  conduct = 2
  density = 1
  expand = 3
  formula = Be
  name = G4_Be
  specific = 4
FEATURE [App::DocumentObjectGroupPython] B_element007  label="B_element : 007"  # scripted group (container) (typed FeaturePython)
  n = 1
  ref = B_element
FEATURE [App::DocumentObjectGroupPython] G4_B  # scripted group (container) (typed FeaturePython)
  Dunit = g/cm3
  Dvalue = 2.37
  Group = -> [B_element007]
  conduct = 2
  density = 1
  expand = 3
  formula = B
  name = G4_B
  specific = 4
FEATURE [App::DocumentObjectGroupPython] C_element124  label="C_element : 070"  # scripted group (container) (typed FeaturePython)
  n = 1
  ref = C_element
FEATURE [App::DocumentObjectGroupPython] G4_C  # scripted group (container) (typed FeaturePython)
  Dunit = g/cm3
  Dvalue = 2
  Group = -> [C_element124]
  conduct = 2
  density = 1
  expand = 3
  formula = C
  name = G4_C
  specific = 4
FEATURE [App::DocumentObjectGroupPython] N_element048  label="N_element : 021"  # scripted group (container) (typed FeaturePython)
  n = 1
  ref = N_element
FEATURE [App::DocumentObjectGroupPython] G4_N  # scripted group (container) (typed FeaturePython)
  Dunit = g/cm3
  Dvalue = 0.0011652
  Group = -> [N_element048]
  conduct = 2
  density = 1
  expand = 3
  formula = N
  name = G4_N
  specific = 4
FEATURE [App::DocumentObjectGroupPython] O_element105  label="O_element : 059"  # scripted group (container) (typed FeaturePython)
  n = 1
  ref = O_element
FEATURE [App::DocumentObjectGroupPython] G4_O  # scripted group (container) (typed FeaturePython)
  Dunit = g/cm3
  Dvalue = 0.00133151
  Group = -> [O_element105]
  conduct = 2
  density = 1
  expand = 3
  formula = O
  name = G4_O
  specific = 4
FEATURE [App::DocumentObjectGroupPython] F_element019  label="F_element : 008"  # scripted group (container) (typed FeaturePython)
  n = 1
  ref = F_element
FEATURE [App::DocumentObjectGroupPython] G4_F  # scripted group (container) (typed FeaturePython)
  Dunit = g/cm3
  Dvalue = 0.00158029
  Group = -> [F_element019]
  conduct = 2
  density = 1
  expand = 3
  formula = F
  name = G4_F
  specific = 4
FEATURE [App::DocumentObjectGroupPython] Ne_element001  label="Ne_element : 1"  # scripted group (container) (typed FeaturePython)
  n = 1
  ref = Ne_element
FEATURE [App::DocumentObjectGroupPython] G4_Ne  # scripted group (container) (typed FeaturePython)
  Dunit = g/cm3
  Dvalue = 0.000838505
  Group = -> [Ne_element001]
  conduct = 2
  density = 1
  expand = 3
  formula = Ne
  name = G4_Ne
  specific = 4
FEATURE [App::DocumentObjectGroupPython] Na_element020  label="Na_element : 005"  # scripted group (container) (typed FeaturePython)
  n = 1
  ref = Na_element
FEATURE [App::DocumentObjectGroupPython] G4_Na  # scripted group (container) (typed FeaturePython)
  Dunit = g/cm3
  Dvalue = 0.971
  Group = -> [Na_element020]
  conduct = 2
  density = 1
  expand = 3
  formula = Na
  name = G4_Na
  specific = 4
FEATURE [App::DocumentObjectGroupPython] Mg_element011  label="Mg_element : 005"  # scripted group (container) (typed FeaturePython)
  n = 1
  ref = Mg_element
FEATURE [App::DocumentObjectGroupPython] G4_Mg  # scripted group (container) (typed FeaturePython)
  Dunit = g/cm3
  Dvalue = 1.74
  Group = -> [Mg_element011]
  conduct = 2
  density = 1
  expand = 3
  formula = Mg
  name = G4_Mg
  specific = 4
FEATURE [App::DocumentObjectGroupPython] Al_element004  label="Al_element : 1"  # scripted group (container) (typed FeaturePython)
  n = 1
  ref = Al_element
FEATURE [App::DocumentObjectGroupPython] G4_Al  # scripted group (container) (typed FeaturePython)
  Dunit = g/cm3
  Dvalue = 2.699
  Group = -> [Al_element004]
  conduct = 2
  density = 1
  expand = 3
  formula = Al
  name = G4_Al
  specific = 4
FEATURE [App::DocumentObjectGroupPython] Si_element007  label="Si_element : 002"  # scripted group (container) (typed FeaturePython)
  n = 1
  ref = Si_element
FEATURE [App::DocumentObjectGroupPython] G4_Si  # scripted group (container) (typed FeaturePython)
  Dunit = g/cm3
  Dvalue = 2.33
  Group = -> [Si_element007]
  conduct = 2
  density = 1
  expand = 3
  formula = Si
  name = G4_Si
  specific = 4
FEATURE [App::DocumentObjectGroupPython] P_element013  label="P_element : 002"  # scripted group (container) (typed FeaturePython)
  n = 1
  ref = P_element
FEATURE [App::DocumentObjectGroupPython] G4_P  # scripted group (container) (typed FeaturePython)
  Dunit = g/cm3
  Dvalue = 2.2
  Group = -> [P_element013]
  conduct = 2
  density = 1
  expand = 3
  formula = P
  name = G4_P
  specific = 4
FEATURE [App::DocumentObjectGroupPython] S_element023  label="S_element : 007"  # scripted group (container) (typed FeaturePython)
  n = 1
  ref = S_element
FEATURE [App::DocumentObjectGroupPython] G4_S  # scripted group (container) (typed FeaturePython)
  Dunit = g/cm3
  Dvalue = 2
  Group = -> [S_element023]
  conduct = 2
  density = 1
  expand = 3
  formula = S
  name = G4_S
  specific = 4
FEATURE [App::DocumentObjectGroupPython] Cl_element029  label="Cl_element : 015"  # scripted group (container) (typed FeaturePython)
  n = 1
  ref = Cl_element
FEATURE [App::DocumentObjectGroupPython] G4_Cl  # scripted group (container) (typed FeaturePython)
  Dunit = g/cm3
  Dvalue = 0.00299473
  Group = -> [Cl_element029]
  conduct = 2
  density = 1
  expand = 3
  formula = Cl
  name = G4_Cl
  specific = 4
FEATURE [App::DocumentObjectGroupPython] Ar_element002  label="Ar_element : 1"  # scripted group (container) (typed FeaturePython)
  n = 1
  ref = Ar_element
FEATURE [App::DocumentObjectGroupPython] G4_Ar  # scripted group (container) (typed FeaturePython)
  Dunit = g/cm3
  Dvalue = 0.00166201
  Group = -> [Ar_element002]
  conduct = 2
  density = 1
  expand = 3
  formula = Ar
  name = G4_Ar
  specific = 4
FEATURE [App::DocumentObjectGroupPython] K_element013  label="K_element : 003"  # scripted group (container) (typed FeaturePython)
  n = 1
  ref = K_element
FEATURE [App::DocumentObjectGroupPython] G4_K  # scripted group (container) (typed FeaturePython)
  Dunit = g/cm3
  Dvalue = 0.862
  Group = -> [K_element013]
  conduct = 2
  density = 1
  expand = 3
  formula = K
  name = G4_K
  specific = 4
FEATURE [App::DocumentObjectGroupPython] Ca_element014  label="Ca_element : 007"  # scripted group (container) (typed FeaturePython)
  n = 1
  ref = Ca_element
FEATURE [App::DocumentObjectGroupPython] G4_Ca  # scripted group (container) (typed FeaturePython)
  Dunit = g/cm3
  Dvalue = 1.55
  Group = -> [Ca_element014]
  conduct = 2
  density = 1
  expand = 3
  formula = Ca
  name = G4_Ca
  specific = 4
FEATURE [App::DocumentObjectGroupPython] Sc_element001  label="Sc_element : 1"  # scripted group (container) (typed FeaturePython)
  n = 1
  ref = Sc_element
FEATURE [App::DocumentObjectGroupPython] G4_Sc  # scripted group (container) (typed FeaturePython)
  Dunit = g/cm3
  Dvalue = 2.989
  Group = -> [Sc_element001]
  conduct = 2
  density = 1
  expand = 3
  formula = Sc
  name = G4_Sc
  specific = 4
FEATURE [App::DocumentObjectGroupPython] Ti_element004  label="Ti_element : 002"  # scripted group (container) (typed FeaturePython)
  n = 1
  ref = Ti_element
FEATURE [App::DocumentObjectGroupPython] G4_Ti  # scripted group (container) (typed FeaturePython)
  Dunit = g/cm3
  Dvalue = 4.54
  Group = -> [Ti_element004]
  conduct = 2
  density = 1
  expand = 3
  formula = Ti
  name = G4_Ti
  specific = 4
FEATURE [App::DocumentObjectGroupPython] V_element001  label="V_element : 1"  # scripted group (container) (typed FeaturePython)
  n = 1
  ref = V_element
FEATURE [App::DocumentObjectGroupPython] G4_V  # scripted group (container) (typed FeaturePython)
  Dunit = g/cm3
  Dvalue = 6.11
  Group = -> [V_element001]
  conduct = 2
  density = 1
  expand = 3
  formula = V
  name = G4_V
  specific = 4
FEATURE [App::DocumentObjectGroupPython] Cr_element001  label="Cr_element : 1"  # scripted group (container) (typed FeaturePython)
  n = 1
  ref = Cr_element
FEATURE [App::DocumentObjectGroupPython] G4_Cr  # scripted group (container) (typed FeaturePython)
  Dunit = g/cm3
  Dvalue = 7.18
  Group = -> [Cr_element001]
  conduct = 2
  density = 1
  expand = 3
  formula = Cr
  name = G4_Cr
  specific = 4
FEATURE [App::DocumentObjectGroupPython] Mn_element001  label="Mn_element : 1"  # scripted group (container) (typed FeaturePython)
  n = 1
  ref = Mn_element
FEATURE [App::DocumentObjectGroupPython] G4_Mn  # scripted group (container) (typed FeaturePython)
  Dunit = g/cm3
  Dvalue = 7.44
  Group = -> [Mn_element001]
  conduct = 2
  density = 1
  expand = 3
  formula = Mn
  name = G4_Mn
  specific = 4
FEATURE [App::DocumentObjectGroupPython] Fe_element007  label="Fe_element : 004"  # scripted group (container) (typed FeaturePython)
  n = 1
  ref = Fe_element
FEATURE [App::DocumentObjectGroupPython] G4_Fe  # scripted group (container) (typed FeaturePython)
  Dunit = g/cm3
  Dvalue = 7.874
  Group = -> [Fe_element007]
  conduct = 2
  density = 1
  expand = 3
  formula = Fe
  name = G4_Fe
  specific = 4
FEATURE [App::DocumentObjectGroupPython] Co_element001  label="Co_element : 1"  # scripted group (container) (typed FeaturePython)
  n = 1
  ref = Co_element
FEATURE [App::DocumentObjectGroupPython] G4_Co  # scripted group (container) (typed FeaturePython)
  Dunit = g/cm3
  Dvalue = 8.9
  Group = -> [Co_element001]
  conduct = 2
  density = 1
  expand = 3
  formula = Co
  name = G4_Co
  specific = 4
FEATURE [App::DocumentObjectGroupPython] Ni_element001  label="Ni_element : 1"  # scripted group (container) (typed FeaturePython)
  n = 1
  ref = Ni_element
FEATURE [App::DocumentObjectGroupPython] G4_Ni  # scripted group (container) (typed FeaturePython)
  Dunit = g/cm3
  Dvalue = 8.902
  Group = -> [Ni_element001]
  conduct = 2
  density = 1
  expand = 3
  formula = Ni
  name = G4_Ni
  specific = 4
FEATURE [App::DocumentObjectGroupPython] Cu_element001  label="Cu_element : 1"  # scripted group (container) (typed FeaturePython)
  n = 1
  ref = Cu_element
FEATURE [App::DocumentObjectGroupPython] G4_Cu  # scripted group (container) (typed FeaturePython)
  Dunit = g/cm3
  Dvalue = 8.96
  Group = -> [Cu_element001]
  conduct = 2
  density = 1
  expand = 3
  formula = Cu
  name = G4_Cu
  specific = 4
FEATURE [App::DocumentObjectGroupPython] Zn_element001  label="Zn_element : 1"  # scripted group (container) (typed FeaturePython)
  n = 1
  ref = Zn_element
FEATURE [App::DocumentObjectGroupPython] G4_Zn  # scripted group (container) (typed FeaturePython)
  Dunit = g/cm3
  Dvalue = 7.133
  Group = -> [Zn_element001]
  conduct = 2
  density = 1
  expand = 3
  formula = Zn
  name = G4_Zn
  specific = 4
FEATURE [App::DocumentObjectGroupPython] Ga_element002  label="Ga_element : 002"  # scripted group (container) (typed FeaturePython)
  n = 1
  ref = Ga_element
FEATURE [App::DocumentObjectGroupPython] G4_Ga  # scripted group (container) (typed FeaturePython)
  Dunit = g/cm3
  Dvalue = 5.904
  Group = -> [Ga_element002]
  conduct = 2
  density = 1
  expand = 3
  formula = Ga
  name = G4_Ga
  specific = 4
FEATURE [App::DocumentObjectGroupPython] Ge_element002  label="Ge_element : 1"  # scripted group (container) (typed FeaturePython)
  n = 1
  ref = Ge_element
FEATURE [App::DocumentObjectGroupPython] G4_Ge  # scripted group (container) (typed FeaturePython)
  Dunit = g/cm3
  Dvalue = 5.323
  Group = -> [Ge_element002]
  conduct = 2
  density = 1
  expand = 3
  formula = Ge
  name = G4_Ge
  specific = 4
FEATURE [App::DocumentObjectGroupPython] As_element003  label="As_element : 002"  # scripted group (container) (typed FeaturePython)
  n = 1
  ref = As_element
FEATURE [App::DocumentObjectGroupPython] G4_As  # scripted group (container) (typed FeaturePython)
  Dunit = g/cm3
  Dvalue = 5.73
  Group = -> [As_element003]
  conduct = 2
  density = 1
  expand = 3
  formula = As
  name = G4_As
  specific = 4
FEATURE [App::DocumentObjectGroupPython] Se_element001  label="Se_element : 1"  # scripted group (container) (typed FeaturePython)
  n = 1
  ref = Se_element
FEATURE [App::DocumentObjectGroupPython] G4_Se  # scripted group (container) (typed FeaturePython)
  Dunit = g/cm3
  Dvalue = 4.5
  Group = -> [Se_element001]
  conduct = 2
  density = 1
  expand = 3
  formula = Se
  name = G4_Se
  specific = 4
FEATURE [App::DocumentObjectGroupPython] Br_element007  label="Br_element : 004"  # scripted group (container) (typed FeaturePython)
  n = 1
  ref = Br_element
FEATURE [App::DocumentObjectGroupPython] G4_Br  # scripted group (container) (typed FeaturePython)
  Dunit = g/cm3
  Dvalue = 0.0070721
  Group = -> [Br_element007]
  conduct = 2
  density = 1
  expand = 3
  formula = Br
  name = G4_Br
  specific = 4
FEATURE [App::DocumentObjectGroupPython] Kr_element001  label="Kr_element : 1"  # scripted group (container) (typed FeaturePython)
  n = 1
  ref = Kr_element
FEATURE [App::DocumentObjectGroupPython] G4_Kr  # scripted group (container) (typed FeaturePython)
  Dunit = g/cm3
  Dvalue = 0.00347832
  Group = -> [Kr_element001]
  conduct = 2
  density = 1
  expand = 3
  formula = Kr
  name = G4_Kr
  specific = 4
FEATURE [App::DocumentObjectGroupPython] Rb_element001  label="Rb_element : 1"  # scripted group (container) (typed FeaturePython)
  n = 1
  ref = Rb_element
FEATURE [App::DocumentObjectGroupPython] G4_Rb  # scripted group (container) (typed FeaturePython)
  Dunit = g/cm3
  Dvalue = 1.532
  Group = -> [Rb_element001]
  conduct = 2
  density = 1
  expand = 3
  formula = Rb
  name = G4_Rb
  specific = 4
FEATURE [App::DocumentObjectGroupPython] Sr_element001  label="Sr_element : 1"  # scripted group (container) (typed FeaturePython)
  n = 1
  ref = Sr_element
FEATURE [App::DocumentObjectGroupPython] G4_Sr  # scripted group (container) (typed FeaturePython)
  Dunit = g/cm3
  Dvalue = 2.54
  Group = -> [Sr_element001]
  conduct = 2
  density = 1
  expand = 3
  formula = Sr
  name = G4_Sr
  specific = 4
FEATURE [App::DocumentObjectGroupPython] Y_element001  label="Y_element : 1"  # scripted group (container) (typed FeaturePython)
  n = 1
  ref = Y_element
FEATURE [App::DocumentObjectGroupPython] G4_Y  # scripted group (container) (typed FeaturePython)
  Dunit = g/cm3
  Dvalue = 4.469
  Group = -> [Y_element001]
  conduct = 2
  density = 1
  expand = 3
  formula = Y
  name = G4_Y
  specific = 4
FEATURE [App::DocumentObjectGroupPython] Zr_element001  label="Zr_element : 1"  # scripted group (container) (typed FeaturePython)
  n = 1
  ref = Zr_element
FEATURE [App::DocumentObjectGroupPython] G4_Zr  # scripted group (container) (typed FeaturePython)
  Dunit = g/cm3
  Dvalue = 6.506
  Group = -> [Zr_element001]
  conduct = 2
  density = 1
  expand = 3
  formula = Zr
  name = G4_Zr
  specific = 4
FEATURE [App::DocumentObjectGroupPython] Nb_element001  label="Nb_element : 1"  # scripted group (container) (typed FeaturePython)
  n = 1
  ref = Nb_element
FEATURE [App::DocumentObjectGroupPython] G4_Nb  # scripted group (container) (typed FeaturePython)
  Dunit = g/cm3
  Dvalue = 8.57
  Group = -> [Nb_element001]
  conduct = 2
  density = 1
  expand = 3
  formula = Nb
  name = G4_Nb
  specific = 4
FEATURE [App::DocumentObjectGroupPython] Mo_element001  label="Mo_element : 1"  # scripted group (container) (typed FeaturePython)
  n = 1
  ref = Mo_element
FEATURE [App::DocumentObjectGroupPython] G4_Mo  # scripted group (container) (typed FeaturePython)
  Dunit = g/cm3
  Dvalue = 10.22
  Group = -> [Mo_element001]
  conduct = 2
  density = 1
  expand = 3
  formula = Mo
  name = G4_Mo
  specific = 4
FEATURE [App::DocumentObjectGroupPython] Tc_element001  label="Tc_element : 1"  # scripted group (container) (typed FeaturePython)
  n = 1
  ref = Tc_element
FEATURE [App::DocumentObjectGroupPython] G4_Tc  # scripted group (container) (typed FeaturePython)
  Dunit = g/cm3
  Dvalue = 11.5
  Group = -> [Tc_element001]
  conduct = 2
  density = 1
  expand = 3
  formula = Tc
  name = G4_Tc
  specific = 4
FEATURE [App::DocumentObjectGroupPython] Ru_element001  label="Ru_element : 1"  # scripted group (container) (typed FeaturePython)
  n = 1
  ref = Ru_element
FEATURE [App::DocumentObjectGroupPython] G4_Ru  # scripted group (container) (typed FeaturePython)
  Dunit = g/cm3
  Dvalue = 12.41
  Group = -> [Ru_element001]
  conduct = 2
  density = 1
  expand = 3
  formula = Ru
  name = G4_Ru
  specific = 4
FEATURE [App::DocumentObjectGroupPython] Rh_element001  label="Rh_element : 1"  # scripted group (container) (typed FeaturePython)
  n = 1
  ref = Rh_element
FEATURE [App::DocumentObjectGroupPython] G4_Rh  # scripted group (container) (typed FeaturePython)
  Dunit = g/cm3
  Dvalue = 12.41
  Group = -> [Rh_element001]
  conduct = 2
  density = 1
  expand = 3
  formula = Rh
  name = G4_Rh
  specific = 4
FEATURE [App::DocumentObjectGroupPython] Pd_element001  label="Pd_element : 1"  # scripted group (container) (typed FeaturePython)
  n = 1
  ref = Pd_element
FEATURE [App::DocumentObjectGroupPython] G4_Pd  # scripted group (container) (typed FeaturePython)
  Dunit = g/cm3
  Dvalue = 12.02
  Group = -> [Pd_element001]
  conduct = 2
  density = 1
  expand = 3
  formula = Pd
  name = G4_Pd
  specific = 4
FEATURE [App::DocumentObjectGroupPython] Ag_element006  label="Ag_element : 004"  # scripted group (container) (typed FeaturePython)
  n = 1
  ref = Ag_element
FEATURE [App::DocumentObjectGroupPython] G4_Ag  # scripted group (container) (typed FeaturePython)
  Dunit = g/cm3
  Dvalue = 10.5
  Group = -> [Ag_element006]
  conduct = 2
  density = 1
  expand = 3
  formula = Ag
  name = G4_Ag
  specific = 4
FEATURE [App::DocumentObjectGroupPython] Cd_element003  label="Cd_element : 003"  # scripted group (container) (typed FeaturePython)
  n = 1
  ref = Cd_element
FEATURE [App::DocumentObjectGroupPython] G4_Cd  # scripted group (container) (typed FeaturePython)
  Dunit = g/cm3
  Dvalue = 8.65
  Group = -> [Cd_element003]
  conduct = 2
  density = 1
  expand = 3
  formula = Cd
  name = G4_Cd
  specific = 4
FEATURE [App::DocumentObjectGroupPython] In_element001  label="In_element : 1"  # scripted group (container) (typed FeaturePython)
  n = 1
  ref = In_element
FEATURE [App::DocumentObjectGroupPython] G4_In  # scripted group (container) (typed FeaturePython)
  Dunit = g/cm3
  Dvalue = 7.31
  Group = -> [In_element001]
  conduct = 2
  density = 1
  expand = 3
  formula = In
  name = G4_In
  specific = 4
FEATURE [App::DocumentObjectGroupPython] Sn_element001  label="Sn_element : 1"  # scripted group (container) (typed FeaturePython)
  n = 1
  ref = Sn_element
FEATURE [App::DocumentObjectGroupPython] G4_Sn  # scripted group (container) (typed FeaturePython)
  Dunit = g/cm3
  Dvalue = 7.31
  Group = -> [Sn_element001]
  conduct = 2
  density = 1
  expand = 3
  formula = Sn
  name = G4_Sn
  specific = 4
FEATURE [App::DocumentObjectGroupPython] Sb_element001  label="Sb_element : 1"  # scripted group (container) (typed FeaturePython)
  n = 1
  ref = Sb_element
FEATURE [App::DocumentObjectGroupPython] G4_Sb  # scripted group (container) (typed FeaturePython)
  Dunit = g/cm3
  Dvalue = 6.691
  Group = -> [Sb_element001]
  conduct = 2
  density = 1
  expand = 3
  formula = Sb
  name = G4_Sb
  specific = 4
FEATURE [App::DocumentObjectGroupPython] Te_element002  label="Te_element : 002"  # scripted group (container) (typed FeaturePython)
  n = 1
  ref = Te_element
FEATURE [App::DocumentObjectGroupPython] G4_Te  # scripted group (container) (typed FeaturePython)
  Dunit = g/cm3
  Dvalue = 6.24
  Group = -> [Te_element002]
  conduct = 2
  density = 1
  expand = 3
  formula = Te
  name = G4_Te
  specific = 4
FEATURE [App::DocumentObjectGroupPython] I_element010  label="I_element : 006"  # scripted group (container) (typed FeaturePython)
  n = 1
  ref = I_element
FEATURE [App::DocumentObjectGroupPython] G4_I  # scripted group (container) (typed FeaturePython)
  Dunit = g/cm3
  Dvalue = 4.93
  Group = -> [I_element010]
  conduct = 2
  density = 1
  expand = 3
  formula = I
  name = G4_I
  specific = 4
FEATURE [App::DocumentObjectGroupPython] Xe_element001  label="Xe_element : 1"  # scripted group (container) (typed FeaturePython)
  n = 1
  ref = Xe_element
FEATURE [App::DocumentObjectGroupPython] G4_Xe  # scripted group (container) (typed FeaturePython)
  Dunit = g/cm3
  Dvalue = 0.00548536
  Group = -> [Xe_element001]
  conduct = 2
  density = 1
  expand = 3
  formula = Xe
  name = G4_Xe
  specific = 4
FEATURE [App::DocumentObjectGroupPython] Cs_element003  label="Cs_element : 003"  # scripted group (container) (typed FeaturePython)
  n = 1
  ref = Cs_element
FEATURE [App::DocumentObjectGroupPython] G4_Cs  # scripted group (container) (typed FeaturePython)
  Dunit = g/cm3
  Dvalue = 1.873
  Group = -> [Cs_element003]
  conduct = 2
  density = 1
  expand = 3
  formula = Cs
  name = G4_Cs
  specific = 4
FEATURE [App::DocumentObjectGroupPython] Ba_element003  label="Ba_element : 003"  # scripted group (container) (typed FeaturePython)
  n = 1
  ref = Ba_element
FEATURE [App::DocumentObjectGroupPython] G4_Ba  # scripted group (container) (typed FeaturePython)
  Dunit = g/cm3
  Dvalue = 3.5
  Group = -> [Ba_element003]
  conduct = 2
  density = 1
  expand = 3
  formula = Ba
  name = G4_Ba
  specific = 4
FEATURE [App::DocumentObjectGroupPython] La_element003  label="La_element : 003"  # scripted group (container) (typed FeaturePython)
  n = 1
  ref = La_element
FEATURE [App::DocumentObjectGroupPython] G4_La  # scripted group (container) (typed FeaturePython)
  Dunit = g/cm3
  Dvalue = 6.154
  Group = -> [La_element003]
  conduct = 2
  density = 1
  expand = 3
  formula = La
  name = G4_La
  specific = 4
FEATURE [App::DocumentObjectGroupPython] Ce_element002  label="Ce_element : 1"  # scripted group (container) (typed FeaturePython)
  n = 1
  ref = Ce_element
FEATURE [App::DocumentObjectGroupPython] G4_Ce  # scripted group (container) (typed FeaturePython)
  Dunit = g/cm3
  Dvalue = 6.657
  Group = -> [Ce_element002]
  conduct = 2
  density = 1
  expand = 3
  formula = Ce
  name = G4_Ce
  specific = 4
FEATURE [App::DocumentObjectGroupPython] Pr_element001  label="Pr_element : 1"  # scripted group (container) (typed FeaturePython)
  n = 1
  ref = Pr_element
FEATURE [App::DocumentObjectGroupPython] G4_Pr  # scripted group (container) (typed FeaturePython)
  Dunit = g/cm3
  Dvalue = 6.71
  Group = -> [Pr_element001]
  conduct = 2
  density = 1
  expand = 3
  formula = Pr
  name = G4_Pr
  specific = 4
FEATURE [App::DocumentObjectGroupPython] Nd_element001  label="Nd_element : 1"  # scripted group (container) (typed FeaturePython)
  n = 1
  ref = Nd_element
FEATURE [App::DocumentObjectGroupPython] G4_Nd  # scripted group (container) (typed FeaturePython)
  Dunit = g/cm3
  Dvalue = 6.9
  Group = -> [Nd_element001]
  conduct = 2
  density = 1
  expand = 3
  formula = Nd
  name = G4_Nd
  specific = 4
FEATURE [App::DocumentObjectGroupPython] Pm_element001  label="Pm_element : 1"  # scripted group (container) (typed FeaturePython)
  n = 1
  ref = Pm_element
FEATURE [App::DocumentObjectGroupPython] G4_Pm  # scripted group (container) (typed FeaturePython)
  Dunit = g/cm3
  Dvalue = 7.22
  Group = -> [Pm_element001]
  conduct = 2
  density = 1
  expand = 3
  formula = Pm
  name = G4_Pm
  specific = 4
FEATURE [App::DocumentObjectGroupPython] Sm_element001  label="Sm_element : 1"  # scripted group (container) (typed FeaturePython)
  n = 1
  ref = Sm_element
FEATURE [App::DocumentObjectGroupPython] G4_Sm  # scripted group (container) (typed FeaturePython)
  Dunit = g/cm3
  Dvalue = 7.46
  Group = -> [Sm_element001]
  conduct = 2
  density = 1
  expand = 3
  formula = Sm
  name = G4_Sm
  specific = 4
FEATURE [App::DocumentObjectGroupPython] Eu_element001  label="Eu_element : 1"  # scripted group (container) (typed FeaturePython)
  n = 1
  ref = Eu_element
FEATURE [App::DocumentObjectGroupPython] G4_Eu  # scripted group (container) (typed FeaturePython)
  Dunit = g/cm3
  Dvalue = 5.243
  Group = -> [Eu_element001]
  conduct = 2
  density = 1
  expand = 3
  formula = Eu
  name = G4_Eu
  specific = 4
FEATURE [App::DocumentObjectGroupPython] Gd_element002  label="Gd_element : 1"  # scripted group (container) (typed FeaturePython)
  n = 1
  ref = Gd_element
FEATURE [App::DocumentObjectGroupPython] G4_Gd  # scripted group (container) (typed FeaturePython)
  Dunit = g/cm3
  Dvalue = 7.9004
  Group = -> [Gd_element002]
  conduct = 2
  density = 1
  expand = 3
  formula = Gd
  name = G4_Gd
  specific = 4
FEATURE [App::DocumentObjectGroupPython] Tb_element001  label="Tb_element : 1"  # scripted group (container) (typed FeaturePython)
  n = 1
  ref = Tb_element
FEATURE [App::DocumentObjectGroupPython] G4_Tb  # scripted group (container) (typed FeaturePython)
  Dunit = g/cm3
  Dvalue = 8.229
  Group = -> [Tb_element001]
  conduct = 2
  density = 1
  expand = 3
  formula = Tb
  name = G4_Tb
  specific = 4
FEATURE [App::DocumentObjectGroupPython] Dy_element001  label="Dy_element : 1"  # scripted group (container) (typed FeaturePython)
  n = 1
  ref = Dy_element
FEATURE [App::DocumentObjectGroupPython] G4_Dy  # scripted group (container) (typed FeaturePython)
  Dunit = g/cm3
  Dvalue = 8.55
  Group = -> [Dy_element001]
  conduct = 2
  density = 1
  expand = 3
  formula = Dy
  name = G4_Dy
  specific = 4
FEATURE [App::DocumentObjectGroupPython] Ho_element001  label="Ho_element : 1"  # scripted group (container) (typed FeaturePython)
  n = 1
  ref = Ho_element
FEATURE [App::DocumentObjectGroupPython] G4_Ho  # scripted group (container) (typed FeaturePython)
  Dunit = g/cm3
  Dvalue = 8.795
  Group = -> [Ho_element001]
  conduct = 2
  density = 1
  expand = 3
  formula = Ho
  name = G4_Ho
  specific = 4
FEATURE [App::DocumentObjectGroupPython] Er_element001  label="Er_element : 1"  # scripted group (container) (typed FeaturePython)
  n = 1
  ref = Er_element
FEATURE [App::DocumentObjectGroupPython] G4_Er  # scripted group (container) (typed FeaturePython)
  Dunit = g/cm3
  Dvalue = 9.066
  Group = -> [Er_element001]
  conduct = 2
  density = 1
  expand = 3
  formula = Er
  name = G4_Er
  specific = 4
FEATURE [App::DocumentObjectGroupPython] Tm_element001  label="Tm_element : 1"  # scripted group (container) (typed FeaturePython)
  n = 1
  ref = Tm_element
FEATURE [App::DocumentObjectGroupPython] G4_Tm  # scripted group (container) (typed FeaturePython)
  Dunit = g/cm3
  Dvalue = 9.321
  Group = -> [Tm_element001]
  conduct = 2
  density = 1
  expand = 3
  formula = Tm
  name = G4_Tm
  specific = 4
FEATURE [App::DocumentObjectGroupPython] Yb_element001  label="Yb_element : 1"  # scripted group (container) (typed FeaturePython)
  n = 1
  ref = Yb_element
FEATURE [App::DocumentObjectGroupPython] G4_Yb  # scripted group (container) (typed FeaturePython)
  Dunit = g/cm3
  Dvalue = 6.73
  Group = -> [Yb_element001]
  conduct = 2
  density = 1
  expand = 3
  formula = Yb
  name = G4_Yb
  specific = 4
FEATURE [App::DocumentObjectGroupPython] Lu_element001  label="Lu_element : 1"  # scripted group (container) (typed FeaturePython)
  n = 1
  ref = Lu_element
FEATURE [App::DocumentObjectGroupPython] G4_Lu  # scripted group (container) (typed FeaturePython)
  Dunit = g/cm3
  Dvalue = 9.84
  Group = -> [Lu_element001]
  conduct = 2
  density = 1
  expand = 3
  formula = Lu
  name = G4_Lu
  specific = 4
FEATURE [App::DocumentObjectGroupPython] Hf_element001  label="Hf_element : 1"  # scripted group (container) (typed FeaturePython)
  n = 1
  ref = Hf_element
FEATURE [App::DocumentObjectGroupPython] G4_Hf  # scripted group (container) (typed FeaturePython)
  Dunit = g/cm3
  Dvalue = 13.31
  Group = -> [Hf_element001]
  conduct = 2
  density = 1
  expand = 3
  formula = Hf
  name = G4_Hf
  specific = 4
FEATURE [App::DocumentObjectGroupPython] Ta_element001  label="Ta_element : 1"  # scripted group (container) (typed FeaturePython)
  n = 1
  ref = Ta_element
FEATURE [App::DocumentObjectGroupPython] G4_Ta  # scripted group (container) (typed FeaturePython)
  Dunit = g/cm3
  Dvalue = 16.654
  Group = -> [Ta_element001]
  conduct = 2
  density = 1
  expand = 3
  formula = Ta
  name = G4_Ta
  specific = 4
FEATURE [App::DocumentObjectGroupPython] W_element004  label="W_element : 004"  # scripted group (container) (typed FeaturePython)
  n = 1
  ref = W_element
FEATURE [App::DocumentObjectGroupPython] G4_W  # scripted group (container) (typed FeaturePython)
  Dunit = g/cm3
  Dvalue = 19.3
  Group = -> [W_element004]
  conduct = 2
  density = 1
  expand = 3
  formula = W
  name = G4_W
  specific = 4
FEATURE [App::DocumentObjectGroupPython] Re_element001  label="Re_element : 1"  # scripted group (container) (typed FeaturePython)
  n = 1
  ref = Re_element
FEATURE [App::DocumentObjectGroupPython] G4_Re  # scripted group (container) (typed FeaturePython)
  Dunit = g/cm3
  Dvalue = 21.02
  Group = -> [Re_element001]
  conduct = 2
  density = 1
  expand = 3
  formula = Re
  name = G4_Re
  specific = 4
FEATURE [App::DocumentObjectGroupPython] Os_element001  label="Os_element : 1"  # scripted group (container) (typed FeaturePython)
  n = 1
  ref = Os_element
FEATURE [App::DocumentObjectGroupPython] G4_Os  # scripted group (container) (typed FeaturePython)
  Dunit = g/cm3
  Dvalue = 22.57
  Group = -> [Os_element001]
  conduct = 2
  density = 1
  expand = 3
  formula = Os
  name = G4_Os
  specific = 4
FEATURE [App::DocumentObjectGroupPython] Ir_element001  label="Ir_element : 1"  # scripted group (container) (typed FeaturePython)
  n = 1
  ref = Ir_element
FEATURE [App::DocumentObjectGroupPython] G4_Ir  # scripted group (container) (typed FeaturePython)
  Dunit = g/cm3
  Dvalue = 22.42
  Group = -> [Ir_element001]
  conduct = 2
  density = 1
  expand = 3
  formula = Ir
  name = G4_Ir
  specific = 4
FEATURE [App::DocumentObjectGroupPython] Pt_element001  label="Pt_element : 1"  # scripted group (container) (typed FeaturePython)
  n = 1
  ref = Pt_element
FEATURE [App::DocumentObjectGroupPython] G4_Pt  # scripted group (container) (typed FeaturePython)
  Dunit = g/cm3
  Dvalue = 21.45
  Group = -> [Pt_element001]
  conduct = 2
  density = 1
  expand = 3
  formula = Pt
  name = G4_Pt
  specific = 4
FEATURE [App::DocumentObjectGroupPython] Au_element001  label="Au_element : 1"  # scripted group (container) (typed FeaturePython)
  n = 1
  ref = Au_element
FEATURE [App::DocumentObjectGroupPython] G4_Au  # scripted group (container) (typed FeaturePython)
  Dunit = g/cm3
  Dvalue = 19.32
  Group = -> [Au_element001]
  conduct = 2
  density = 1
  expand = 3
  formula = Au
  name = G4_Au
  specific = 4
FEATURE [App::DocumentObjectGroupPython] Hg_element002  label="Hg_element : 002"  # scripted group (container) (typed FeaturePython)
  n = 1
  ref = Hg_element
FEATURE [App::DocumentObjectGroupPython] G4_Hg  # scripted group (container) (typed FeaturePython)
  Dunit = g/cm3
  Dvalue = 13.546
  Group = -> [Hg_element002]
  conduct = 2
  density = 1
  expand = 3
  formula = Hg
  name = G4_Hg
  specific = 4
FEATURE [App::DocumentObjectGroupPython] Tl_element002  label="Tl_element : 002"  # scripted group (container) (typed FeaturePython)
  n = 1
  ref = Tl_element
FEATURE [App::DocumentObjectGroupPython] G4_Tl  # scripted group (container) (typed FeaturePython)
  Dunit = g/cm3
  Dvalue = 11.72
  Group = -> [Tl_element002]
  conduct = 2
  density = 1
  expand = 3
  formula = Tl
  name = G4_Tl
  specific = 4
FEATURE [App::DocumentObjectGroupPython] Pb_element003  label="Pb_element : 1"  # scripted group (container) (typed FeaturePython)
  n = 1
  ref = Pb_element
FEATURE [App::DocumentObjectGroupPython] G4_Pb  # scripted group (container) (typed FeaturePython)
  Dunit = g/cm3
  Dvalue = 11.35
  Group = -> [Pb_element003]
  conduct = 2
  density = 1
  expand = 3
  formula = Pb
  name = G4_Pb
  specific = 4
FEATURE [App::DocumentObjectGroupPython] Bi_element002  label="Bi_element : 1"  # scripted group (container) (typed FeaturePython)
  n = 1
  ref = Bi_element
FEATURE [App::DocumentObjectGroupPython] G4_Bi  # scripted group (container) (typed FeaturePython)
  Dunit = g/cm3
  Dvalue = 9.747
  Group = -> [Bi_element002]
  conduct = 2
  density = 1
  expand = 3
  formula = Bi
  name = G4_Bi
  specific = 4
FEATURE [App::DocumentObjectGroupPython] Po_element001  label="Po_element : 1"  # scripted group (container) (typed FeaturePython)
  n = 1
  ref = Po_element
FEATURE [App::DocumentObjectGroupPython] G4_Po  # scripted group (container) (typed FeaturePython)
  Dunit = g/cm3
  Dvalue = 9.32
  Group = -> [Po_element001]
  conduct = 2
  density = 1
  expand = 3
  formula = Po
  name = G4_Po
  specific = 4
FEATURE [App::DocumentObjectGroupPython] At_element001  label="At_element : 1"  # scripted group (container) (typed FeaturePython)
  n = 1
  ref = At_element
FEATURE [App::DocumentObjectGroupPython] G4_At  # scripted group (container) (typed FeaturePython)
  Dunit = g/cm3
  Dvalue = 9.32
  Group = -> [At_element001]
  conduct = 2
  density = 1
  expand = 3
  formula = At
  name = G4_At
  specific = 4
FEATURE [App::DocumentObjectGroupPython] Rn_element001  label="Rn_element : 1"  # scripted group (container) (typed FeaturePython)
  n = 1
  ref = Rn_element
FEATURE [App::DocumentObjectGroupPython] G4_Rn  # scripted group (container) (typed FeaturePython)
  Dunit = g/cm3
  Dvalue = 0.00900662
  Group = -> [Rn_element001]
  conduct = 2
  density = 1
  expand = 3
  formula = Rn
  name = G4_Rn
  specific = 4
FEATURE [App::DocumentObjectGroupPython] Fr_element001  label="Fr_element : 1"  # scripted group (container) (typed FeaturePython)
  n = 1
  ref = Fr_element
FEATURE [App::DocumentObjectGroupPython] G4_Fr  # scripted group (container) (typed FeaturePython)
  Dunit = g/cm3
  Dvalue = 1
  Group = -> [Fr_element001]
  conduct = 2
  density = 1
  expand = 3
  formula = Fr
  name = G4_Fr
  specific = 4
FEATURE [App::DocumentObjectGroupPython] Ra_element001  label="Ra_element : 1"  # scripted group (container) (typed FeaturePython)
  n = 1
  ref = Ra_element
FEATURE [App::DocumentObjectGroupPython] G4_Ra  # scripted group (container) (typed FeaturePython)
  Dunit = g/cm3
  Dvalue = 5
  Group = -> [Ra_element001]
  conduct = 2
  density = 1
  expand = 3
  formula = Ra
  name = G4_Ra
  specific = 4
FEATURE [App::DocumentObjectGroupPython] Ac_element001  label="Ac_element : 1"  # scripted group (container) (typed FeaturePython)
  n = 1
  ref = Ac_element
FEATURE [App::DocumentObjectGroupPython] G4_Ac  # scripted group (container) (typed FeaturePython)
  Dunit = g/cm3
  Dvalue = 10.07
  Group = -> [Ac_element001]
  conduct = 2
  density = 1
  expand = 3
  formula = Ac
  name = G4_Ac
  specific = 4
FEATURE [App::DocumentObjectGroupPython] Th_element001  label="Th_element : 1"  # scripted group (container) (typed FeaturePython)
  n = 1
  ref = Th_element
FEATURE [App::DocumentObjectGroupPython] G4_Th  # scripted group (container) (typed FeaturePython)
  Dunit = g/cm3
  Dvalue = 11.72
  Group = -> [Th_element001]
  conduct = 2
  density = 1
  expand = 3
  formula = Th
  name = G4_Th
  specific = 4
FEATURE [App::DocumentObjectGroupPython] Pa_element001  label="Pa_element : 1"  # scripted group (container) (typed FeaturePython)
  n = 1
  ref = Pa_element
FEATURE [App::DocumentObjectGroupPython] G4_Pa  # scripted group (container) (typed FeaturePython)
  Dunit = g/cm3
  Dvalue = 15.37
  Group = -> [Pa_element001]
  conduct = 2
  density = 1
  expand = 3
  formula = Pa
  name = G4_Pa
  specific = 4
FEATURE [App::DocumentObjectGroupPython] U_element004  label="U_element : 004"  # scripted group (container) (typed FeaturePython)
  n = 1
  ref = U_element
FEATURE [App::DocumentObjectGroupPython] G4_U  # scripted group (container) (typed FeaturePython)
  Dunit = g/cm3
  Dvalue = 18.95
  Group = -> [U_element004]
  conduct = 2
  density = 1
  expand = 3
  formula = U
  name = G4_U
  specific = 4
FEATURE [App::DocumentObjectGroupPython] Np_element001  label="Np_element : 1"  # scripted group (container) (typed FeaturePython)
  n = 1
  ref = Np_element
FEATURE [App::DocumentObjectGroupPython] G4_Np  # scripted group (container) (typed FeaturePython)
  Dunit = g/cm3
  Dvalue = 20.25
  Group = -> [Np_element001]
  conduct = 2
  density = 1
  expand = 3
  formula = Np
  name = G4_Np
  specific = 4
FEATURE [App::DocumentObjectGroupPython] Pu_element002  label="Pu_element : 002"  # scripted group (container) (typed FeaturePython)
  n = 1
  ref = Pu_element
FEATURE [App::DocumentObjectGroupPython] G4_Pu  # scripted group (container) (typed FeaturePython)
  Dunit = g/cm3
  Dvalue = 19.84
  Group = -> [Pu_element002]
  conduct = 2
  density = 1
  expand = 3
  formula = Pu
  name = G4_Pu
  specific = 4
FEATURE [App::DocumentObjectGroupPython] Am_element001  label="Am_element : 1"  # scripted group (container) (typed FeaturePython)
  n = 1
  ref = Am_element
FEATURE [App::DocumentObjectGroupPython] G4_Am  # scripted group (container) (typed FeaturePython)
  Dunit = g/cm3
  Dvalue = 13.67
  Group = -> [Am_element001]
  conduct = 2
  density = 1
  expand = 3
  formula = Am
  name = G4_Am
  specific = 4
FEATURE [App::DocumentObjectGroupPython] Cm_element001  label="Cm_element : 1"  # scripted group (container) (typed FeaturePython)
  n = 1
  ref = Cm_element
FEATURE [App::DocumentObjectGroupPython] G4_Cm  # scripted group (container) (typed FeaturePython)
  Dunit = g/cm3
  Dvalue = 13.51
  Group = -> [Cm_element001]
  conduct = 2
  density = 1
  expand = 3
  formula = Cm
  name = G4_Cm
  specific = 4
FEATURE [App::DocumentObjectGroupPython] Bk_element001  label="Bk_element : 1"  # scripted group (container) (typed FeaturePython)
  n = 1
  ref = Bk_element
FEATURE [App::DocumentObjectGroupPython] G4_Bk  # scripted group (container) (typed FeaturePython)
  Dunit = g/cm3
  Dvalue = 14
  Group = -> [Bk_element001]
  conduct = 2
  density = 1
  expand = 3
  formula = Bk
  name = G4_Bk
  specific = 4
FEATURE [App::DocumentObjectGroupPython] Cf_element001  label="Cf_element : 1"  # scripted group (container) (typed FeaturePython)
  n = 1
  ref = Cf_element
FEATURE [App::DocumentObjectGroupPython] G4_Cf  # scripted group (container) (typed FeaturePython)
  Dunit = g/cm3
  Dvalue = 10
  Group = -> [Cf_element001]
  conduct = 2
  density = 1
  expand = 3
  formula = Cf
  name = G4_Cf
  specific = 4
FEATURE [App::DocumentObjectGroupPython] Element  # scripted group (container) (typed FeaturePython)
  Group = -> [G4_H,G4_He,G4_Li,G4_Be,G4_B,G4_C,G4_N,G4_O,G4_F,G4_Ne,G4_Na,G4_Mg,G4_Al,G4_Si,G4_P,G4_S,G4_Cl,G4_Ar,G4_K,G4_Ca,G4_Sc,G4_Ti,G4_V,G4_Cr,G4_Mn,G4_Fe,G4_Co,G4_Ni,G4_Cu,G4_Zn,G4_Ga,G4_Ge,G4_As,G4_Se,G4_Br,G4_Kr,G4_Rb,G4_Sr,G4_Y,G4_Zr,G4_Nb,G4_Mo,G4_Tc,G4_Ru,G4_Rh,G4_Pd,G4_Ag,G4_Cd,G4_In,G4_Sn,G4_Sb,G4_Te,G4_I,G4_Xe,G4_Cs,G4_Ba,G4_La,G4_Ce,G4_Pr,G4_Nd,G4_Pm,G4_Sm,G4_Eu,G4_Gd,G4_Tb,G4_Dy,G4_Ho,G4_Er,+30 more]
FEATURE [App::DocumentObjectGroupPython] H_element114  label="H_element : 063"  # scripted group (container) (typed FeaturePython)
  n = 2
  ref = H_element
FEATURE [App::DocumentObjectGroupPython] G4_lH2  # scripted group (container) (typed FeaturePython)
  Dunit = g/cm3
  Dvalue = 0.0708
  Group = -> [H_element114]
  conduct = 2
  density = 1
  expand = 3
  formula = G4_lH2
  name = G4_lH2
  specific = 4
FEATURE [App::DocumentObjectGroupPython] N_element049  label="N_element : 022"  # scripted group (container) (typed FeaturePython)
  n = 2
  ref = N_element
FEATURE [App::DocumentObjectGroupPython] G4_lN2  # scripted group (container) (typed FeaturePython)
  Dunit = g/cm3
  Dvalue = 0.807
  Group = -> [N_element049]
  conduct = 2
  density = 1
  expand = 3
  formula = G4_lN2
  name = G4_lN2
  specific = 4
FEATURE [App::DocumentObjectGroupPython] O_element106  label="O_element : 060"  # scripted group (container) (typed FeaturePython)
  n = 2
  ref = O_element
FEATURE [App::DocumentObjectGroupPython] G4_lO2  # scripted group (container) (typed FeaturePython)
  Dunit = g/cm3
  Dvalue = 1.141
  Group = -> [O_element106]
  conduct = 2
  density = 1
  expand = 3
  formula = G4_lO2
  name = G4_lO2
  specific = 4
FEATURE [App::DocumentObjectGroupPython] Ar  label="Ar : 1"  # scripted group (container) (typed FeaturePython)
  n = 1
  ref = Ar
FEATURE [App::DocumentObjectGroupPython] G4_lAr  # scripted group (container) (typed FeaturePython)
  Dunit = g/cm3
  Dvalue = 1.396
  Group = -> [Ar]
  conduct = 2
  density = 1
  expand = 3
  formula = G4_lAr
  name = G4_lAr
  specific = 4
FEATURE [App::DocumentObjectGroupPython] Br  label="Br : 1"  # scripted group (container) (typed FeaturePython)
  n = 1
  ref = Br
FEATURE [App::DocumentObjectGroupPython] G4_lBr  # scripted group (container) (typed FeaturePython)
  Dunit = g/cm3
  Dvalue = 3.1028
  Group = -> [Br]
  conduct = 2
  density = 1
  expand = 3
  formula = G4_lBr
  name = G4_lBr
  specific = 4
FEATURE [App::DocumentObjectGroupPython] Kr  label="Kr : 1"  # scripted group (container) (typed FeaturePython)
  n = 1
  ref = Kr
FEATURE [App::DocumentObjectGroupPython] G4_lKr  # scripted group (container) (typed FeaturePython)
  Dunit = g/cm3
  Dvalue = 2.418
  Group = -> [Kr]
  conduct = 2
  density = 1
  expand = 3
  formula = G4_lKr
  name = G4_lKr
  specific = 4
FEATURE [App::DocumentObjectGroupPython] Xe  label="Xe : 1"  # scripted group (container) (typed FeaturePython)
  n = 1
  ref = Xe
FEATURE [App::DocumentObjectGroupPython] G4_lXe  # scripted group (container) (typed FeaturePython)
  Dunit = g/cm3
  Dvalue = 2.953
  Group = -> [Xe]
  conduct = 2
  density = 1
  expand = 3
  formula = G4_lXe
  name = G4_lXe
  specific = 4
FEATURE [App::DocumentObjectGroupPython] O_element107  label="O_element : 061"  # scripted group (container) (typed FeaturePython)
  n = 4
  ref = O_element
FEATURE [App::DocumentObjectGroupPython] Pb_element004  label="Pb_element : 002"  # scripted group (container) (typed FeaturePython)
  n = 1
  ref = Pb_element
FEATURE [App::DocumentObjectGroupPython] W_element005  label="W_element : 005"  # scripted group (container) (typed FeaturePython)
  n = 1
  ref = W_element
FEATURE [App::DocumentObjectGroupPython] G4_PbWO4  # scripted group (container) (typed FeaturePython)
  Dunit = g/cm3
  Dvalue = 8.28
  Group = -> [O_element107,Pb_element004,W_element005]
  conduct = 2
  density = 1
  expand = 3
  formula = G4_PbWO4
  name = G4_PbWO4
  specific = 4
FEATURE [App::DocumentObjectGroupPython] alactic  label="alactic : 1"  # scripted group (container) (typed FeaturePython)
  n = 1
  ref = alactic
FEATURE [App::DocumentObjectGroupPython] G4_Galactic  # scripted group (container) (typed FeaturePython)
  Dunit = g/cm3
  Dvalue = 0
  Group = -> [alactic]
  conduct = 2
  density = 1
  expand = 3
  formula = G4_Galactic
  name = G4_Galactic
  specific = 4
FEATURE [App::DocumentObjectGroupPython] RAPHITE_POROUS  label="RAPHITE_POROUS : 1"  # scripted group (container) (typed FeaturePython)
  n = 1
  ref = RAPHITE_POROUS
FEATURE [App::DocumentObjectGroupPython] G4_GRAPHITE_POROUS  # scripted group (container) (typed FeaturePython)
  Dunit = g/cm3
  Dvalue = 1.7
  Group = -> [RAPHITE_POROUS]
  conduct = 2
  density = 1
  expand = 3
  formula = G4_GRAPHITE_POROUS
  name = G4_GRAPHITE_POROUS
  specific = 4
FEATURE [App::DocumentObjectGroupPython] H_element115  label="H_element : 0.150"  # scripted group (container) (typed FeaturePython)
  n = 0.080538
FEATURE [App::DocumentObjectGroupPython] C_element125  label="C_element : 0.600"  # scripted group (container) (typed FeaturePython)
  n = 0.599848
FEATURE [App::DocumentObjectGroupPython] O_element108  label="O_element : 0.320"  # scripted group (container) (typed FeaturePython)
  n = 0.319614
FEATURE [App::DocumentObjectGroupPython] G4_LUCITE  # scripted group (container) (typed FeaturePython)
  Dunit = g/cm3
  Dvalue = 1.19
  Group = -> [H_element115,C_element125,O_element108]
  conduct = 2
  density = 1
  expand = 3
  formula = G4_LUCITE
  name = G4_LUCITE
  specific = 4
FEATURE [App::DocumentObjectGroupPython] Cu_element002  label="Cu_element : 62"  # scripted group (container) (typed FeaturePython)
  n = 62
  ref = Cu_element
FEATURE [App::DocumentObjectGroupPython] Zn_element002  label="Zn_element : 35"  # scripted group (container) (typed FeaturePython)
  n = 35
  ref = Zn_element
FEATURE [App::DocumentObjectGroupPython] Pb_element005  label="Pb_element : 3"  # scripted group (container) (typed FeaturePython)
  n = 3
  ref = Pb_element
FEATURE [App::DocumentObjectGroupPython] G4_BRASS  # scripted group (container) (typed FeaturePython)
  Dunit = g/cm3
  Dvalue = 8.52
  Group = -> [Cu_element002,Zn_element002,Pb_element005]
  conduct = 2
  density = 1
  expand = 3
  formula = G4_BRASS
  name = G4_BRASS
  specific = 4
FEATURE [App::DocumentObjectGroupPython] Cu_element003  label="Cu_element : 89"  # scripted group (container) (typed FeaturePython)
  n = 89
  ref = Cu_element
FEATURE [App::DocumentObjectGroupPython] Zn_element003  label="Zn_element : 9"  # scripted group (container) (typed FeaturePython)
  n = 9
  ref = Zn_element
FEATURE [App::DocumentObjectGroupPython] Pb_element006  label="Pb_element : 2"  # scripted group (container) (typed FeaturePython)
  n = 2
  ref = Pb_element
FEATURE [App::DocumentObjectGroupPython] G4_BRONZE  # scripted group (container) (typed FeaturePython)
  Dunit = g/cm3
  Dvalue = 8.82
  Group = -> [Cu_element003,Zn_element003,Pb_element006]
  conduct = 2
  density = 1
  expand = 3
  formula = G4_BRONZE
  name = G4_BRONZE
  specific = 4
FEATURE [App::DocumentObjectGroupPython] Fe_element008  label="Fe_element : 74"  # scripted group (container) (typed FeaturePython)
  n = 74
  ref = Fe_element
FEATURE [App::DocumentObjectGroupPython] Cr_element002  label="Cr_element : 18"  # scripted group (container) (typed FeaturePython)
  n = 18
  ref = Cr_element
FEATURE [App::DocumentObjectGroupPython] Ni_element002  label="Ni_element : 8"  # scripted group (container) (typed FeaturePython)
  n = 8
  ref = Ni_element
FEATURE [App::DocumentObjectGroupPython] G4_STAINLESS_STEEL  label="G4_STAINLESS-STEEL"  # scripted group (container) (typed FeaturePython)
  Dunit = g/cm3
  Dvalue = 8
  Group = -> [Fe_element008,Cr_element002,Ni_element002]
  conduct = 2
  density = 1
  expand = 3
  formula = G4_STAINLESS-STEEL
  name = G4_STAINLESS-STEEL
  specific = 4
FEATURE [App::DocumentObjectGroupPython] H_element116  label="H_element : 064"  # scripted group (container) (typed FeaturePython)
  n = 18
  ref = H_element
FEATURE [App::DocumentObjectGroupPython] C_element126  label="C_element : 071"  # scripted group (container) (typed FeaturePython)
  n = 12
  ref = C_element
FEATURE [App::DocumentObjectGroupPython] O_element109  label="O_element : 062"  # scripted group (container) (typed FeaturePython)
  n = 7
  ref = O_element
FEATURE [App::DocumentObjectGroupPython] G4_CR39  # scripted group (container) (typed FeaturePython)
  Dunit = g/cm3
  Dvalue = 1.32
  Group = -> [H_element116,C_element126,O_element109]
  conduct = 2
  density = 1
  expand = 3
  formula = G4_CR39
  name = G4_CR39
  specific = 4
FEATURE [App::DocumentObjectGroupPython] H_element117  label="H_element : 38"  # scripted group (container) (typed FeaturePython)
  n = 38
  ref = H_element
FEATURE [App::DocumentObjectGroupPython] C_element127  label="C_element : 072"  # scripted group (container) (typed FeaturePython)
  n = 18
  ref = C_element
FEATURE [App::DocumentObjectGroupPython] O_element110  label="O_element : 063"  # scripted group (container) (typed FeaturePython)
  n = 1
  ref = O_element
FEATURE [App::DocumentObjectGroupPython] G4_OCTADECANOL  # scripted group (container) (typed FeaturePython)
  Dunit = g/cm3
  Dvalue = 0.812
  Group = -> [H_element117,C_element127,O_element110]
  conduct = 2
  density = 1
  expand = 3
  formula = G4_OCTADECANOL
  name = G4_OCTADECANOL
  specific = 4
FEATURE [App::DocumentObjectGroupPython] HEP  # scripted group (container) (typed FeaturePython)
  Group = -> [G4_lH2,G4_lN2,G4_lO2,G4_lAr,G4_lBr,G4_lKr,G4_lXe,G4_PbWO4,G4_Galactic,G4_GRAPHITE_POROUS,G4_LUCITE,G4_BRASS,G4_BRONZE,G4_STAINLESS_STEEL,G4_CR39,G4_OCTADECANOL]
FEATURE [App::DocumentObjectGroupPython] C_element128  label="C_element : 073"  # scripted group (container) (typed FeaturePython)
  n = 14
  ref = C_element
FEATURE [App::DocumentObjectGroupPython] H_element118  label="H_element : 065"  # scripted group (container) (typed FeaturePython)
  n = 10
  ref = H_element
FEATURE [App::DocumentObjectGroupPython] O_element111  label="O_element : 064"  # scripted group (container) (typed FeaturePython)
  n = 2
  ref = O_element
FEATURE [App::DocumentObjectGroupPython] N_element050  label="N_element : 023"  # scripted group (container) (typed FeaturePython)
  n = 2
  ref = N_element
FEATURE [App::DocumentObjectGroupPython] G4_KEVLAR  # scripted group (container) (typed FeaturePython)
  Dunit = g/cm3
  Dvalue = 1.44
  Group = -> [C_element128,H_element118,O_element111,N_element050]
  conduct = 2
  density = 1
  expand = 3
  formula = G4_KEVLAR
  name = G4_KEVLAR
  specific = 4
FEATURE [App::DocumentObjectGroupPython] C_element129  label="C_element : 074"  # scripted group (container) (typed FeaturePython)
  n = 10
  ref = C_element
FEATURE [App::DocumentObjectGroupPython] H_element119  label="H_element : 066"  # scripted group (container) (typed FeaturePython)
  n = 8
  ref = H_element
FEATURE [App::DocumentObjectGroupPython] O_element112  label="O_element : 065"  # scripted group (container) (typed FeaturePython)
  n = 4
  ref = O_element
FEATURE [App::DocumentObjectGroupPython] G4_DACRON  # scripted group (container) (typed FeaturePython)
  Dunit = g/cm3
  Dvalue = 1.4
  Group = -> [C_element129,H_element119,O_element112]
  conduct = 2
  density = 1
  expand = 3
  formula = G4_DACRON
  name = G4_DACRON
  specific = 4
FEATURE [App::DocumentObjectGroupPython] C_element130  label="C_element : 075"  # scripted group (container) (typed FeaturePython)
  n = 4
  ref = C_element
FEATURE [App::DocumentObjectGroupPython] H_element120  label="H_element : 067"  # scripted group (container) (typed FeaturePython)
  n = 5
  ref = H_element
FEATURE [App::DocumentObjectGroupPython] Cl_element030  label="Cl_element : 016"  # scripted group (container) (typed FeaturePython)
  n = 1
  ref = Cl_element
FEATURE [App::DocumentObjectGroupPython] G4_NEOPRENE  # scripted group (container) (typed FeaturePython)
  Dunit = g/cm3
  Dvalue = 1.23
  Group = -> [C_element130,H_element120,Cl_element030]
  conduct = 2
  density = 1
  expand = 3
  formula = G4_NEOPRENE
  name = G4_NEOPRENE
  specific = 4
FEATURE [App::DocumentObjectGroupPython] Space  # scripted group (container) (typed FeaturePython)
  Group = -> [G4_KEVLAR,G4_DACRON,G4_NEOPRENE]
FEATURE [App::DocumentObjectGroupPython] H_element121  label="H_element : 068"  # scripted group (container) (typed FeaturePython)
  n = 5
  ref = H_element
FEATURE [App::DocumentObjectGroupPython] C_element131  label="C_element : 076"  # scripted group (container) (typed FeaturePython)
  n = 4
  ref = C_element
FEATURE [App::DocumentObjectGroupPython] N_element051  label="N_element : 3"  # scripted group (container) (typed FeaturePython)
  n = 3
  ref = N_element
FEATURE [App::DocumentObjectGroupPython] O_element113  label="O_element : 066"  # scripted group (container) (typed FeaturePython)
  n = 1
  ref = O_element
FEATURE [App::DocumentObjectGroupPython] G4_CYTOSINE  # scripted group (container) (typed FeaturePython)
  Dunit = g/cm3
  Dvalue = 1.55
  Group = -> [H_element121,C_element131,N_element051,O_element113]
  conduct = 2
  density = 1
  expand = 3
  formula = G4_CYTOSINE
  name = G4_CYTOSINE
  specific = 4
FEATURE [App::DocumentObjectGroupPython] H_element122  label="H_element : 069"  # scripted group (container) (typed FeaturePython)
  n = 6
  ref = H_element
FEATURE [App::DocumentObjectGroupPython] C_element132  label="C_element : 077"  # scripted group (container) (typed FeaturePython)
  n = 5
  ref = C_element
FEATURE [App::DocumentObjectGroupPython] N_element052  label="N_element : 024"  # scripted group (container) (typed FeaturePython)
  n = 2
  ref = N_element
FEATURE [App::DocumentObjectGroupPython] O_element114  label="O_element : 067"  # scripted group (container) (typed FeaturePython)
  n = 2
  ref = O_element
FEATURE [App::DocumentObjectGroupPython] G4_THYMINE  # scripted group (container) (typed FeaturePython)
  Dunit = g/cm3
  Dvalue = 1.23
  Group = -> [H_element122,C_element132,N_element052,O_element114]
  conduct = 2
  density = 1
  expand = 3
  formula = G4_THYMINE
  name = G4_THYMINE
  specific = 4
FEATURE [App::DocumentObjectGroupPython] H_element123  label="H_element : 070"  # scripted group (container) (typed FeaturePython)
  n = 4
  ref = H_element
FEATURE [App::DocumentObjectGroupPython] C_element133  label="C_element : 078"  # scripted group (container) (typed FeaturePython)
  n = 4
  ref = C_element
FEATURE [App::DocumentObjectGroupPython] N_element053  label="N_element : 025"  # scripted group (container) (typed FeaturePython)
  n = 2
  ref = N_element
FEATURE [App::DocumentObjectGroupPython] O_element115  label="O_element : 068"  # scripted group (container) (typed FeaturePython)
  n = 2
  ref = O_element
FEATURE [App::DocumentObjectGroupPython] G4_URACIL  # scripted group (container) (typed FeaturePython)
  Dunit = g/cm3
  Dvalue = 1.32
  Group = -> [H_element123,C_element133,N_element053,O_element115]
  conduct = 2
  density = 1
  expand = 3
  formula = G4_URACIL
  name = G4_URACIL
  specific = 4
FEATURE [App::DocumentObjectGroupPython] H_element124  label="H_element : 071"  # scripted group (container) (typed FeaturePython)
  n = 4
  ref = H_element
FEATURE [App::DocumentObjectGroupPython] C_element134  label="C_element : 079"  # scripted group (container) (typed FeaturePython)
  n = 5
  ref = C_element
FEATURE [App::DocumentObjectGroupPython] N_element054  label="N_element : 026"  # scripted group (container) (typed FeaturePython)
  n = 5
  ref = N_element
FEATURE [App::DocumentObjectGroupPython] G4_DNA_ADENINE  # scripted group (container) (typed FeaturePython)
  Dunit = g/cm3
  Dvalue = 1
  Group = -> [H_element124,C_element134,N_element054]
  conduct = 2
  density = 1
  expand = 3
  formula = G4_DNA_ADENINE
  name = G4_DNA_ADENINE
  specific = 4
FEATURE [App::DocumentObjectGroupPython] H_element125  label="H_element : 072"  # scripted group (container) (typed FeaturePython)
  n = 4
  ref = H_element
FEATURE [App::DocumentObjectGroupPython] C_element135  label="C_element : 080"  # scripted group (container) (typed FeaturePython)
  n = 5
  ref = C_element
FEATURE [App::DocumentObjectGroupPython] N_element055  label="N_element : 027"  # scripted group (container) (typed FeaturePython)
  n = 5
  ref = N_element
FEATURE [App::DocumentObjectGroupPython] O_element116  label="O_element : 069"  # scripted group (container) (typed FeaturePython)
  n = 1
  ref = O_element
FEATURE [App::DocumentObjectGroupPython] G4_DNA_GUANINE  # scripted group (container) (typed FeaturePython)
  Dunit = g/cm3
  Dvalue = 1
  Group = -> [H_element125,C_element135,N_element055,O_element116]
  conduct = 2
  density = 1
  expand = 3
  formula = G4_DNA_GUANINE
  name = G4_DNA_GUANINE
  specific = 4
FEATURE [App::DocumentObjectGroupPython] H_element126  label="H_element : 073"  # scripted group (container) (typed FeaturePython)
  n = 4
  ref = H_element
FEATURE [App::DocumentObjectGroupPython] C_element136  label="C_element : 081"  # scripted group (container) (typed FeaturePython)
  n = 4
  ref = C_element
FEATURE [App::DocumentObjectGroupPython] N_element056  label="N_element : 028"  # scripted group (container) (typed FeaturePython)
  n = 3
  ref = N_element
FEATURE [App::DocumentObjectGroupPython] O_element117  label="O_element : 070"  # scripted group (container) (typed FeaturePython)
  n = 1
  ref = O_element
FEATURE [App::DocumentObjectGroupPython] G4_DNA_CYTOSINE  # scripted group (container) (typed FeaturePython)
  Dunit = g/cm3
  Dvalue = 1
  Group = -> [H_element126,C_element136,N_element056,O_element117]
  conduct = 2
  density = 1
  expand = 3
  formula = G4_DNA_CYTOSINE
  name = G4_DNA_CYTOSINE
  specific = 4
FEATURE [App::DocumentObjectGroupPython] H_element127  label="H_element : 074"  # scripted group (container) (typed FeaturePython)
  n = 5
  ref = H_element
FEATURE [App::DocumentObjectGroupPython] C_element137  label="C_element : 082"  # scripted group (container) (typed FeaturePython)
  n = 5
  ref = C_element
FEATURE [App::DocumentObjectGroupPython] N_element057  label="N_element : 029"  # scripted group (container) (typed FeaturePython)
  n = 2
  ref = N_element
FEATURE [App::DocumentObjectGroupPython] O_element118  label="O_element : 071"  # scripted group (container) (typed FeaturePython)
  n = 2
  ref = O_element
FEATURE [App::DocumentObjectGroupPython] G4_DNA_THYMINE  # scripted group (container) (typed FeaturePython)
  Dunit = g/cm3
  Dvalue = 1
  Group = -> [H_element127,C_element137,N_element057,O_element118]
  conduct = 2
  density = 1
  expand = 3
  formula = G4_DNA_THYMINE
  name = G4_DNA_THYMINE
  specific = 4
FEATURE [App::DocumentObjectGroupPython] H_element128  label="H_element : 075"  # scripted group (container) (typed FeaturePython)
  n = 3
  ref = H_element
FEATURE [App::DocumentObjectGroupPython] C_element138  label="C_element : 083"  # scripted group (container) (typed FeaturePython)
  n = 4
  ref = C_element
FEATURE [App::DocumentObjectGroupPython] N_element058  label="N_element : 030"  # scripted group (container) (typed FeaturePython)
  n = 2
  ref = N_element
FEATURE [App::DocumentObjectGroupPython] O_element119  label="O_element : 072"  # scripted group (container) (typed FeaturePython)
  n = 2
  ref = O_element
FEATURE [App::DocumentObjectGroupPython] G4_DNA_URACIL  # scripted group (container) (typed FeaturePython)
  Dunit = g/cm3
  Dvalue = 1
  Group = -> [H_element128,C_element138,N_element058,O_element119]
  conduct = 2
  density = 1
  expand = 3
  formula = G4_DNA_URACIL
  name = G4_DNA_URACIL
  specific = 4
FEATURE [App::DocumentObjectGroupPython] H_element129  label="H_element : 076"  # scripted group (container) (typed FeaturePython)
  n = 10
  ref = H_element
FEATURE [App::DocumentObjectGroupPython] C_element139  label="C_element : 084"  # scripted group (container) (typed FeaturePython)
  n = 10
  ref = C_element
FEATURE [App::DocumentObjectGroupPython] N_element059  label="N_element : 031"  # scripted group (container) (typed FeaturePython)
  n = 5
  ref = N_element
FEATURE [App::DocumentObjectGroupPython] O_element120  label="O_element : 073"  # scripted group (container) (typed FeaturePython)
  n = 4
  ref = O_element
FEATURE [App::DocumentObjectGroupPython] G4_DNA_ADENOSINE  # scripted group (container) (typed FeaturePython)
  Dunit = g/cm3
  Dvalue = 1
  Group = -> [H_element129,C_element139,N_element059,O_element120]
  conduct = 2
  density = 1
  expand = 3
  formula = G4_DNA_ADENOSINE
  name = G4_DNA_ADENOSINE
  specific = 4
FEATURE [App::DocumentObjectGroupPython] H_element130  label="H_element : 077"  # scripted group (container) (typed FeaturePython)
  n = 10
  ref = H_element
FEATURE [App::DocumentObjectGroupPython] C_element140  label="C_element : 085"  # scripted group (container) (typed FeaturePython)
  n = 10
  ref = C_element
FEATURE [App::DocumentObjectGroupPython] N_element060  label="N_element : 032"  # scripted group (container) (typed FeaturePython)
  n = 5
  ref = N_element
FEATURE [App::DocumentObjectGroupPython] O_element121  label="O_element : 074"  # scripted group (container) (typed FeaturePython)
  n = 5
  ref = O_element
FEATURE [App::DocumentObjectGroupPython] G4_DNA_GUANOSINE  # scripted group (container) (typed FeaturePython)
  Dunit = g/cm3
  Dvalue = 1
  Group = -> [H_element130,C_element140,N_element060,O_element121]
  conduct = 2
  density = 1
  expand = 3
  formula = G4_DNA_GUANOSINE
  name = G4_DNA_GUANOSINE
  specific = 4
FEATURE [App::DocumentObjectGroupPython] H_element131  label="H_element : 078"  # scripted group (container) (typed FeaturePython)
  n = 10
  ref = H_element
FEATURE [App::DocumentObjectGroupPython] C_element141  label="C_element : 086"  # scripted group (container) (typed FeaturePython)
  n = 9
  ref = C_element
FEATURE [App::DocumentObjectGroupPython] N_element061  label="N_element : 033"  # scripted group (container) (typed FeaturePython)
  n = 3
  ref = N_element
FEATURE [App::DocumentObjectGroupPython] O_element122  label="O_element : 075"  # scripted group (container) (typed FeaturePython)
  n = 5
  ref = O_element
FEATURE [App::DocumentObjectGroupPython] G4_DNA_CYTIDINE  # scripted group (container) (typed FeaturePython)
  Dunit = g/cm3
  Dvalue = 1
  Group = -> [H_element131,C_element141,N_element061,O_element122]
  conduct = 2
  density = 1
  expand = 3
  formula = G4_DNA_CYTIDINE
  name = G4_DNA_CYTIDINE
  specific = 4
FEATURE [App::DocumentObjectGroupPython] H_element132  label="H_element : 079"  # scripted group (container) (typed FeaturePython)
  n = 9
  ref = H_element
FEATURE [App::DocumentObjectGroupPython] C_element142  label="C_element : 087"  # scripted group (container) (typed FeaturePython)
  n = 9
  ref = C_element
FEATURE [App::DocumentObjectGroupPython] N_element062  label="N_element : 034"  # scripted group (container) (typed FeaturePython)
  n = 2
  ref = N_element
FEATURE [App::DocumentObjectGroupPython] O_element123  label="O_element : 076"  # scripted group (container) (typed FeaturePython)
  n = 6
  ref = O_element
FEATURE [App::DocumentObjectGroupPython] G4_DNA_URIDINE  # scripted group (container) (typed FeaturePython)
  Dunit = g/cm3
  Dvalue = 1
  Group = -> [H_element132,C_element142,N_element062,O_element123]
  conduct = 2
  density = 1
  expand = 3
  formula = G4_DNA_URIDINE
  name = G4_DNA_URIDINE
  specific = 4
FEATURE [App::DocumentObjectGroupPython] H_element133  label="H_element : 080"  # scripted group (container) (typed FeaturePython)
  n = 11
  ref = H_element
FEATURE [App::DocumentObjectGroupPython] C_element143  label="C_element : 088"  # scripted group (container) (typed FeaturePython)
  n = 10
  ref = C_element
FEATURE [App::DocumentObjectGroupPython] N_element063  label="N_element : 035"  # scripted group (container) (typed FeaturePython)
  n = 2
  ref = N_element
FEATURE [App::DocumentObjectGroupPython] O_element124  label="O_element : 077"  # scripted group (container) (typed FeaturePython)
  n = 6
  ref = O_element
FEATURE [App::DocumentObjectGroupPython] G4_DNA_METHYLURIDINE  # scripted group (container) (typed FeaturePython)
  Dunit = g/cm3
  Dvalue = 1
  Group = -> [H_element133,C_element143,N_element063,O_element124]
  conduct = 2
  density = 1
  expand = 3
  formula = G4_DNA_METHYLURIDINE
  name = G4_DNA_METHYLURIDINE
  specific = 4
FEATURE [App::DocumentObjectGroupPython] P_element014  label="P_element : 003"  # scripted group (container) (typed FeaturePython)
  n = 1
  ref = P_element
FEATURE [App::DocumentObjectGroupPython] O_element125  label="O_element : 078"  # scripted group (container) (typed FeaturePython)
  n = 3
  ref = O_element
FEATURE [App::DocumentObjectGroupPython] G4_DNA_MONOPHOSPHATE  # scripted group (container) (typed FeaturePython)
  Dunit = g/cm3
  Dvalue = 1
  Group = -> [P_element014,O_element125]
  conduct = 2
  density = 1
  expand = 3
  formula = G4_DNA_MONOPHOSPHATE
  name = G4_DNA_MONOPHOSPHATE
  specific = 4
FEATURE [App::DocumentObjectGroupPython] H_element134  label="H_element : 081"  # scripted group (container) (typed FeaturePython)
  n = 10
  ref = H_element
FEATURE [App::DocumentObjectGroupPython] C_element144  label="C_element : 089"  # scripted group (container) (typed FeaturePython)
  n = 10
  ref = C_element
FEATURE [App::DocumentObjectGroupPython] N_element064  label="N_element : 036"  # scripted group (container) (typed FeaturePython)
  n = 5
  ref = N_element
FEATURE [App::DocumentObjectGroupPython] O_element126  label="O_element : 079"  # scripted group (container) (typed FeaturePython)
  n = 7
  ref = O_element
FEATURE [App::DocumentObjectGroupPython] P_element015  label="P_element : 004"  # scripted group (container) (typed FeaturePython)
  n = 1
  ref = P_element
FEATURE [App::DocumentObjectGroupPython] G4_DNA_A  # scripted group (container) (typed FeaturePython)
  Dunit = g/cm3
  Dvalue = 1
  Group = -> [H_element134,C_element144,N_element064,O_element126,P_element015]
  conduct = 2
  density = 1
  expand = 3
  formula = G4_DNA_A
  name = G4_DNA_A
  specific = 4
FEATURE [App::DocumentObjectGroupPython] H_element135  label="H_element : 082"  # scripted group (container) (typed FeaturePython)
  n = 10
  ref = H_element
FEATURE [App::DocumentObjectGroupPython] C_element145  label="C_element : 090"  # scripted group (container) (typed FeaturePython)
  n = 10
  ref = C_element
FEATURE [App::DocumentObjectGroupPython] N_element065  label="N_element : 037"  # scripted group (container) (typed FeaturePython)
  n = 5
  ref = N_element
FEATURE [App::DocumentObjectGroupPython] O_element127  label="O_element : 8"  # scripted group (container) (typed FeaturePython)
  n = 8
  ref = O_element
FEATURE [App::DocumentObjectGroupPython] P_element016  label="P_element : 005"  # scripted group (container) (typed FeaturePython)
  n = 1
  ref = P_element
FEATURE [App::DocumentObjectGroupPython] G4_DNA_G  # scripted group (container) (typed FeaturePython)
  Dunit = g/cm3
  Dvalue = 1
  Group = -> [H_element135,C_element145,N_element065,O_element127,P_element016]
  conduct = 2
  density = 1
  expand = 3
  formula = G4_DNA_G
  name = G4_DNA_G
  specific = 4
FEATURE [App::DocumentObjectGroupPython] H_element136  label="H_element : 083"  # scripted group (container) (typed FeaturePython)
  n = 10
  ref = H_element
FEATURE [App::DocumentObjectGroupPython] C_element146  label="C_element : 091"  # scripted group (container) (typed FeaturePython)
  n = 9
  ref = C_element
FEATURE [App::DocumentObjectGroupPython] N_element066  label="N_element : 038"  # scripted group (container) (typed FeaturePython)
  n = 3
  ref = N_element
FEATURE [App::DocumentObjectGroupPython] O_element128  label="O_element : 080"  # scripted group (container) (typed FeaturePython)
  n = 8
  ref = O_element
FEATURE [App::DocumentObjectGroupPython] P_element017  label="P_element : 006"  # scripted group (container) (typed FeaturePython)
  n = 1
  ref = P_element
FEATURE [App::DocumentObjectGroupPython] G4_DNA_C  # scripted group (container) (typed FeaturePython)
  Dunit = g/cm3
  Dvalue = 1
  Group = -> [H_element136,C_element146,N_element066,O_element128,P_element017]
  conduct = 2
  density = 1
  expand = 3
  formula = G4_DNA_C
  name = G4_DNA_C
  specific = 4
FEATURE [App::DocumentObjectGroupPython] H_element137  label="H_element : 084"  # scripted group (container) (typed FeaturePython)
  n = 9
  ref = H_element
FEATURE [App::DocumentObjectGroupPython] C_element147  label="C_element : 092"  # scripted group (container) (typed FeaturePython)
  n = 9
  ref = C_element
FEATURE [App::DocumentObjectGroupPython] N_element067  label="N_element : 039"  # scripted group (container) (typed FeaturePython)
  n = 2
  ref = N_element
FEATURE [App::DocumentObjectGroupPython] O_element129  label="O_element : 9"  # scripted group (container) (typed FeaturePython)
  n = 9
  ref = O_element
FEATURE [App::DocumentObjectGroupPython] P_element018  label="P_element : 007"  # scripted group (container) (typed FeaturePython)
  n = 1
  ref = P_element
FEATURE [App::DocumentObjectGroupPython] G4_DNA_U  # scripted group (container) (typed FeaturePython)
  Dunit = g/cm3
  Dvalue = 1
  Group = -> [H_element137,C_element147,N_element067,O_element129,P_element018]
  conduct = 2
  density = 1
  expand = 3
  formula = G4_DNA_U
  name = G4_DNA_U
  specific = 4
FEATURE [App::DocumentObjectGroupPython] H_element138  label="H_element : 085"  # scripted group (container) (typed FeaturePython)
  n = 11
  ref = H_element
FEATURE [App::DocumentObjectGroupPython] C_element148  label="C_element : 093"  # scripted group (container) (typed FeaturePython)
  n = 10
  ref = C_element
FEATURE [App::DocumentObjectGroupPython] N_element068  label="N_element : 040"  # scripted group (container) (typed FeaturePython)
  n = 2
  ref = N_element
FEATURE [App::DocumentObjectGroupPython] O_element130  label="O_element : 081"  # scripted group (container) (typed FeaturePython)
  n = 9
  ref = O_element
FEATURE [App::DocumentObjectGroupPython] P_element019  label="P_element : 008"  # scripted group (container) (typed FeaturePython)
  n = 1
  ref = P_element
FEATURE [App::DocumentObjectGroupPython] G4_DNA_MU  # scripted group (container) (typed FeaturePython)
  Dunit = g/cm3
  Dvalue = 1
  Group = -> [H_element138,C_element148,N_element068,O_element130,P_element019]
  conduct = 2
  density = 1
  expand = 3
  formula = G4_DNA_MU
  name = G4_DNA_MU
  specific = 4
FEATURE [App::DocumentObjectGroupPython] BioChemical  # scripted group (container) (typed FeaturePython)
  Group = -> [G4_CYTOSINE,G4_THYMINE,G4_URACIL,G4_DNA_ADENINE,G4_DNA_GUANINE,G4_DNA_CYTOSINE,G4_DNA_THYMINE,G4_DNA_URACIL,G4_DNA_ADENOSINE,G4_DNA_GUANOSINE,G4_DNA_CYTIDINE,G4_DNA_URIDINE,G4_DNA_METHYLURIDINE,G4_DNA_MONOPHOSPHATE,G4_DNA_A,G4_DNA_G,G4_DNA_C,G4_DNA_U,G4_DNA_MU]
FEATURE [App::DocumentObjectGroupPython] G4Materials  # scripted group (container) (typed FeaturePython)
  Group = -> [NIST,Element,HEP,Space,BioChemical]
  version = 1
FEATURE [App::DocumentObjectGroupPython] Geant4  # scripted group (container) (typed FeaturePython)
  Group = -> [G4Isotopes,G4Elements,G4Materials]
FEATURE [App::DocumentObjectGroupPython] Materials  # scripted group (container) (typed FeaturePython)
  Group = -> [Geant4]
FEATURE [Part::FeaturePython] GDMLBox_WorldBox  # WARN: FeaturePython — macro-defined, semantics opaque (R4)
  lunit = 2
  material = 5
  x = 273
  y = 273
  z = 130
FEATURE [Part::FeaturePython] GDMLBox_Box  # WARN: FeaturePython — macro-defined, semantics opaque (R4)
  Placement = pos=(20,0,0) rot=(0,0,1;0rad)
  lunit = 2
  material = 0
  x = 10
  y = 10
  z = 10
FEATURE [Part::FeaturePython] GDMLTube  # WARN: FeaturePython — macro-defined, semantics opaque (R4)
  Placement = pos=(17,-4,0) rot=(0,0,1;0rad)
  aunit = 1
  deltaphi = 90
  lunit = 2
  material = 0
  rmax = 7
  rmin = 5
  startphi = 0
  z = 7
FEATURE [App::Part] LV_Tube
  Group = -> [GDMLTube]
  Origin = -> Origin003
  SkinSurface = 0
FEATURE [App::Part] LV_Box
  Group = -> [GDMLBox_Box,LV_Tube]
  Origin = -> Origin002
  Placement = pos=(0,0,0) rot=(0,0,1;-0.523599rad)
FEATURE [Part::FeaturePython] Array  # Draft array (typed FeaturePython)
  AlwaysSyncPlacement = false
  Angle = 180
  ArrayType = 1
  Axis = (0,0,1)
  Base = -> LV_Box
  Center = (0,0,0)
  Count = 5
  ExpandArray = false
  Fuse = false
  IntervalAxis = (0,0,0)
  IntervalX = (100,0,0)
  IntervalY = (0,100,0)
  IntervalZ = (0,0,100)
  NumberCircles = 3
  NumberPolar = 5
  NumberX = 2
  NumberY = 2
  NumberZ = 1
  Placement = pos=(-20,-20,0) rot=(0,0,1;0rad)
  PlacementList = 5 placements: [(0,0,0),(0,0,0),(0,0,0),(0,0,0),(0,0,0)]
  RadialDistance = 50
  ScaleList = (5) [(1,1,1),(1,1,1),(1,1,1),(1,1,1),(1,1,1)]
  Symmetry = 1
  TangentialDistance = 25
FEATURE [App::Part] Part  label="experiment"
  Group = -> [LV_Box,Array]
  Origin = -> Origin001
FEATURE [Part::Sphere] Sphere
  Angle1 = -90
  Angle2 = 90
  Angle3 = 360
  AttacherType = Attacher::AttachEngine3D
  Placement = pos=(-20,-20,0) rot=(0,0,1;0rad)
  Radius = 1
FEATURE [App::Part] Part001
  Group = -> [Sphere]
  Origin = -> Origin004
FEATURE [App::Part] worldVOL
  Group = -> [GDMLBox_WorldBox,Part,Part001]
  Origin = -> Origin
